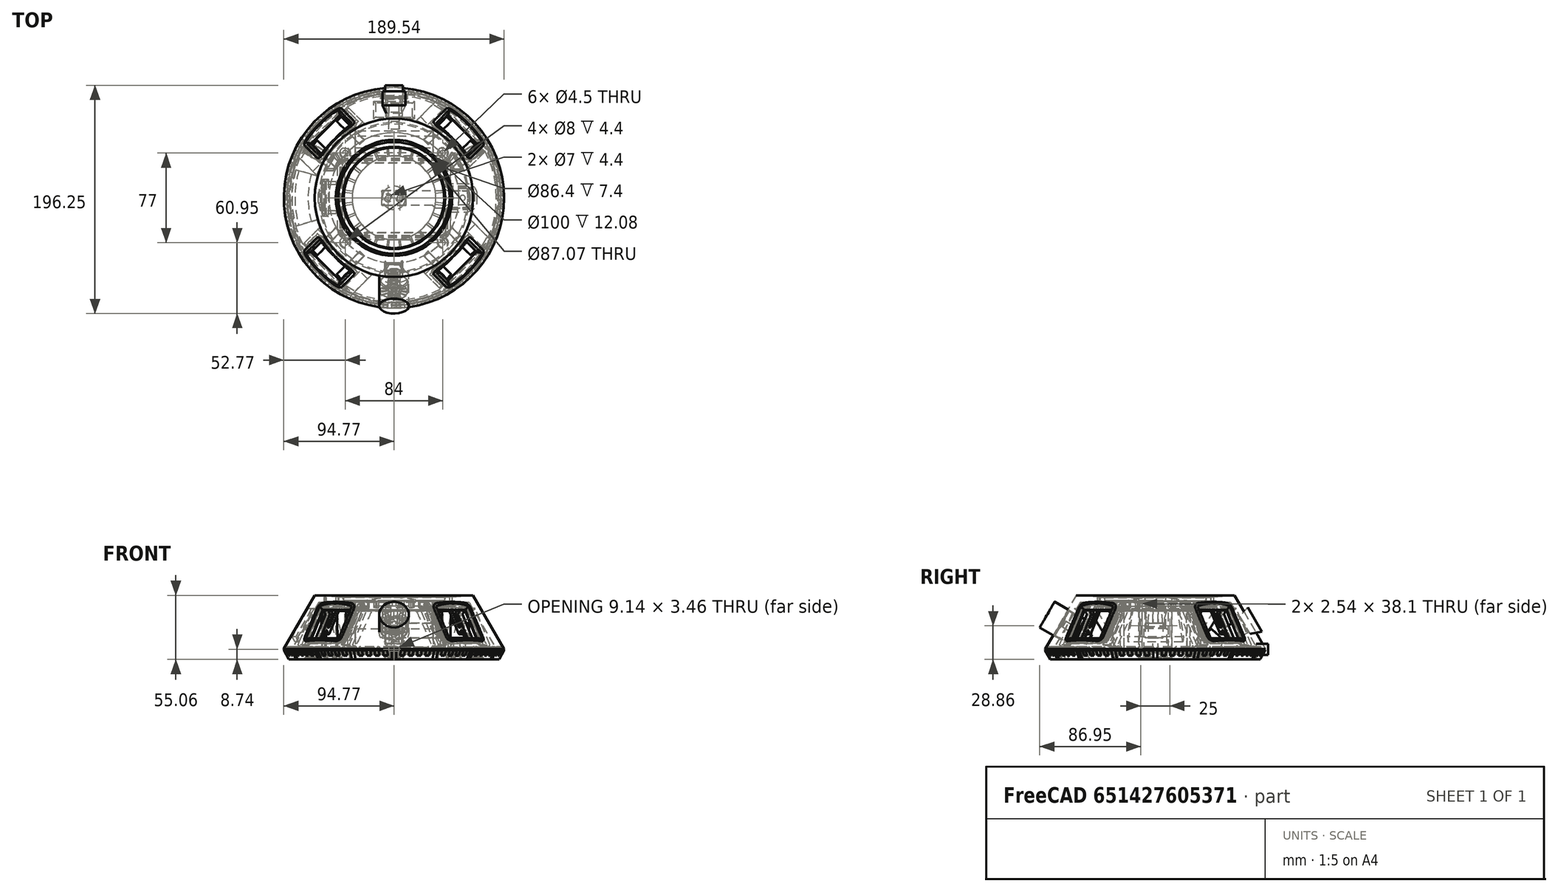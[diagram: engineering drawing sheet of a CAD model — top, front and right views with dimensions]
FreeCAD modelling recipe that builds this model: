
FCSTD DOCUMENT  (FreeCAD 1.0R38641 +1 (Git))
Label: case_v3_r2
License: All rights reserved
LicenseURL: https://en.wikipedia.org/wiki/All_rights_reserved
objects: Sketcher::SketchObject×45, PartDesign::SubShapeBinder×35, PartDesign::Boolean×20, Part::Feature×18, PartDesign::Pocket×14, PartDesign::Pad×14, PartDesign::Body×13, PartDesign::PolarPattern×10, PartDesign::Revolution×9, App::Link×8, Mesh::Feature×8, Part::FeaturePython×7, Part::Compound×5, Part::Cut×4, PartDesign::AdditiveLoft×4, PartDesign::Chamfer×3, PartDesign::MultiTransform×3, PartDesign::Groove×3, Part::Loft×2, Part::Offset2D×2, +6 more types
note: 400 computed .brp shape members not serialized (recipe doc carries the construction recipe); baked Part::Feature solids carry a one-line shape summary decoded from their .brp
EXTERNAL_REF file=parts_v3.FCStd obj=Body006
EXTERNAL_REF file=parts_v3.FCStd obj=Body001
EXTERNAL_REF file=parts_v3.FCStd obj=Body002
EXTERNAL_REF file=parts_v3.FCStd obj=Body005
EXTERNAL_REF file=parts_v3.FCStd obj=Body004
EXTERNAL_REF file=parts_v3.FCStd obj=Body008
EXTERNAL_REF file=parts_v3.FCStd obj=Body007
EXTERNAL_REF file=feet2.FCStd obj=Fusion

FEATURE [App::Link] Link  label="link_loadcell"
  LinkPlacement = pos=(27,-2.86108e-06,22.7) rot=(1,0,0;3.14159rad)
  LinkedObject = -> <external parts_v3.FCStd>#Body006
  Placement = pos=(27,-2.86108e-06,22.7) rot=(1,0,0;3.14159rad)
FEATURE [App::Link] Link001  label="link_display"
  LinkPlacement = pos=(51.5592,51.5591,19.869) rot=(0.48961,0.202803,0.848029;3.8172rad)
  LinkedObject = -> <external parts_v3.FCStd>#Body001
  Placement = pos=(51.5592,51.5591,19.869) rot=(0.48961,0.202803,0.848029;3.8172rad)
FEATURE [Sketcher::SketchObject] Sketch
  ArcFitTolerance = 1e-06
  AttachmentSupport = -> [XZ_Plane]
  FullyConstrained = true
  MakeInternals = false
  MapMode = 5
  Placement = pos=(0,0,0) rot=(1,0,0;1.5708rad)
  sketch-geometry (29):
    g0: LineSegment StartX=94.7691 StartY=0.4 StartZ=0 EndX=68.1243 EndY=46.55 EndZ=0
    g1: LineSegment [constr] StartX=50 StartY=45.0797 StartZ=0 EndX=50 EndY=0 EndZ=0
    g2: LineSegment [constr] StartX=50 StartY=0 StartZ=0 EndX=56 EndY=0 EndZ=0
    g3: LineSegment [constr] StartX=56 StartY=0 StartZ=0 EndX=56 EndY=33 EndZ=0
    g4: LineSegment StartX=63.55 StartY=40.55 StartZ=0 EndX=64.6602 EndY=40.55 EndZ=0
    g5: LineSegment StartX=64.6602 StartY=40.55 StartZ=0 EndX=88.0718 EndY=0 EndZ=0
    g6: LineSegment StartX=88.0718 StartY=0 StartZ=0 EndX=94.7681 EndY=0 EndZ=0
    g7: LineSegment StartX=50 StartY=45.0797 StartZ=0 EndX=68.1243 EndY=46.55 EndZ=0
    g8: LineSegment StartX=47.5346 StartY=44.8797 StartZ=0 EndX=43.5346 EndY=44.5552 EndZ=0
    g9: LineSegment StartX=47.5346 StartY=44.8797 StartZ=0 EndX=47.5346 EndY=37.3797 EndZ=0
    g10: LineSegment StartX=47.5346 StartY=37.3797 StartZ=0 EndX=0 EndY=37.3797 EndZ=0
    g11: LineSegment StartX=0 StartY=37.3797 StartZ=0 EndX=0 EndY=44.8797 EndZ=0
    g12: LineSegment StartX=43.5346 StartY=44.5552 StartZ=0 EndX=43.5346 EndY=41.3797 EndZ=0
    g13-g16: Circle [constr] x4 (B-spline internal-alignment scaffolding for g17; pole/knot coordinates omitted)
    g17: BSplineCurve PolesCount=4 KnotsCount=2 Degree=3 IsPeriodic=0
    g18: GeomPoint [constr] X=0 Y=44.8797 Z=0
    g19: GeomPoint [constr] X=43.5346 Y=41.3797 Z=0
    g20: GeomPoint [constr] X=95 Y=0 Z=0
    g21: ArcOfCircle [constr] CenterX=63.55 CenterY=33 CenterZ=0 NormalX=0 NormalY=0 NormalZ=1 AngleXU=0 Radius=7.55 StartAngle=1.5708 EndAngle=3.14159
    g22: GeomPoint [constr] X=56 Y=40.55 Z=0
    g23: LineSegment StartX=63.55 StartY=40.55 StartZ=0 EndX=56 EndY=33 EndZ=0
    g24: GeomPoint [constr] X=95 Y=0 Z=0
    g25: LineSegment StartX=94.7681 StartY=0 StartZ=0 EndX=94.7681 EndY=0.4 EndZ=0
    g26: LineSegment StartX=94.7691 StartY=0.4 StartZ=0 EndX=94.7681 EndY=0.4 EndZ=0
    g27: LineSegment StartX=56 StartY=33 StartZ=0 EndX=50 EndY=33 EndZ=0
    g28: LineSegment StartX=50 StartY=45.0797 StartZ=0 EndX=50 EndY=33 EndZ=0
  constraints (73):
    c: PointOnObject(g20,g-1)
    c: PointOnObject(g1,g-1)
    c: Coincident(g1,g2)
    c: PointOnObject(g2,g-1)
    c: Coincident(g2,g3)
    c: Horizontal(g4)
    c: Coincident(g4,g5)
    c: PointOnObject(g5,g-1)
    c: Coincident(g5,g6)
    c: DistanceX(g1) = 50
    c: Angle(g4,g5) = 2.0944
    c: Parallel(g5,g0)
    c: Distance(g20,g5) = 6
    c: Parallel(g3,g1)
    c: Distance(g1,g3) = 6
    c: Distance(g0,g4) = 6
    c: Vertical(g1)
    c: DistanceX(g20) = 95
    c: Coincident(g7,g1)
    c: Coincident(g7,g0)
    c: Distance(g22,g7) = 5
    c: Tangent(g8,g7)
    c: Coincident(g8,g9)
    c: Vertical(g9)
    c: Coincident(g9,g10)
    c: Horizontal(g10)
    c: Coincident(g10,g11)
    c: PointOnObject(g11,g-2)
    c: Vertical(g11)
    c: DistanceX(g8,g8) = 4
    c: Coincident(g12,g8)
    c: Vertical(g12)
    c: Weight(g13) = 1
    c: Equal(g13,g14)
    c: Equal(g13,g15)
    c: Equal(g13,g16)
    c: InternalAlignment(g13-g16 -> g17) x4
    c: InternalAlignment(g18,g17)
    c: InternalAlignment(g19,g17)
    c: Coincident(g17,g12)
    c: Coincident(g17,g11)
    c: Horizontal(g14,g11)
    c: Horizontal(g12,g15)
    c: DistanceY(g12,g11) = 3.5
    c: DistanceY(g10,g12) = 4
    c: Horizontal(g11,g8)
    c: Vertical(g15,g14)
    c: PointOnObject(g20,g0)
    c: PointOnObject(g20,g6)
    c: PointOnObject(g22,g3)
    c: PointOnObject(g22,g4)
    c: Tangent(g3,g21) = 1.5708
    c: Tangent(g4,g21) = 1.5708
    c: Coincident(g23,g3)
    c: Coincident(g23,g4)
    c: DistanceY(g0) = 46.55
    c: DistanceY(g8,g1) = 0.2
    c: DistanceY(g3) = 33
    c: PointOnObject(g24,g6)
    c: PointOnObject(g24,g0)
    c: Coincident(g25,g6)
    c: Vertical(g25)
    c: Coincident(g26,g0)
    c: Coincident(g26,g25)
    c: Horizontal(g26)
    c: DistanceY(g25,g25) = 0.4
    c: DistanceX(g26,g26) = 0.001
    c: DistanceX(g14) = 16
    c: Coincident(g27,g3)
    c: PointOnObject(g27,g1)
    c: Horizontal(g27)
    c: Coincident(g28,g1)
    c: Coincident(g28,g27)
FEATURE [PartDesign::Revolution] Revolution
  Angle = 360
  Angle2 = 60
  Axis = (0,2e-16,1)
  Base = (0,0,0)
  Placement = pos=(0,0,0) rot=(1,0,0;1.5708rad)
  Profile = -> Sketch
  ReferenceAxis = -> Sketch [V_Axis]
  Refine = true
  Suppressed = false
  Type = 0
FEATURE [App::Link] Link002  label="link_usb"
  LinkPlacement = pos=(4.80827e-07,85.5,2.99999) rot=(0,-1,0;3.14159rad)
  LinkedObject = -> <external parts_v3.FCStd>#Body002
  Placement = pos=(4.80827e-07,85.5,2.99999) rot=(0,-1,0;3.14159rad)
FEATURE [App::Link] Link003  label="link_switch"
  LinkPlacement = pos=(-3.18281e-07,76.966,20.9382) rot=(0.250563,-0.935113,-0.250563;1.63783rad)
  LinkedObject = -> <external parts_v3.FCStd>#Body005
  Placement = pos=(-3.18281e-07,76.966,20.9382) rot=(0.250563,-0.935113,-0.250563;1.63783rad)
FEATURE [Part::FeaturePython] Array  label="ArrayDisplay"  # Draft array (typed FeaturePython)
  AlwaysSyncPlacement = false
  Angle = 360
  ArrayType = 1
  Axis = (0,0,1)
  Base = -> Link001
  Center = (0,0,1)
  Count = 4
  ExpandArray = false
  Fuse = false
  IntervalAxis = (0,0,0)
  IntervalX = (50,0,0)
  IntervalY = (0,50,0)
  IntervalZ = (0,0,50)
  NumberCircles = 3
  NumberPolar = 4
  NumberX = 2
  NumberY = 2
  NumberZ = 1
  PlacementList = 4 placements: [(51.5592,51.5591,19.869),(-51.5591,51.5592,19.869),(-51.5592,-51.5591,19.869),(51.5591,-51.5592,19.869)]
  RadialDistance = 50
  ScaleList = (4) [(1,1,1),(1,1,1),(1,1,1),(1,1,1)]
  Symmetry = 1
  TangentialDistance = 25
FEATURE [App::Link] Link004  label="link_akku"
  LinkPlacement = pos=(-33.4675,48.0509,5.40002) rot=(0.707107,0,0.707107;3.14159rad)
  LinkedObject = -> <external parts_v3.FCStd>#Body004
  Placement = pos=(-33.4675,48.0509,5.40002) rot=(0.707107,0,0.707107;3.14159rad)
FEATURE [PartDesign::SubShapeBinder] Binder012
  BindCopyOnChange = 0
  BindMode = 0
  ClaimChildren = false
  Context = -> Body [Binder012.]
  Fuse = false
  MakeFace = true
  OffsetFill = false
  OffsetIntersection = false
  OffsetJoinType = 0
  OffsetOpenResult = false
  PartialLoad = false
  Refine = true
  Relative = true
  Support = -> [Link001[Pad028.Face4]]
  _Version = 2
FEATURE [PartDesign::Pocket] Pocket  label="PocketDisplayBack"
  BaseFeature = -> Revolution
  Direction = (0.612372,0.612372,0.5)
  Length = 7
  Length2 = 1
  Placement = pos=(0,0,0) rot=(1,0,0;1.5708rad)
  Profile = -> Binder012
  Refine = true
  Reversed = true
  Suppressed = false
  Type = 4
FEATURE [PartDesign::PolarPattern] PolarPattern
  Angle = 360
  Axis = -> Z_Axis
  BaseFeature = -> Pocket
  Mode = 0
  Occurrences = 4
  Offset = 120
  Originals = -> [Pocket]
  Placement = pos=(0,0,0) rot=(1,0,0;1.5708rad)
  Refine = true
  Suppressed = false
  TransformMode = 0
FEATURE [PartDesign::Body] Body  label="BaseShape"
  AllowCompound = true
  Group = -> [Sketch,Revolution,Binder012,Pocket,PolarPattern]
  Origin = -> Origin
  Tip = -> PolarPattern
FEATURE [Part::Cut] Cut  label="CutDisplay"
  Base = -> Body
  Refine = true
  Tool = -> Array
FEATURE [Sketcher::SketchObject] Sketch015
  ArcFitTolerance = 1e-06
  AttachmentSupport = -> [YZ_Plane010]
  FullyConstrained = true
  MakeInternals = false
  MapMode = 5
  Placement = pos=(0,0,0) rot=(0.57735,-0.57735,-0.57735;2.0944rad)
  sketch-geometry (27):
    g0: LineSegment StartX=94.7691 StartY=-1 StartZ=0 EndX=90.4389 EndY=-8.5 EndZ=0
    g1: LineSegment StartX=90.4389 StartY=-8.5 StartZ=0 EndX=10 EndY=-8.5 EndZ=0
    g2: LineSegment StartX=10 StartY=-8.5 StartZ=0 EndX=10 EndY=-2.5 EndZ=0
    g3: LineSegment StartX=94.1691 StartY=0 StartZ=0 EndX=94.1691 EndY=-0.6 EndZ=0
    g4: LineSegment StartX=94.7691 StartY=-0.6 StartZ=0 EndX=94.1691 EndY=-0.6 EndZ=0
    g5: LineSegment StartX=89.4876 StartY=-2.5 StartZ=0 EndX=10 EndY=-2.5 EndZ=0
    g6: LineSegment [constr] StartX=95 StartY=0 StartZ=0 EndX=89.2265 EndY=10 EndZ=0
    g7: LineSegment [constr] StartX=89 StartY=0 StartZ=0 EndX=83.2265 EndY=10 EndZ=0
    g8: LineSegment StartX=89.9876 StartY=1.1 StartZ=0 EndX=89.3876 EndY=1.7 EndZ=0
    g9: LineSegment StartX=89.3876 StartY=1.7 StartZ=0 EndX=89.9876 EndY=2.41505 EndZ=0
    g10: LineSegment StartX=89.9876 StartY=2.41505 StartZ=0 EndX=91.7876 EndY=2.41505 EndZ=0
    g11: LineSegment StartX=92.6876 StartY=1.7 StartZ=0 EndX=92.2876 EndY=1.7 EndZ=0
    g12: LineSegment [constr] StartX=92.6876 StartY=1.7 StartZ=0 EndX=93.6691 EndY=0 EndZ=0
    g13: LineSegment StartX=94.7691 StartY=-0.6 StartZ=0 EndX=94.7691 EndY=-1 EndZ=0
    g14: LineSegment [constr] StartX=94.7691 StartY=-1 StartZ=0 EndX=95 EndY=-0.6 EndZ=0
    g15: LineSegment [constr] StartX=95 StartY=-0.6 StartZ=0 EndX=94.7691 EndY=-0.6 EndZ=0
    g16: LineSegment StartX=94.1691 StartY=0 StartZ=0 EndX=92.6876 EndY=0 EndZ=0
    g17: LineSegment StartX=89.9876 StartY=1.1 StartZ=0 EndX=89.9876 EndY=0 EndZ=0
    g18: LineSegment StartX=89.9876 StartY=0 StartZ=0 EndX=89.9876 EndY=-3.9 EndZ=0
    g19: LineSegment StartX=91.7876 StartY=-2.9 StartZ=0 EndX=91.7876 EndY=0 EndZ=0
    g20: LineSegment StartX=91.7876 StartY=0 StartZ=0 EndX=91.7876 EndY=2.41505 EndZ=0
    g21: LineSegment StartX=92.2876 StartY=1.7 StartZ=0 EndX=92.2876 EndY=0 EndZ=0
    g22: LineSegment StartX=92.2876 StartY=0 StartZ=0 EndX=92.2876 EndY=-2.9 EndZ=0
    g23: LineSegment StartX=91.7876 StartY=-2.9 StartZ=0 EndX=92.2876 EndY=-2.9 EndZ=0
    g24: LineSegment StartX=89.4876 StartY=-2.5 StartZ=0 EndX=89.4876 EndY=-3.9 EndZ=0
    g25: LineSegment StartX=89.4876 StartY=-3.9 StartZ=0 EndX=89.9876 EndY=-3.9 EndZ=0
    g26: LineSegment StartX=92.6876 StartY=0 StartZ=0 EndX=92.6876 EndY=1.7 EndZ=0
  constraints (81):
    c: Coincident(g0,g1)
    c: Horizontal(g1)
    c: Coincident(g1,g2)
    c: Vertical(g2)
    c: Angle(g0,g1) = 2.0944
    c: DistanceX(g2) = 10
    c: Coincident(g4,g3)
    c: Horizontal(g4)
    c: DistanceX(g4,g4) = 0.6
    c: Horizontal(g5)
    c: Coincident(g2,g5)
    c: Vertical(g3)
    c: PointOnObject(g6,g-1)
    c: Angle(g-1,g6) = 2.0944
    c: PointOnObject(g7,g-1)
    c: DistanceX(g7) = 89
    c: Parallel(g7,g6)
    c: DistanceY(g0) = -8.5
    c: Coincident(g8,g9)
    c: Coincident(g9,g10)
    c: Horizontal(g10)
    c: DistanceX(g8,g8) = 0.6
    c: Angle(g9,g10) = 2.26893
    c: Distance(g12,g3) = 0.5
    c: DistanceX(g10,g10) = 1.8
    c: Angle(g12,g-1) = 1.0472
    c: Coincident(g12,g11)
    c: Horizontal(g6,g7)
    c: DistanceY(g7) = 10
    c: DistanceY(g8) = 1.7
    c: Coincident(g13,g4)
    c: Vertical(g13)
    c: DistanceY(g13,g13) = 0.4
    c: Coincident(g14,g15)
    c: Coincident(g15,g4)
    c: Horizontal(g15)
    c: Tangent(g0,g14) = 1.5708
    c: DistanceX(g14) = 95
    c: Coincident(g0,g13)
    c: Vertical(g6,g14)
    c: DistanceY(g4) = -0.6
    c: Coincident(g16,g3)
    c: Horizontal(g16)
    c: PointOnObject(g12,g16)
    c: DistanceY(g5) = -2.5
    c: Horizontal(g8,g11)
    c: DistanceX(g8,g11) = 3.3
    c: Angle(g8,g-1) = 0.785398
    c: Coincident(g8,g17)
    c: PointOnObject(g17,g-1)
    c: Vertical(g17)
    c: Coincident(g17,g18)
    c: PointOnObject(g19,g-1)
    c: Coincident(g19,g20)
    c: Coincident(g20,g10)
    c: Vertical(g20)
    c: PointOnObject(g21,g-1)
    c: Coincident(g21,g22)
    c: PointOnObject(g16,g-1)
    c: Vertical(g21)
    c: Coincident(g23,g19)
    c: Coincident(g23,g22)
    c: Parallel(g19,g18)
    c: Coincident(g5,g24)
    c: Coincident(g24,g25)
    c: Coincident(g25,g18)
    c: Horizontal(g25)
    c: Horizontal(g23)
    c: Parallel(g19,g22)
    c: Parallel(g24,g18)
    c: Coincident(g26,g11)
    c: Vertical(g26)
    c: DistanceY(g18,g8) = 5
    c: Vertical(g18)
    c: Coincident(g26,g16)
    c: Vertical(g8,g9)
    c: Coincident(g21,g11)
    c: DistanceX(g10,g11) = 0.5
    c: Horizontal(g11)
    c: Equal(g23,g25)
    c: DistanceY(g18,g19) = 1
FEATURE [PartDesign::Revolution] Revolution001
  Angle = 360
  Angle2 = 60
  Axis = (0,0,1)
  Base = (0,0,0)
  Placement = pos=(0,0,0) rot=(1,1,1;2.0944rad)
  Profile = -> Sketch015
  ReferenceAxis = -> Sketch015 [V_Axis]
  Refine = true
  Reversed = true
  Suppressed = false
  Type = 0
FEATURE [PartDesign::SubShapeBinder] Binder014
  BindCopyOnChange = 0
  BindMode = 0
  ClaimChildren = false
  Context = -> Array001 [Binder014.]
  Fuse = false
  MakeFace = true
  Offset = 5
  OffsetFill = false
  OffsetIntersection = false
  OffsetJoinType = 0
  OffsetOpenResult = false
  PartialLoad = false
  Refine = true
  Relative = true
  Support = -> [Cut[Edge167,Edge166,Edge169,Edge168]]
  _Version = 2
FEATURE [PartDesign::Pad] Pad
  Direction = (0.612372,0.612372,0.5)
  Length = 10
  Length2 = 10
  Profile = -> Binder014
  Refine = true
  Suppressed = false
  Type = 0
FEATURE [PartDesign::Body] Body001  label="Dispcut"
  AllowCompound = false
  Group = -> [Binder014,Pad]
  Origin = -> Origin001
  Tip = -> Pad
FEATURE [Part::MultiCommon] Common  label="base_bezel"
  Refine = true
  Shapes = -> [Body001,Cut]
FEATURE [Part::FeaturePython] Array001  label="ArrayDispcut"  # Draft array (typed FeaturePython)
  AlwaysSyncPlacement = false
  Angle = 360
  ArrayType = 1
  Axis = (0,0,1)
  Base = -> Body001
  Center = (0,0,1)
  Count = 4
  ExpandArray = false
  Fuse = false
  IntervalAxis = (0,0,0)
  IntervalX = (50,0,0)
  IntervalY = (0,50,0)
  IntervalZ = (0,0,50)
  NumberCircles = 3
  NumberPolar = 4
  NumberX = 2
  NumberY = 2
  NumberZ = 1
  PlacementList = 4 placements: [(0,0,0),(0,0,0),(0,0,0),(0,0,0)]
  RadialDistance = 50
  ScaleList = (4) [(1,1,1),(1,1,1),(1,1,1),(1,1,1)]
  Symmetry = 1
  TangentialDistance = 25
FEATURE [Part::Cut] Cut001  label="CutBezel"
  Base = -> Cut
  Refine = true
  Tool = -> Array001
FEATURE [Part::FeaturePython] Slice_child6  label="base_top"  # WARN: FeaturePython — macro-defined, semantics opaque (R4)
  Base = -> Cut001
  FilterType = 1
  Invert = false
  OverrideMaxVal = 0
  WindowFrom = 80
  WindowTo = 100
  items = 1
FEATURE [Part::FeaturePython] CompoundFilter  label="base_outer"  # WARN: FeaturePython — macro-defined, semantics opaque (R4)
  Base = -> Cut001
  FilterType = 1
  Invert = false
  OverrideMaxVal = 0
  WindowFrom = 80
  WindowTo = 100
  items = 0
FEATURE [App::Link] Link005  label="link_esp"
  LinkPlacement = pos=(-58.2736,-4.46698e-09,44.8) rot=(-0.707107,0,0.707107;3.14159rad)
  LinkedObject = -> <external parts_v3.FCStd>#Body008
  Placement = pos=(-58.2736,-4.46698e-09,44.8) rot=(-0.707107,0,0.707107;3.14159rad)
FEATURE [App::Link] Link006  label="link_encoder"
  LinkPlacement = pos=(-2.17522e-06,-65.3643,13.9856) rot=(0.447214,0.447214,-0.774597;1.82348rad)
  LinkedObject = -> <external parts_v3.FCStd>#Body007
  Placement = pos=(-2.17522e-06,-65.3643,13.9856) rot=(0.447214,0.447214,-0.774597;1.82348rad)
FEATURE [Sketcher::SketchObject] Sketch017
  ArcFitTolerance = 1e-06
  AttachmentSupport = -> [XY_Plane011]
  FullyConstrained = true
  MakeInternals = false
  MapMode = 5
  sketch-geometry (7):
    g0: LineSegment StartX=0 StartY=3 StartZ=0 EndX=8 EndY=3 EndZ=0
    g1: LineSegment StartX=8 StartY=3 StartZ=0 EndX=8 EndY=0 EndZ=0
    g2: LineSegment StartX=8 StartY=0 StartZ=0 EndX=9 EndY=-1.1e-15 EndZ=0
    g3: ArcOfCircle CenterX=27.5 CenterY=-3.4e-15 CenterZ=0 NormalX=0 NormalY=0 NormalZ=1 AngleXU=0 Radius=18.5 StartAngle=2.8113 EndAngle=3.14159
    g4: ArcOfCircle CenterX=-7.5 CenterY=12 CenterZ=0 NormalX=0 NormalY=0 NormalZ=1 AngleXU=0 Radius=18.5 StartAngle=5.95289 EndAngle=6.28319
    g5: LineSegment StartX=11 StartY=12 StartZ=0 EndX=0 EndY=12 EndZ=0
    g6: LineSegment StartX=0 StartY=12 StartZ=0 EndX=0 EndY=3 EndZ=0
  constraints (22):
    c: PointOnObject(g0,g-2)
    c: Horizontal(g0)
    c: Coincident(g0,g1)
    c: PointOnObject(g1,g-1)
    c: Vertical(g1)
    c: Coincident(g1,g2)
    c: PointOnObject(g2,g-1)
    c: Perpendicular(g2,g3) = 4.71239
    c: Tangent(g3,g4) = 1.5708
    c: Coincident(g4,g5)
    c: PointOnObject(g5,g-2)
    c: Horizontal(g5)
    c: Coincident(g5,g6)
    c: Coincident(g6,g0)
    c: DistanceY(g1,g1) = 3
    c: DistanceX(g2,g2) = 1
    c: DistanceY(g5) = 12
    c: Perpendicular(g4,g5)
    c: DistanceX(g5,g5) = 11
    c: DistanceX(g3,g4) = 1
    c: DistanceX(g2,g3) = 1
    c: DistanceX(g0,g0) = 8
FEATURE [PartDesign::Revolution] Revolution002
  Angle = 30
  Angle2 = 60
  Axis = (1,0,0)
  Base = (0,0,0)
  Profile = -> Sketch017
  ReferenceAxis = -> Sketch017 [H_Axis]
  Refine = true
  Suppressed = false
  Type = 0
FEATURE [Sketcher::SketchObject] Sketch018
  ArcFitTolerance = 1e-06
  AttachmentSupport = -> [XY_Plane011]
  FullyConstrained = true
  MakeInternals = false
  MapMode = 5
  expr: Constraints[10] = Sketch017.Constraints[14]
  expr: Constraints[11] = Sketch017.Constraints[16]
  sketch-geometry (7):
    g0: LineSegment StartX=0 StartY=3 StartZ=0 EndX=8 EndY=3 EndZ=0
    g1: LineSegment StartX=8 StartY=3 StartZ=0 EndX=8 EndY=0 EndZ=0
    g2: LineSegment StartX=8 StartY=0 StartZ=0 EndX=9 EndY=-2.8e-15 EndZ=0
    g3: ArcOfCircle CenterX=27.5 CenterY=-5.1e-15 CenterZ=0 NormalX=0 NormalY=0 NormalZ=1 AngleXU=0 Radius=18.5 StartAngle=2.8113 EndAngle=3.14159
    g4: LineSegment StartX=10 StartY=12 StartZ=0 EndX=0 EndY=12 EndZ=0
    g5: LineSegment StartX=0 StartY=12 StartZ=0 EndX=0 EndY=3 EndZ=0
    g6: LineSegment StartX=10 StartY=6 StartZ=0 EndX=10 EndY=12 EndZ=0
  constraints (21):
    c: Horizontal(g0)
    c: Coincident(g0,g1)
    c: PointOnObject(g1,g-1)
    c: Vertical(g1)
    c: Coincident(g1,g2)
    c: PointOnObject(g2,g-1)
    c: Perpendicular(g2,g3) = 4.71239
    c: Horizontal(g4)
    c: Coincident(g4,g5)
    c: Coincident(g5,g0)
    c: DistanceY(g1,g1) = 3
    c: DistanceY(g4) = 12
    c: DistanceX(g3) = 10
    c: Vertical(g5)
    c: PointOnObject(g0,g-2)
    c: DistanceY(g3) = 6
    c: Coincident(g6,g3)
    c: Coincident(g6,g4)
    c: Vertical(g6)
    c: DistanceX(g2,g3) = 1
    c: DistanceX(g0,g0) = 8
FEATURE [PartDesign::Revolution] Revolution003
  Angle = 30
  Angle2 = 60
  Axis = (1,0,0)
  Base = (0,0,0)
  BaseFeature = -> Revolution002
  Profile = -> Sketch018
  ReferenceAxis = -> Sketch018 [H_Axis]
  Refine = true
  Reversed = true
  Suppressed = false
  Type = 0
FEATURE [PartDesign::PolarPattern] PolarPattern001
  Angle = 360
  Axis = -> X_Axis011
  BaseFeature = -> Revolution003
  Mode = 0
  Occurrences = 6
  Offset = 120
  Refine = true
  Suppressed = false
  TransformMode = 1
FEATURE [Sketcher::SketchObject] Sketch021
  ArcFitTolerance = 1e-06
  AttachmentOffset = pos=(0,0,0) rot=(0,0,1;-1.5708rad)
  AttachmentSupport = -> [XY_Plane010]
  FullyConstrained = true
  MakeInternals = false
  MapMode = 5
  Placement = pos=(0,0,0) rot=(0,0,1;4.71239rad)
  sketch-geometry (4):
    g0: LineSegment StartX=-97.6 StartY=7.575 StartZ=0 EndX=-97.6 EndY=-7.575 EndZ=0
    g1: LineSegment StartX=-97.6 StartY=-7.575 StartZ=0 EndX=-86.8 EndY=-7.575 EndZ=0
    g2: LineSegment StartX=-86.8 StartY=-7.575 StartZ=0 EndX=-86.8 EndY=7.575 EndZ=0
    g3: LineSegment StartX=-86.8 StartY=7.575 StartZ=0 EndX=-97.6 EndY=7.575 EndZ=0
  constraints (11):
    c: Coincident(g0,g1)
    c: Coincident(g1,g2)
    c: Coincident(g2,g3)
    c: Coincident(g3,g0)
    c: Vertical(g0)
    c: Horizontal(g1)
    c: Horizontal(g3)
    c: Symmetric(g2,g1,g-1)
    c: DistanceY(g0,g0) = 15.15
    c: DistanceX(g1,g1) = 10.8
    c: DistanceX(g1) = -86.8
FEATURE [PartDesign::SubShapeBinder] Binder  label="Binder_usb"
  BindCopyOnChange = 0
  BindMode = 0
  ClaimChildren = false
  Context = -> Body010 [Boolean.Binder.]
  Fuse = false
  MakeFace = true
  OffsetFill = false
  OffsetIntersection = false
  OffsetJoinType = 0
  OffsetOpenResult = false
  PartialLoad = false
  Refine = true
  Relative = true
  Support = -> [Link002[Pad022.]]
  _Version = 2
FEATURE [PartDesign::SubShapeBinder] Binder015
  BindCopyOnChange = 0
  BindMode = 0
  ClaimChildren = false
  Context = -> Body010 [Binder015.]
  Fuse = false
  MakeFace = true
  OffsetFill = false
  OffsetIntersection = false
  OffsetJoinType = 0
  OffsetOpenResult = false
  PartialLoad = false
  Refine = true
  Relative = true
  Support = -> [Link004[Pad.]]
  _Version = 2
FEATURE [Sketcher::SketchObject] Sketch024  label="SketchInnerBottom"
  ArcFitTolerance = 1e-06
  AttachmentOffset = pos=(0,0,0) rot=(0,0,1;3.14159rad)
  AttachmentSupport = -> [XY_Plane012]
  FullyConstrained = true
  MakeInternals = false
  MapMode = 5
  Placement = pos=(0,0,0) rot=(0,0,1;3.14159rad)
  sketch-geometry (10):
    g0: LineSegment StartX=-39.5 StartY=-30 StartZ=0 EndX=39.5 EndY=-30 EndZ=0
    g1: LineSegment StartX=42.5 StartY=-27 StartZ=0 EndX=42.5 EndY=27 EndZ=0
    g2: LineSegment StartX=39.5 StartY=30 StartZ=0 EndX=-39.5 EndY=30 EndZ=0
    g3: LineSegment StartX=-42.5 StartY=27 StartZ=0 EndX=-42.5 EndY=-27 EndZ=0
    g4: ArcOfCircle CenterX=-39.5 CenterY=-27 CenterZ=0 NormalX=0 NormalY=0 NormalZ=1 AngleXU=0 Radius=3 StartAngle=3.14159 EndAngle=4.71239
    g5: ArcOfCircle CenterX=39.5 CenterY=-27 CenterZ=0 NormalX=0 NormalY=0 NormalZ=1 AngleXU=0 Radius=3 StartAngle=4.71239 EndAngle=6.28319
    g6: ArcOfCircle CenterX=39.5 CenterY=27 CenterZ=0 NormalX=0 NormalY=0 NormalZ=1 AngleXU=0 Radius=3 StartAngle=2e-16 EndAngle=1.5708
    g7: ArcOfCircle CenterX=-39.5 CenterY=27 CenterZ=0 NormalX=0 NormalY=0 NormalZ=1 AngleXU=0 Radius=3 StartAngle=1.5708 EndAngle=3.14159
    g8: GeomPoint [constr] X=42.5 Y=30 Z=0
    g9: GeomPoint [constr] X=0 Y=0 Z=0
  constraints (22):
    c: Tangent(g0,g4) = -1.5708
    c: Tangent(g0,g5) = -1.5708
    c: Tangent(g1,g5) = -1.5708
    c: Tangent(g1,g6) = -1.5708
    c: Tangent(g2,g6) = -1.5708
    c: Tangent(g2,g7) = -1.5708
    c: Tangent(g3,g7) = -1.5708
    c: Tangent(g3,g4) = -1.5708
    c: Horizontal(g0)
    c: Horizontal(g2)
    c: Vertical(g1)
    c: Vertical(g3)
    c: Equal(g4,g5)
    c: Equal(g5,g6)
    c: Equal(g6,g7)
    c: Symmetric(g2,g0,g9)
    c: PointOnObject(g8,g1)
    c: PointOnObject(g8,g2)
    c: Distance(g1,g3) = 85
    c: Distance(g0,g2) = 60
    c: Radius(g5) = 3
    c: Coincident(g9,g-1)
FEATURE [Sketcher::SketchObject] Sketch025  label="SketchInnerTop"
  ArcFitTolerance = 1e-06
  AttachmentOffset = pos=(0,0,33) rot=(0,0,1;0rad)
  AttachmentSupport = -> [XY_Plane012]
  FullyConstrained = true
  MakeInternals = false
  MapMode = 5
  Placement = pos=(0,0,33) rot=(0,0,1;0rad)
  sketch-geometry (1):
    g0: Circle CenterX=0 CenterY=0 CenterZ=0 NormalX=0 NormalY=0 NormalZ=1 AngleXU=0 Radius=50
  constraints (2):
    c: Diameter(g0) = 100
    c: Coincident(g0,g-1)
FEATURE [Sketcher::SketchObject] Sketch027
  ArcFitTolerance = 1e-06
  AttachmentSupport = -> [XY_Plane012]
  FullyConstrained = true
  MakeInternals = false
  MapMode = 5
  sketch-geometry (8):
    g0: LineSegment StartX=47.5 StartY=12 StartZ=0 EndX=67.5 EndY=12 EndZ=0
    g1: LineSegment StartX=70.5 StartY=9 StartZ=0 EndX=70.5 EndY=-11.8 EndZ=0
    g2: LineSegment StartX=67.5 StartY=-14.8 StartZ=0 EndX=47.5 EndY=-14.8 EndZ=0
    g3: LineSegment StartX=47.5 StartY=-14.8 StartZ=0 EndX=47.5 EndY=12 EndZ=0
    g4: ArcOfCircle CenterX=67.5 CenterY=9 CenterZ=0 NormalX=0 NormalY=0 NormalZ=1 AngleXU=0 Radius=3 StartAngle=0 EndAngle=1.5708
    g5: GeomPoint [constr] X=70.5 Y=12 Z=0
    g6: ArcOfCircle CenterX=67.5 CenterY=-11.8 CenterZ=0 NormalX=0 NormalY=0 NormalZ=1 AngleXU=0 Radius=3 StartAngle=4.71239 EndAngle=6.28319
    g7: GeomPoint [constr] X=70.5 Y=-14.8 Z=0
  constraints (20):
    c: DistanceX(g3) = 47.5
    c: Horizontal(g0)
    c: Vertical(g1)
    c: Horizontal(g2)
    c: Coincident(g2,g3)
    c: Vertical(g3)
    c: PointOnObject(g5,g0)
    c: PointOnObject(g5,g1)
    c: Tangent(g0,g4) = 1.5708
    c: Tangent(g1,g4) = 1.5708
    c: PointOnObject(g7,g1)
    c: PointOnObject(g7,g2)
    c: Tangent(g1,g6) = 1.5708
    c: Tangent(g2,g6) = 1.5708
    c: Equal(g6,g4)
    c: Radius(g4) = 3
    c: Coincident(g3,g0)
    c: DistanceX(g0,g0) = 20
    c: DistanceY(g0) = 12
    c: DistanceY(g2) = -14.8
FEATURE [Part::Loft] Loft
  Closed = false
  MaxDegree = 5
  Ruled = false
  Sections = -> [Sketch024,Sketch025]
  Solid = true
FEATURE [Part::Offset2D] Offset2D
  Fill = false
  Intersection = false
  Join = 0
  Mode = 1
  SelfIntersection = false
  Source = -> Sketch024
  Value = 6
FEATURE [Part::Offset2D] Offset2D001
  Fill = false
  Intersection = false
  Join = 0
  Mode = 1
  SelfIntersection = false
  Source = -> Sketch025
  Value = 6
FEATURE [Part::Loft] Loft001
  Closed = false
  MaxDegree = 5
  Ruled = false
  Sections = -> [Offset2D001,Offset2D]
  Solid = true
FEATURE [Part::Cut] Cut002  label="base_inner"
  Base = -> Loft001
  Refine = true
  Tool = -> Loft
FEATURE [PartDesign::FeatureBase] BaseFeature
  BaseFeature = -> Cut002
  Suppressed = false
FEATURE [Sketcher::SketchObject] Sketch028
  ArcFitTolerance = 1e-06
  AttachmentOffset = pos=(0,0,10) rot=(0,0,1;0rad)
  AttachmentSupport = -> [XY_Plane012]
  FullyConstrained = true
  MakeInternals = false
  MapMode = 5
  Placement = pos=(0,0,10) rot=(0,0,1;0rad)
  sketch-geometry (11):
    g0: LineSegment StartX=40 StartY=6.8 StartZ=0 EndX=40 EndY=-9.1 EndZ=0
    g1: LineSegment StartX=40 StartY=6.8 StartZ=0 EndX=64.5 EndY=6.8 EndZ=0
    g2: LineSegment StartX=40 StartY=-9.1 StartZ=0 EndX=71.5 EndY=-9.1 EndZ=0
    g3: ArcOfCircle CenterX=64.5 CenterY=5.8 CenterZ=0 NormalX=0 NormalY=0 NormalZ=1 AngleXU=0 Radius=1 StartAngle=0 EndAngle=1.5708
    g4: GeomPoint [constr] X=65.5 Y=6.8 Z=0
    g5: GeomPoint [constr] X=65.5 Y=-9.1 Z=0
    g6: LineSegment StartX=65.5 StartY=5.8 StartZ=0 EndX=65.5 EndY=-7.1 EndZ=0
    g7: LineSegment StartX=66.5 StartY=-8.1 StartZ=0 EndX=71.5 EndY=-8.1 EndZ=0
    g8: LineSegment StartX=71.5 StartY=-8.1 StartZ=0 EndX=71.5 EndY=-9.1 EndZ=0
    g9: ArcOfCircle CenterX=66.5 CenterY=-7.1 CenterZ=0 NormalX=0 NormalY=0 NormalZ=1 AngleXU=0 Radius=1 StartAngle=3.14159 EndAngle=4.71239
    g10: GeomPoint [constr] X=65.5 Y=-8.1 Z=0
  constraints (28):
    c: Vertical(g0)
    c: DistanceX(g0) = 40
    c: Horizontal(g1)
    c: Horizontal(g2)
    c: DistanceY(g5,g-1) = 9.1
    c: DistanceY(g4) = 6.8
    c: Coincident(g1,g0)
    c: Coincident(g2,g0)
    c: DistanceX(g1,g4) = 25.5
    c: PointOnObject(g4,g1)
    c: Tangent(g1,g3) = 1.5708
    c: PointOnObject(g5,g2)
    c: Radius(g3) = 1
    c: Vertical(g6)
    c: PointOnObject(g4,g6)
    c: PointOnObject(g5,g6)
    c: Horizontal(g7)
    c: Coincident(g7,g8)
    c: Coincident(g8,g2)
    c: Vertical(g8)
    c: DistanceY(g8,g8) = 1
    c: PointOnObject(g10,g6)
    c: PointOnObject(g10,g7)
    c: Tangent(g6,g9) = -1.5708
    c: Tangent(g7,g9) = -1.5708
    c: Equal(g9,g3)
    c: DistanceX(g7,g7) = 5
    c: Tangent(g6,g3) = 1.5708
FEATURE [Sketcher::SketchObject] Sketch029
  ArcFitTolerance = 1e-06
  AttachmentOffset = pos=(0,0,26) rot=(0,0,1;0rad)
  AttachmentSupport = -> [XY_Plane012]
  FullyConstrained = true
  MakeInternals = false
  MapMode = 5
  Placement = pos=(0,0,26) rot=(0,0,1;0rad)
  sketch-geometry (8):
    g0: LineSegment StartX=49.5 StartY=12.3 StartZ=0 EndX=67.5 EndY=12.3 EndZ=0
    g1: LineSegment StartX=70.5 StartY=9.3 StartZ=0 EndX=70.5 EndY=-11.8 EndZ=0
    g2: LineSegment StartX=67.5 StartY=-14.8 StartZ=0 EndX=49.5 EndY=-14.8 EndZ=0
    g3: LineSegment StartX=49.5 StartY=-14.8 StartZ=0 EndX=49.5 EndY=12.3 EndZ=0
    g4: ArcOfCircle CenterX=67.5 CenterY=9.3 CenterZ=0 NormalX=0 NormalY=0 NormalZ=1 AngleXU=0 Radius=3 StartAngle=2e-16 EndAngle=1.5708
    g5: GeomPoint [constr] X=70.5 Y=12.3 Z=0
    g6: ArcOfCircle CenterX=67.5 CenterY=-11.8 CenterZ=0 NormalX=0 NormalY=0 NormalZ=1 AngleXU=0 Radius=3 StartAngle=4.71239 EndAngle=6.28319
    g7: GeomPoint [constr] X=70.5 Y=-14.8 Z=0
  constraints (20):
    c: DistanceX(g3) = 49.5
    c: Horizontal(g0)
    c: Vertical(g1)
    c: Horizontal(g2)
    c: Coincident(g2,g3)
    c: Vertical(g3)
    c: PointOnObject(g5,g0)
    c: PointOnObject(g5,g1)
    c: Tangent(g0,g4) = 1.5708
    c: Tangent(g1,g4) = 1.5708
    c: PointOnObject(g7,g1)
    c: PointOnObject(g7,g2)
    c: Tangent(g1,g6) = 1.5708
    c: Tangent(g2,g6) = 1.5708
    c: Equal(g6,g4)
    c: Radius(g4) = 3
    c: Coincident(g3,g0)
    c: DistanceY(g0) = 12.3
    c: DistanceY(g2) = -14.8
    c: DistanceX(g0,g0) = 18
FEATURE [PartDesign::AdditiveLoft] AdditiveLoft  label="AdditiveLC"
  BaseFeature = -> BaseFeature
  Closed = false
  Profile = -> Sketch027
  Refine = true
  Ruled = false
  Sections = -> [Sketch029]
  Suppressed = false
FEATURE [PartDesign::Pocket] Pocket003  label="PocketLC"
  BaseFeature = -> AdditiveLoft
  Direction = (0,0,-1)
  Length = 14
  Length2 = 5
  Profile = -> Sketch028
  ReferenceAxis = -> Sketch028 [N_Axis]
  Refine = true
  Reversed = true
  Suppressed = false
  Type = 0
FEATURE [Sketcher::SketchObject] Sketch030
  ArcFitTolerance = 1e-06
  AttachmentOffset = pos=(0,0,0) rot=(0,0,1;-1.5708rad)
  AttachmentSupport = -> [XY_Plane012]
  FullyConstrained = false
  MakeInternals = false
  MapMode = 5
  Placement = pos=(0,0,0) rot=(0,0,1;4.71239rad)
  sketch-geometry (65):
    g0: LineSegment StartX=-35 StartY=6 StartZ=0 EndX=-35 EndY=-6 EndZ=0
    g1: LineSegment StartX=-35 StartY=-6 StartZ=0 EndX=35 EndY=-6 EndZ=0
    g2: LineSegment StartX=35 StartY=-6 StartZ=0 EndX=35 EndY=6 EndZ=0
    g3: LineSegment StartX=35 StartY=6 StartZ=0 EndX=-35 EndY=6 EndZ=0
    g4: Circle CenterX=0 CenterY=0 CenterZ=0 NormalX=0 NormalY=0 NormalZ=1 AngleXU=0 Radius=2.8
    g5: LineSegment StartX=-58 StartY=11 StartZ=0 EndX=-88 EndY=11 EndZ=0
    g6: LineSegment StartX=-88 StartY=11 StartZ=0 EndX=-88 EndY=-11 EndZ=0
    g7: LineSegment StartX=-88 StartY=-11 StartZ=0 EndX=-58 EndY=-11 EndZ=0
    g8: LineSegment StartX=-58 StartY=-11 StartZ=0 EndX=-58 EndY=-9 EndZ=0
    g9: LineSegment StartX=-85.5 StartY=8 StartZ=0 EndX=-85.5 EndY=-8 EndZ=0
    g10: LineSegment StartX=-84.5 StartY=-9 StartZ=0 EndX=-77.5 EndY=-9 EndZ=0
    g11: LineSegment StartX=-58 StartY=9 StartZ=0 EndX=-59.5 EndY=9 EndZ=0
    g12: LineSegment StartX=-58 StartY=11 StartZ=0 EndX=-58 EndY=9 EndZ=0
    g13: LineSegment StartX=-63.5 StartY=-8 StartZ=0 EndX=-63.5 EndY=-3.5 EndZ=0
    g14: LineSegment StartX=-64.5 StartY=-2.5 StartZ=0 EndX=-68.9 EndY=-2.5 EndZ=0
    g15: LineSegment StartX=-69.9 StartY=-1.5 StartZ=0 EndX=-69.9 EndY=1.5 EndZ=0
    g16: LineSegment StartX=-68.9 StartY=2.5 StartZ=0 EndX=-64.5 EndY=2.5 EndZ=0
    g17: LineSegment StartX=-63.5 StartY=3.5 StartZ=0 EndX=-63.5 EndY=8 EndZ=0
    g18: LineSegment StartX=-60.5 StartY=8 StartZ=0 EndX=-60.5 EndY=-8 EndZ=0
    g19: LineSegment StartX=-64.5 StartY=9 StartZ=0 EndX=-71.5 EndY=9 EndZ=0
    g20: LineSegment StartX=-59.5 StartY=-9 StartZ=0 EndX=-58 EndY=-9 EndZ=0
    g21: ArcOfCircle CenterX=-59.5 CenterY=8 CenterZ=0 NormalX=0 NormalY=0 NormalZ=1 AngleXU=0 Radius=1 StartAngle=1.5708 EndAngle=3.14159
    g22: GeomPoint [constr] X=-60.5 Y=9 Z=0
    g23: ArcOfCircle CenterX=-59.5 CenterY=-8 CenterZ=0 NormalX=0 NormalY=0 NormalZ=1 AngleXU=0 Radius=1 StartAngle=3.14159 EndAngle=4.71239
    g24: GeomPoint [constr] X=-60.5 Y=-9 Z=0
    g25: ArcOfCircle CenterX=-64.5 CenterY=-8 CenterZ=0 NormalX=0 NormalY=0 NormalZ=1 AngleXU=0 Radius=1 StartAngle=4.71239 EndAngle=6.28319
    g26: GeomPoint [constr] X=-63.5 Y=-9 Z=0
    g27: ArcOfCircle CenterX=-64.5 CenterY=-3.5 CenterZ=0 NormalX=0 NormalY=0 NormalZ=1 AngleXU=0 Radius=1 StartAngle=0 EndAngle=1.5708
    g28: GeomPoint [constr] X=-63.5 Y=-2.5 Z=0
    g29: ArcOfCircle CenterX=-64.5 CenterY=3.5 CenterZ=0 NormalX=0 NormalY=0 NormalZ=1 AngleXU=0 Radius=1 StartAngle=4.71239 EndAngle=6.28319
    g30: GeomPoint [constr] X=-63.5 Y=2.5 Z=0
    g31: ArcOfCircle CenterX=-84.5 CenterY=8 CenterZ=0 NormalX=0 NormalY=0 NormalZ=1 AngleXU=0 Radius=1 StartAngle=1.5708 EndAngle=3.14159
    g32: GeomPoint [constr] X=-85.5 Y=9 Z=0
    g33: ArcOfCircle CenterX=-84.5 CenterY=-8 CenterZ=0 NormalX=0 NormalY=0 NormalZ=1 AngleXU=0 Radius=1 StartAngle=3.14159 EndAngle=4.71239
    g34: GeomPoint [constr] X=-85.5 Y=-9 Z=0
    g35: LineSegment StartX=-76.5 StartY=8 StartZ=0 EndX=-76.5 EndY=6.6 EndZ=0
    g36: LineSegment StartX=-75.5 StartY=5.6 StartZ=0 EndX=-73.5 EndY=5.6 EndZ=0
    g37: LineSegment StartX=-72.5 StartY=6.6 StartZ=0 EndX=-72.5 EndY=8 EndZ=0
    g38: LineSegment StartX=-76.5 StartY=-8 StartZ=0 EndX=-76.5 EndY=-6.6 EndZ=0
    g39: LineSegment StartX=-75.5 StartY=-5.6 StartZ=0 EndX=-73.5 EndY=-5.6 EndZ=0
    g40: LineSegment StartX=-72.5 StartY=-6.6 StartZ=0 EndX=-72.5 EndY=-8 EndZ=0
    g41: LineSegment StartX=-71.5 StartY=-9 StartZ=0 EndX=-64.5 EndY=-9 EndZ=0
    g42: LineSegment StartX=-77.5 StartY=9 StartZ=0 EndX=-84.5 EndY=9 EndZ=0
    g43: ArcOfCircle CenterX=-71.5 CenterY=8 CenterZ=0 NormalX=0 NormalY=0 NormalZ=1 AngleXU=0 Radius=1 StartAngle=1.5708 EndAngle=3.14159
    g44: GeomPoint [constr] X=-72.5 Y=9 Z=0
    g45: ArcOfCircle CenterX=-73.5 CenterY=6.6 CenterZ=0 NormalX=0 NormalY=0 NormalZ=1 AngleXU=0 Radius=1 StartAngle=4.71239 EndAngle=6.28319
    g46: GeomPoint [constr] X=-72.5 Y=5.6 Z=0
    g47: ArcOfCircle CenterX=-75.5 CenterY=6.6 CenterZ=0 NormalX=0 NormalY=0 NormalZ=1 AngleXU=0 Radius=1 StartAngle=3.14159 EndAngle=4.71239
    g48: GeomPoint [constr] X=-76.5 Y=5.6 Z=0
    g49: ArcOfCircle CenterX=-77.5 CenterY=8 CenterZ=0 NormalX=0 NormalY=0 NormalZ=1 AngleXU=0 Radius=1 StartAngle=0 EndAngle=1.5708
    g50: GeomPoint [constr] X=-76.5 Y=9 Z=0
    g51: ArcOfCircle CenterX=-71.5 CenterY=-8 CenterZ=0 NormalX=0 NormalY=0 NormalZ=1 AngleXU=0 Radius=1 StartAngle=3.14159 EndAngle=4.71239
    g52: GeomPoint [constr] X=-72.5 Y=-9 Z=0
    g53: ArcOfCircle CenterX=-73.5 CenterY=-6.6 CenterZ=0 NormalX=0 NormalY=0 NormalZ=1 AngleXU=0 Radius=1 StartAngle=0 EndAngle=1.5708
    g54: GeomPoint [constr] X=-72.5 Y=-5.6 Z=0
    g55: ArcOfCircle CenterX=-75.5 CenterY=-6.6 CenterZ=0 NormalX=0 NormalY=0 NormalZ=1 AngleXU=0 Radius=1 StartAngle=1.5708 EndAngle=3.14159
    g56: GeomPoint [constr] X=-76.5 Y=-5.6 Z=0
    g57: ArcOfCircle CenterX=-77.5 CenterY=-8 CenterZ=0 NormalX=0 NormalY=0 NormalZ=1 AngleXU=0 Radius=1 StartAngle=4.71239 EndAngle=6.28319
    g58: GeomPoint [constr] X=-76.5 Y=-9 Z=0
    g59: ArcOfCircle CenterX=-64.5 CenterY=8 CenterZ=0 NormalX=0 NormalY=0 NormalZ=1 AngleXU=0 Radius=1 StartAngle=0 EndAngle=1.5708
    g60: GeomPoint [constr] X=-63.5 Y=9 Z=0
    g61: ArcOfCircle CenterX=-68.9 CenterY=1.5 CenterZ=0 NormalX=0 NormalY=0 NormalZ=1 AngleXU=0 Radius=1 StartAngle=1.5708 EndAngle=3.14159
    g62: GeomPoint [constr] X=-69.9 Y=2.5 Z=0
    g63: ArcOfCircle CenterX=-68.9 CenterY=-1.5 CenterZ=0 NormalX=0 NormalY=0 NormalZ=1 AngleXU=0 Radius=1 StartAngle=3.14159 EndAngle=4.71239
    g64: GeomPoint [constr] X=-69.9 Y=-2.5 Z=0
  constraints (154):
    c: Coincident(g0,g1)
    c: Coincident(g1,g2)
    c: Coincident(g2,g3)
    c: Coincident(g3,g0)
    c: Vertical(g0)
    c: Vertical(g2)
    c: Horizontal(g1)
    c: Horizontal(g3)
    c: Distance(g0,g2) = 70
    c: Symmetric(g0,g2,g-1)
    c: DistanceY(g0,g0) = 12
    c: Diameter(g4) = 5.6
    c: Coincident(g4,g-1)
    c: Coincident(g5,g6)
    c: Coincident(g6,g7)
    c: Coincident(g7,g8)
    c: Horizontal(g5)
    c: Horizontal(g7)
    c: Vertical(g8)
    c: Symmetric(g6,g5,g-1)
    c: DistanceX(g5) = -58
    c: DistanceX(g5,g5) = 30
    c: Vertical(g9)
    c: Horizontal(g10)
    c: Horizontal(g11)
    c: Coincident(g8,g20)
    c: Coincident(g12,g5)
    c: Coincident(g12,g11)
    c: Vertical(g12)
    c: DistanceX(g34) = -85.5
    c: Vertical(g13)
    c: Horizontal(g14)
    c: Horizontal(g16)
    c: Vertical(g17)
    c: Vertical(g18)
    c: PointOnObject(g22,g11)
    c: PointOnObject(g22,g18)
    c: Tangent(g11,g21) = -1.5708
    c: Tangent(g18,g21) = -1.5708
    c: Horizontal(g20)
    c: Horizontal(g26,g24)
    c: PointOnObject(g24,g18)
    c: PointOnObject(g24,g20)
    c: Tangent(g18,g23) = -1.5708
    c: Tangent(g20,g23) = -1.5708
    c: PointOnObject(g26,g41)
    c: PointOnObject(g26,g13)
    c: Coincident(g41,g25) = -1.5708
    c: Tangent(g13,g25) = -1.5708
    c: PointOnObject(g28,g13)
    c: PointOnObject(g28,g14)
    c: Tangent(g13,g27) = -1.5708
    c: Tangent(g14,g27) = -1.5708
    c: PointOnObject(g30,g16)
    c: PointOnObject(g30,g17)
    c: Tangent(g16,g29) = -1.5708
    c: Tangent(g17,g29) = -1.5708
    c: PointOnObject(g32,g9)
    c: PointOnObject(g32,g42)
    c: Tangent(g9,g31) = -1.5708
    c: PointOnObject(g34,g9)
    c: PointOnObject(g34,g10)
    c: Tangent(g9,g33) = -1.5708
    c: Tangent(g10,g33) = -1.5708
    c: Vertical(g35)
    c: Horizontal(g36)
    c: Vertical(g37)
    c: Vertical(g38)
    c: Horizontal(g39)
    c: Vertical(g40)
    c: PointOnObject(g44,g19)
    c: PointOnObject(g44,g37)
    c: Tangent(g19,g43) = -1.5708
    c: Tangent(g37,g43) = 1.5708
    c: PointOnObject(g46,g36)
    c: PointOnObject(g46,g37)
    c: Tangent(g36,g45) = -1.5708
    c: Tangent(g37,g45) = -1.5708
    c: PointOnObject(g48,g35)
    c: PointOnObject(g48,g36)
    c: Tangent(g35,g47) = -1.5708
    c: Tangent(g36,g47) = -1.5708
    c: PointOnObject(g50,g35)
    c: PointOnObject(g50,g42)
    c: Tangent(g35,g49) = 1.5708
    c: Tangent(g42,g49) = -1.5708
    c: PointOnObject(g52,g40)
    c: PointOnObject(g52,g41)
    c: Tangent(g40,g51) = -1.5708
    c: Tangent(g41,g51) = -1.5708
    c: PointOnObject(g54,g39)
    c: PointOnObject(g54,g40)
    c: Tangent(g39,g53) = 1.5708
    c: Tangent(g40,g53) = 1.5708
    c: PointOnObject(g56,g38)
    c: PointOnObject(g56,g39)
    c: Tangent(g38,g55) = 1.5708
    c: Tangent(g39,g55) = 1.5708
    c: PointOnObject(g58,g10)
    c: PointOnObject(g58,g38)
    c: Tangent(g10,g57) = -1.5708
    c: Tangent(g38,g57) = -1.5708
    c: Equal(g57,g55)
    c: Equal(g55,g53)
    c: Equal(g53,g51)
    c: Equal(g51,g25)
    c: Equal(g25,g27)
    c: Equal(g27,g29)
    c: Equal(g29,g43)
    c: Equal(g43,g45)
    c: Equal(g45,g47)
    c: Equal(g47,g49)
    c: Equal(g49,g23)
    c: Equal(g23,g21)
    c: Horizontal(g22,g60)
    c: Horizontal(g19)
    c: Horizontal(g42)
    c: Horizontal(g41)
    c: Horizontal(g58,g52)
    c: PointOnObject(g60,g17)
    c: PointOnObject(g60,g19)
    c: Tangent(g17,g59) = -1.5708
    c: Tangent(g19,g59) = -1.5708
    c: Equal(g59,g21)
    c: PointOnObject(g62,g15)
    c: PointOnObject(g62,g16)
    c: Tangent(g15,g61) = 1.5708
    c: Tangent(g16,g61) = 1.5708
    c: PointOnObject(g64,g14)
    c: PointOnObject(g64,g15)
    c: Tangent(g14,g63) = 1.5708
    c: Tangent(g15,g63) = 1.5708
    c: Equal(g63,g61)
    c: Equal(g61,g45)
    c: Horizontal(g44,g50)
    c: Symmetric(g63,g61,g-1)
    c: DistanceX(g17,g18) = 3
    c: DistanceX(g35,g37) = 4
    c: Equal(g42,g19)
    c: Vertical(g55,g47)
    c: Equal(g19,g41)
    c: Equal(g13,g17)
    c: DistanceY(g36) = 5.6
    c: Symmetric(g39,g36,g-1)
    c: DistanceY(g8) = -9
    c: Radius(g31) = 1
    c: Tangent(g42,g31) = -1.5708
    c: Equal(g31,g49)
    c: Equal(g33,g31)
    c: DistanceY(g8,g8) = 2
    c: DistanceX(g9,g17) = 22
    c: Vertical(g8,g11)
    c: DistanceX(g9,g15) = 15.6
    c: DistanceY(g14,g16) = 5
FEATURE [PartDesign::Pad] Pad019  label="PadUSBAkkuSteg"
  BaseFeature = -> Pocket003
  Direction = (0,0,1)
  Length = 8
  Length2 = 10
  Profile = -> Sketch030
  ReferenceAxis = -> Sketch030 [N_Axis]
  Refine = true
  Suppressed = false
  Type = 0
FEATURE [Sketcher::SketchObject] Sketch031
  ArcFitTolerance = 1e-06
  AttachmentSupport = -> [YZ_Plane012]
  FullyConstrained = true
  MakeInternals = false
  MapMode = 5
  Placement = pos=(0,0,0) rot=(0.57735,0.57735,0.57735;2.0944rad)
  sketch-geometry (14):
    g0: LineSegment StartX=57.25 StartY=0 StartZ=0 EndX=57.25 EndY=5.5 EndZ=0
    g1: LineSegment StartX=38.75 StartY=0 StartZ=0 EndX=38.75 EndY=5.5 EndZ=0
    g2: LineSegment StartX=57.25 StartY=0 StartZ=0 EndX=59.25 EndY=0 EndZ=0
    g3: LineSegment StartX=59.25 StartY=0 StartZ=0 EndX=59.25 EndY=5.5 EndZ=0
    g4: LineSegment StartX=36.75 StartY=5.5 StartZ=0 EndX=34.75 EndY=0 EndZ=0
    g5: LineSegment StartX=34.75 StartY=0 StartZ=0 EndX=38.75 EndY=0 EndZ=0
    g6: ArcOfCircle CenterX=48 CenterY=5.5 CenterZ=0 NormalX=0 NormalY=0 NormalZ=1 AngleXU=0 Radius=9.25 StartAngle=2.35619 EndAngle=3.14159
    g7: ArcOfCircle CenterX=48 CenterY=5.5 CenterZ=0 NormalX=0 NormalY=0 NormalZ=1 AngleXU=0 Radius=9.25 StartAngle=0 EndAngle=0.785398
    g8: ArcOfCircle CenterX=48 CenterY=5.5 CenterZ=0 NormalX=0 NormalY=0 NormalZ=1 AngleXU=0 Radius=11.25 StartAngle=0 EndAngle=0.785398
    g9: ArcOfCircle CenterX=48 CenterY=5.5 CenterZ=0 NormalX=0 NormalY=0 NormalZ=1 AngleXU=0 Radius=11.25 StartAngle=2.35619 EndAngle=3.14159
    g10: LineSegment StartX=40.045 StartY=13.455 StartZ=0 EndX=41.4593 EndY=12.0407 EndZ=0
    g11: LineSegment StartX=54.5407 StartY=12.0407 StartZ=0 EndX=45.3483 EndY=21.2331 EndZ=0
    g12: LineSegment StartX=45.3483 StartY=21.2331 StartZ=0 EndX=46.7626 EndY=22.6473 EndZ=0
    g13: LineSegment StartX=46.7626 StartY=22.6473 StartZ=0 EndX=55.955 EndY=13.455 EndZ=0
  constraints (39):
    c: PointOnObject(g0,g-1)
    c: Tangent(g0,g7) = -1.5708
    c: Horizontal(g1,g0)
    c: Vertical(g0)
    c: DistanceX(g1,g0) = 18.5
    c: Coincident(g1,g6)
    c: Vertical(g1)
    c: DistanceY(g7) = 5.5
    c: DistanceX(g7) = 48
    c: Coincident(g0,g2)
    c: PointOnObject(g2,g-1)
    c: Coincident(g2,g3)
    c: Vertical(g3)
    c: Tangent(g3,g8) = -1.5708
    c: Coincident(g9,g4)
    c: PointOnObject(g4,g-1)
    c: Coincident(g4,g5)
    c: Coincident(g5,g1)
    c: DistanceX(g2,g2) = 2
    c: Coincident(g8,g7)
    c: Horizontal(g6,g3)
    c: DistanceX(g9,g6) = 2
    c: Coincident(g7,g6)
    c: Equal(g8,g9)
    c: Equal(g6,g7)
    c: Coincident(g6,g9)
    c: Coincident(g10,g9)
    c: Coincident(g10,g6)
    c: Perpendicular(g6,g10)
    c: Horizontal(g6,g7)
    c: Tangent(g7,g11) = -1.5708
    c: Coincident(g11,g12)
    c: Coincident(g12,g13)
    c: Angle(g11,g-1) = 0.785398
    c: Parallel(g13,g11)
    c: Tangent(g13,g8) = 1.5708
    c: DistanceX(g5,g5) = 4
    c: Distance(g11,g11) = 13
    c: Perpendicular(g13,g12)
FEATURE [PartDesign::Pad] Pad020  label="PadYZAkku"
  BaseFeature = -> Pad019
  Direction = (1,0,0)
  Length = 33
  Length2 = 10
  Midplane = true
  Profile = -> Sketch031
  ReferenceAxis = -> Sketch031 [N_Axis]
  Refine = true
  Suppressed = false
  Type = 0
FEATURE [Sketcher::SketchObject] Sketch032
  ArcFitTolerance = 1e-06
  AttachmentSupport = -> [XZ_Plane012]
  FullyConstrained = false
  MakeInternals = false
  MapMode = 5
  Placement = pos=(0,0,0) rot=(1,0,0;1.5708rad)
  sketch-geometry (16):
    g0: LineSegment StartX=-79.4871 StartY=15.1925 StartZ=0 EndX=-62.5 EndY=25 EndZ=0
    g1: LineSegment StartX=-79.4871 StartY=15.1925 StartZ=0 EndX=-77.7551 EndY=18.1925 EndZ=0
    g2: LineSegment StartX=-77.7551 StartY=18.1925 StartZ=0 EndX=-62.5 EndY=27 EndZ=0
    g3: LineSegment StartX=-62.5 StartY=27 StartZ=0 EndX=-62.5 EndY=25 EndZ=0
    g4: LineSegment StartX=-58.3 StartY=42.4629 StartZ=0 EndX=-55.5831 EndY=42.4629 EndZ=0
    g5: LineSegment StartX=-55.5831 StartY=42.4629 StartZ=0 EndX=-50.933 EndY=24.6909 EndZ=0
    g6: LineSegment StartX=-50.933 StartY=24.6909 StartZ=0 EndX=-58.3 EndY=24.6909 EndZ=0
    g7: LineSegment StartX=-58.3 StartY=24.6909 StartZ=0 EndX=-58.3 EndY=42.4629 EndZ=0
    g8: LineSegment StartX=-76.023 StartY=21.1925 StartZ=0 EndX=-74.291 EndY=24.1925 EndZ=0
    g9: LineSegment StartX=-74.291 StartY=24.1925 StartZ=0 EndX=-62.5 EndY=31 EndZ=0
    g10: LineSegment StartX=-62.5 StartY=31 StartZ=0 EndX=-62.5 EndY=29 EndZ=0
    g11: LineSegment StartX=-62.5 StartY=29 StartZ=0 EndX=-76.023 EndY=21.1925 EndZ=0
    g12: LineSegment StartX=-72.5589 StartY=27.1925 StartZ=0 EndX=-70.8269 EndY=30.1925 EndZ=0
    g13: LineSegment StartX=-70.8269 StartY=30.1925 StartZ=0 EndX=-62.5 EndY=35 EndZ=0
    g14: LineSegment StartX=-62.5 StartY=35 StartZ=0 EndX=-62.5 EndY=33 EndZ=0
    g15: LineSegment StartX=-62.5 StartY=33 StartZ=0 EndX=-72.5589 EndY=27.1925 EndZ=0
  constraints (41):
    c: DistanceY(g0) = 25
    c: Angle(g-1,g0) = 0.523599
    c: Coincident(g1,g0)
    c: Coincident(g1,g2)
    c: Parallel(g2,g0)
    c: Coincident(g3,g2)
    c: Coincident(g3,g0)
    c: Vertical(g3)
    c: DistanceY(g3,g3) = 2
    c: DistanceX(g2) = -62.5
    c: Coincident(g4,g5)
    c: Coincident(g5,g6)
    c: Coincident(g6,g7)
    c: Coincident(g7,g4)
    c: Vertical(g7)
    c: Horizontal(g6)
    c: Horizontal(g4)
    c: DistanceX(g4) = -58.3
    c: Coincident(g8,g9)
    c: Coincident(g9,g10)
    c: Vertical(g10)
    c: Coincident(g10,g11)
    c: Coincident(g11,g8)
    c: Parallel(g11,g9)
    c: Parallel(g11,g2)
    c: DistanceY(g10,g10) = 2
    c: Coincident(g12,g13)
    c: Coincident(g13,g14)
    c: Vertical(g14)
    c: Coincident(g14,g15)
    c: Coincident(g15,g12)
    c: Parallel(g13,g15)
    c: Parallel(g15,g9)
    c: DistanceY(g14,g14) = 2
    c: DistanceY(g9,g14) = 2
    c: DistanceY(g2,g10) = 2
    c: Tangent(g1,g8)
    c: Tangent(g12,g8)
    c: Angle(g0,g1) = 0.523599
    c: Vertical(g14,g9)
    c: Vertical(g10,g2)
FEATURE [PartDesign::Pad] Pad021  label="PadESPMount"
  BaseFeature = -> Pad020
  Direction = (0,-1,2e-16)
  Length = 9
  Length2 = 10
  Midplane = true
  Profile = -> Sketch032
  ReferenceAxis = -> Sketch032 [N_Axis]
  Refine = true
  Suppressed = false
  Type = 0
FEATURE [PartDesign::SubShapeBinder] Binder016  label="BinderEncoder"
  BindCopyOnChange = 0
  BindMode = 0
  ClaimChildren = false
  Context = -> Body012 [Binder016.]
  Fuse = false
  MakeFace = true
  OffsetFill = false
  OffsetIntersection = false
  OffsetJoinType = 0
  OffsetOpenResult = false
  PartialLoad = false
  Refine = true
  Relative = true
  Support = -> [Link006[Pad012.Face18]]
  _Version = 2
FEATURE [Sketcher::SketchObject] Sketch033
  ArcFitTolerance = 1e-06
  AttachmentSupport = -> [YZ_Plane012]
  FullyConstrained = true
  MakeInternals = false
  MapMode = 5
  Placement = pos=(0,0,0) rot=(0.57735,0.57735,0.57735;2.0944rad)
  sketch-geometry (4):
    g0: LineSegment StartX=-73.5 StartY=0 StartZ=0 EndX=-52.2 EndY=36.8927 EndZ=0
    g1: LineSegment StartX=-88.3 StartY=0 StartZ=0 EndX=-73.5 EndY=0 EndZ=0
    g2: LineSegment StartX=-88.3 StartY=0 StartZ=0 EndX=-63.3 EndY=43.3013 EndZ=0
    g3: LineSegment StartX=-63.3 StartY=43.3013 StartZ=0 EndX=-52.2 EndY=36.8927 EndZ=0
  constraints (12):
    c: PointOnObject(g1,g-1)
    c: Coincident(g1,g0)
    c: Horizontal(g1)
    c: Coincident(g2,g1)
    c: Angle(g1,g2) = 1.0472
    c: Coincident(g3,g0)
    c: Perpendicular(g0,g3)
    c: DistanceX(g0) = -73.5
    c: DistanceX(g1,g1) = 14.8
    c: Coincident(g2,g3)
    c: Distance(g2,g2) = 50
    c: Parallel(g0,g2)
FEATURE [PartDesign::Pad] Pad022  label="PadEncoderBlock"
  BaseFeature = -> Pad021
  Direction = (1,0,0)
  Length = 28
  Length2 = 10
  Midplane = true
  Profile = -> Sketch033
  ReferenceAxis = -> Sketch033 [N_Axis]
  Refine = true
  Suppressed = false
  Type = 0
FEATURE [PartDesign::SubShapeBinder] Binder017  label="BinderDisplay"
  BindCopyOnChange = 0
  BindMode = 0
  ClaimChildren = false
  Context = -> Body012 [Binder017.]
  Fuse = false
  MakeFace = true
  OffsetFill = false
  OffsetIntersection = false
  OffsetJoinType = 0
  OffsetOpenResult = false
  PartialLoad = false
  Refine = true
  Relative = true
  _Version = 2
FEATURE [PartDesign::SubShapeBinder] Binder018
  BindCopyOnChange = 0
  BindMode = 0
  ClaimChildren = false
  Context = -> Body012 [Binder018.]
  Fuse = false
  MakeFace = true
  OffsetFill = false
  OffsetIntersection = false
  OffsetJoinType = 0
  OffsetOpenResult = false
  PartialLoad = false
  Refine = true
  Relative = true
  Support = -> [CompoundFilter[Face16]]
  _Version = 2
FEATURE [PartDesign::SubShapeBinder] Binder019
  BindCopyOnChange = 0
  BindMode = 0
  ClaimChildren = false
  Context = -> Body012 [Binder019.]
  Fuse = false
  MakeFace = true
  OffsetFill = false
  OffsetIntersection = false
  OffsetJoinType = 0
  OffsetOpenResult = false
  PartialLoad = false
  Refine = true
  Relative = true
  Support = -> [Link002[Pad022.]]
  _Version = 2
FEATURE [PartDesign::SubShapeBinder] Binder021  label="BinderAkku"
  BindCopyOnChange = 0
  BindMode = 0
  ClaimChildren = false
  Context = -> Body012 [Binder021.]
  Fuse = false
  MakeFace = true
  OffsetFill = false
  OffsetIntersection = false
  OffsetJoinType = 0
  OffsetOpenResult = false
  PartialLoad = false
  Refine = true
  Relative = true
  Support = -> [Link004[Pad.]]
  _Version = 2
FEATURE [PartDesign::SubShapeBinder] Binder022  label="BinderESP"
  BindCopyOnChange = 0
  BindMode = 0
  ClaimChildren = false
  Context = -> Body012 [Binder022.]
  Fuse = false
  MakeFace = true
  OffsetFill = false
  OffsetIntersection = false
  OffsetJoinType = 0
  OffsetOpenResult = false
  PartialLoad = false
  Refine = true
  Relative = true
  Support = -> [Link005[Pad032.]]
  _Version = 2
FEATURE [PartDesign::SubShapeBinder] Binder023  label="BinderLC"
  BindCopyOnChange = 0
  BindMode = 0
  ClaimChildren = false
  Context = -> Body012 [Boolean005.Binder023.]
  Fuse = false
  MakeFace = true
  OffsetFill = false
  OffsetIntersection = false
  OffsetJoinType = 0
  OffsetOpenResult = false
  PartialLoad = false
  Refine = true
  Relative = true
  Support = -> [Link]
  _Version = 2
FEATURE [PartDesign::SubShapeBinder] Binder024  label="BinderEnc"
  BindCopyOnChange = 0
  BindMode = 0
  ClaimChildren = false
  Context = -> Body012 [Binder024.]
  Fuse = false
  MakeFace = true
  OffsetFill = false
  OffsetIntersection = false
  OffsetJoinType = 0
  OffsetOpenResult = false
  PartialLoad = false
  Refine = true
  Relative = true
  Support = -> [Link006[Pad012.]]
  _Version = 2
FEATURE [PartDesign::SubShapeBinder] Binder025
  BindCopyOnChange = 0
  BindMode = 0
  ClaimChildren = false
  Context = -> Body013 [Binder025.]
  Fuse = false
  MakeFace = true
  OffsetFill = false
  OffsetIntersection = false
  OffsetJoinType = 0
  OffsetOpenResult = false
  PartialLoad = false
  Refine = true
  Relative = true
  Support = -> [Link006[Pad012.Edge49]]
  _Version = 2
FEATURE [Sketcher::SketchObject] Sketch036
  ArcFitTolerance = 1e-06
  AttachmentOffset = pos=(0,0,-2) rot=(0,0,1;0rad)
  AttachmentSupport = -> [Binder025]
  ExternalGeometry = -> [Binder025]
  FullyConstrained = true
  MakeInternals = false
  MapMode = 5
  Placement = pos=(2.76483e-06,-56.8113,32.8) rot=(0,0.866025,0.5;3.14159rad)
  sketch-geometry (1):
    g0: Circle CenterX=4.85576e-06 CenterY=-20.5703 CenterZ=0 NormalX=0 NormalY=0 NormalZ=1 AngleXU=0 Radius=12.75
  constraints (2):
    c: Diameter(g0) = 25.5
    c: Coincident(g0,g-3)
FEATURE [PartDesign::Pad] Pad025
  Direction = (-4.21469e-08,0.866026,-0.5)
  Length = 30
  Length2 = 10
  Profile = -> Sketch036
  ReferenceAxis = -> Sketch036 [N_Axis]
  Refine = true
  Reversed = true
  Suppressed = false
  Type = 0
FEATURE [PartDesign::Body] Body013  label="base_button_cut"
  AllowCompound = false
  Group = -> [Binder025,Sketch036,Pad025]
  Origin = -> Origin013
  Tip = -> Pad025
FEATURE [PartDesign::SubShapeBinder] Binder026  label="BinderEnc2"
  BindCopyOnChange = 0
  BindMode = 0
  ClaimChildren = false
  Context = -> Body012 [Binder026.]
  Fuse = false
  MakeFace = true
  OffsetFill = false
  OffsetIntersection = false
  OffsetJoinType = 0
  OffsetOpenResult = false
  PartialLoad = false
  Refine = true
  Relative = true
  Support = -> [Body013[Pad025.]]
  _Version = 2
FEATURE [Sketcher::SketchObject] Sketch037
  ArcFitTolerance = 1e-06
  AttachmentOffset = pos=(0,0,0) rot=(0,0,1;-1.5708rad)
  AttachmentSupport = -> [XY_Plane010]
  FullyConstrained = true
  MakeInternals = false
  MapMode = 5
  Placement = pos=(0,0,0) rot=(0,0,1;4.71239rad)
  sketch-geometry (18):
    g0: LineSegment StartX=-30 StartY=39.5 StartZ=0 EndX=-30 EndY=-39.5 EndZ=0
    g1: LineSegment StartX=-27 StartY=-42.5 StartZ=0 EndX=27 EndY=-42.5 EndZ=0
    g2: LineSegment StartX=30 StartY=-39.5 StartZ=0 EndX=30 EndY=39.5 EndZ=0
    g3: LineSegment StartX=27 StartY=42.5 StartZ=0 EndX=11 EndY=42.5 EndZ=0
    g4: ArcOfCircle CenterX=-27 CenterY=39.5 CenterZ=0 NormalX=0 NormalY=0 NormalZ=1 AngleXU=0 Radius=3 StartAngle=1.5708 EndAngle=3.14159
    g5: ArcOfCircle CenterX=-27 CenterY=-39.5 CenterZ=0 NormalX=0 NormalY=0 NormalZ=1 AngleXU=0 Radius=3 StartAngle=3.14159 EndAngle=4.71239
    g6: ArcOfCircle CenterX=27 CenterY=-39.5 CenterZ=0 NormalX=0 NormalY=0 NormalZ=1 AngleXU=0 Radius=3 StartAngle=4.71239 EndAngle=6.28319
    g7: ArcOfCircle CenterX=27 CenterY=39.5 CenterZ=0 NormalX=0 NormalY=0 NormalZ=1 AngleXU=0 Radius=3 StartAngle=-9e-16 EndAngle=1.5708
    g8: GeomPoint [constr] X=30 Y=-42.5 Z=0
    g9: GeomPoint [constr] X=0 Y=0 Z=0
    g10: LineSegment StartX=-6 StartY=47.5 StartZ=0 EndX=-6 EndY=62.5 EndZ=0
    g11: ArcOfCircle CenterX=-3 CenterY=62.5 CenterZ=0 NormalX=0 NormalY=0 NormalZ=1 AngleXU=0 Radius=3 StartAngle=1.5708 EndAngle=3.14159
    g12: LineSegment StartX=-3 StartY=65.5 StartZ=0 EndX=3 EndY=65.5 EndZ=0
    g13: ArcOfCircle CenterX=3 CenterY=62.5 CenterZ=0 NormalX=0 NormalY=0 NormalZ=1 AngleXU=0 Radius=3 StartAngle=1.1e-15 EndAngle=1.5708
    g14: LineSegment StartX=6 StartY=62.5 StartZ=0 EndX=6 EndY=47.5 EndZ=0
    g15: ArcOfCircle CenterX=11 CenterY=47.5 CenterZ=0 NormalX=0 NormalY=0 NormalZ=1 AngleXU=0 Radius=5 StartAngle=3.14159 EndAngle=4.71239
    g16: LineSegment StartX=-11 StartY=42.5 StartZ=0 EndX=-27 EndY=42.5 EndZ=0
    g17: ArcOfCircle CenterX=-11 CenterY=47.5 CenterZ=0 NormalX=0 NormalY=0 NormalZ=1 AngleXU=0 Radius=5 StartAngle=4.71239 EndAngle=6.28319
  constraints (42):
    c: Tangent(g0,g4) = -1.5708
    c: Tangent(g0,g5) = -1.5708
    c: Tangent(g1,g5) = -1.5708
    c: Tangent(g1,g6) = -1.5708
    c: Tangent(g2,g6) = -1.5708
    c: Tangent(g2,g7) = -1.5708
    c: Tangent(g3,g7) = -1.5708
    c: Vertical(g0)
    c: Vertical(g2)
    c: Horizontal(g1)
    c: Horizontal(g3)
    c: Equal(g4,g5)
    c: Equal(g5,g6)
    c: Equal(g6,g7)
    c: Symmetric(g2,g0,g9)
    c: PointOnObject(g8,g1)
    c: PointOnObject(g8,g2)
    c: Coincident(g9,g-1)
    c: Radius(g6) = 3
    c: DistanceY(g1,g16) = 85
    c: DistanceX(g0,g2) = 60
    c: Vertical(g10)
    c: Tangent(g10,g11) = 1.5708
    c: Tangent(g11,g12) = 1.5708
    c: Tangent(g12,g13) = 1.5708
    c: Tangent(g13,g14) = 1.5708
    c: Tangent(g14,g15) = -1.5708
    c: Tangent(g10,g17) = -1.5708
    c: Vertical(g14)
    c: Horizontal(g12)
    c: Equal(g11,g13)
    c: Tangent(g3,g15) = 1.5708
    c: Horizontal(g3,g16)
    c: Horizontal(g16)
    c: DistanceX(g10,g13) = 12
    c: Equal(g16,g3)
    c: DistanceY(g14,g14) = 15
    c: Tangent(g17,g16) = 1.5708
    c: Tangent(g16,g4) = -1.5708
    c: Equal(g15,g17)
    c: Radius(g17) = 5
    c: Equal(g13,g7)
FEATURE [PartDesign::FeatureBase] BaseFeature001
  BaseFeature = -> CompoundFilter
  Suppressed = false
FEATURE [PartDesign::SubShapeBinder] Binder027
  BindCopyOnChange = 0
  BindMode = 0
  ClaimChildren = false
  Context = -> Body014 [Binder027.]
  Fuse = false
  MakeFace = true
  OffsetFill = false
  OffsetIntersection = false
  OffsetJoinType = 0
  OffsetOpenResult = false
  PartialLoad = false
  Refine = true
  Relative = true
  Support = -> [Link002[Pad022.]]
  _Version = 2
FEATURE [PartDesign::SubShapeBinder] Binder028
  BindCopyOnChange = 0
  BindMode = 0
  ClaimChildren = false
  Context = -> Body014 [Binder028.]
  Fuse = false
  MakeFace = true
  OffsetFill = false
  OffsetIntersection = false
  OffsetJoinType = 0
  OffsetOpenResult = false
  PartialLoad = false
  Refine = true
  Relative = true
  Support = -> [Body013]
  _Version = 2
FEATURE [PartDesign::Boolean] Boolean009  label="BooleanEncoder"
  BaseFeature = -> BaseFeature001
  Group = -> [Binder028]
  Refine = true
  Suppressed = false
  Type = 1
  UsePlacement = true
FEATURE [PartDesign::SubShapeBinder] Binder029
  BindCopyOnChange = 0
  BindMode = 0
  ClaimChildren = false
  Context = -> Body010 [Binder029.]
  Fuse = false
  MakeFace = true
  OffsetFill = false
  OffsetIntersection = false
  OffsetJoinType = 0
  OffsetOpenResult = false
  PartialLoad = false
  Refine = true
  Relative = true
  Support = -> [Link005[Pad032.]]
  _Version = 2
FEATURE [Sketcher::SketchObject] Sketch038
  ArcFitTolerance = 1e-06
  AttachmentSupport = -> [XY_Plane010]
  FullyConstrained = true
  MakeInternals = false
  MapMode = 5
  sketch-geometry (5):
    g0: LineSegment StartX=-20 StartY=85.5 StartZ=0 EndX=-20 EndY=65.5 EndZ=0
    g1: LineSegment StartX=-20 StartY=65.5 StartZ=0 EndX=20 EndY=65.5 EndZ=0
    g2: LineSegment StartX=20 StartY=65.5 StartZ=0 EndX=20 EndY=85.5 EndZ=0
    g3: LineSegment StartX=20 StartY=85.5 StartZ=0 EndX=-20 EndY=85.5 EndZ=0
    g4: GeomPoint [constr] X=0 Y=75.5 Z=0
  constraints (13):
    c: Coincident(g0,g1)
    c: Coincident(g1,g2)
    c: Coincident(g2,g3)
    c: Coincident(g3,g0)
    c: Vertical(g0)
    c: Vertical(g2)
    c: Horizontal(g1)
    c: Horizontal(g3)
    c: Symmetric(g2,g0,g4)
    c: PointOnObject(g4,g-2)
    c: DistanceY(g2) = 85.5
    c: DistanceY(g2,g2) = 20
    c: DistanceX(g1,g1) = 40
FEATURE [Sketcher::SketchObject] Sketch040
  ArcFitTolerance = 1e-06
  AttachmentSupport = -> [YZ_Plane010]
  FullyConstrained = true
  MakeInternals = false
  MapMode = 5
  Placement = pos=(0,0,0) rot=(0.57735,0.57735,0.57735;2.0944rad)
  sketch-geometry (4):
    g0: LineSegment StartX=-32 StartY=-0.1 StartZ=0 EndX=-32.5 EndY=0.766025 EndZ=0
    g1: LineSegment StartX=-32.5 StartY=0.766025 StartZ=0 EndX=-33.5 EndY=0.766025 EndZ=0
    g2: LineSegment StartX=-33.5 StartY=0.766025 StartZ=0 EndX=-34 EndY=-0.1 EndZ=0
    g3: LineSegment StartX=-34 StartY=-0.1 StartZ=0 EndX=-32 EndY=-0.1 EndZ=0
  constraints (12):
    c: Coincident(g0,g1)
    c: Horizontal(g1)
    c: Coincident(g1,g2)
    c: Coincident(g2,g3)
    c: Coincident(g3,g0)
    c: Horizontal(g3)
    c: Angle(g2,g1) = 2.0944
    c: Angle(g1,g0) = 2.0944
    c: DistanceX(g3,g3) = 2
    c: DistanceX(g1,g1) = 1
    c: DistanceX(g0) = -32
    c: DistanceY(g2) = -0.1
FEATURE [Sketcher::SketchObject] Sketch042
  ArcFitTolerance = 1e-06
  AttachmentSupport = -> [YZ_Plane012]
  FullyConstrained = true
  MakeInternals = false
  MapMode = 5
  Placement = pos=(0,0,0) rot=(0.57735,0.57735,0.57735;2.0944rad)
  sketch-geometry (4):
    g0: LineSegment StartX=-34.05 StartY=-0.05 StartZ=0 EndX=-33.5 EndY=0.902628 EndZ=0
    g1: LineSegment StartX=-33.5 StartY=0.902628 StartZ=0 EndX=-32.5 EndY=0.902628 EndZ=0
    g2: LineSegment StartX=-32.5 StartY=0.902628 StartZ=0 EndX=-31.95 EndY=-0.05 EndZ=0
    g3: LineSegment StartX=-31.95 StartY=-0.05 StartZ=0 EndX=-34.05 EndY=-0.05 EndZ=0
  constraints (12):
    c: Coincident(g0,g1)
    c: Horizontal(g1)
    c: Coincident(g1,g2)
    c: Coincident(g2,g3)
    c: Coincident(g3,g0)
    c: Horizontal(g3)
    c: Angle(g3,g0) = 1.0472
    c: Equal(g0,g2)
    c: DistanceX(g3,g3) = 2.1
    c: DistanceX(g1,g1) = 1
    c: DistanceX(g2) = -31.95
    c: DistanceY(g2) = -0.05
FEATURE [PartDesign::SubShapeBinder] Binder030  label="BinderUSB"
  BindCopyOnChange = 0
  BindMode = 0
  ClaimChildren = false
  Context = -> Body012 [Binder030.]
  Fuse = false
  MakeFace = true
  OffsetFill = false
  OffsetIntersection = false
  OffsetJoinType = 0
  OffsetOpenResult = false
  PartialLoad = false
  Refine = true
  Relative = true
  Support = -> [Link002[Pad022.]]
  _Version = 2
FEATURE [Sketcher::SketchObject] Sketch045
  ArcFitTolerance = 1e-06
  AttachmentOffset = pos=(0,0,22.7) rot=(0,0,1;0rad)
  AttachmentSupport = -> [XY_Plane015]
  FullyConstrained = true
  MakeInternals = false
  MapMode = 5
  Placement = pos=(0,0,22.7) rot=(0,0,1;0rad)
  sketch-geometry (4):
    g0: LineSegment StartX=-10.5 StartY=6.4 StartZ=0 EndX=-10.5 EndY=-6.4 EndZ=0
    g1: LineSegment StartX=-10.5 StartY=-6.4 StartZ=0 EndX=10.5 EndY=-6.4 EndZ=0
    g2: LineSegment StartX=10.5 StartY=-6.4 StartZ=0 EndX=10.5 EndY=6.4 EndZ=0
    g3: LineSegment StartX=10.5 StartY=6.4 StartZ=0 EndX=-10.5 EndY=6.4 EndZ=0
  constraints (11):
    c: Coincident(g0,g1)
    c: Coincident(g1,g2)
    c: Coincident(g2,g3)
    c: Coincident(g3,g0)
    c: Vertical(g0)
    c: Vertical(g2)
    c: Horizontal(g1)
    c: Horizontal(g3)
    c: Symmetric(g0,g2,g-1)
    c: DistanceX(g1,g1) = 21
    c: DistanceY(g2,g2) = 12.8
FEATURE [Sketcher::SketchObject] Sketch046
  ArcFitTolerance = 1e-06
  AttachmentOffset = pos=(0,0,34) rot=(0,0,1;0rad)
  AttachmentSupport = -> [XY_Plane015]
  FullyConstrained = true
  MakeInternals = false
  MapMode = 5
  Placement = pos=(0,0,34) rot=(0,0,1;0rad)
  sketch-geometry (1):
    g0: Circle CenterX=0 CenterY=0 CenterZ=0 NormalX=0 NormalY=0 NormalZ=1 AngleXU=0 Radius=10
  constraints (2):
    c: Diameter(g0) = 20
    c: Coincident(g0,g-1)
FEATURE [PartDesign::AdditiveLoft] AdditiveLoft001
  Closed = false
  Profile = -> Sketch045
  Refine = true
  Ruled = false
  Sections = -> [Sketch046]
  Suppressed = false
FEATURE [Sketcher::SketchObject] Sketch047
  ArcFitTolerance = 1e-06
  AttachmentSupport = -> [XY_Plane015]
  FullyConstrained = true
  MakeInternals = false
  MapMode = 5
  sketch-geometry (2):
    g0: Circle CenterX=-5 CenterY=0 CenterZ=0 NormalX=0 NormalY=0 NormalZ=1 AngleXU=0 Radius=2.25
    g1: Circle CenterX=5 CenterY=0 CenterZ=0 NormalX=0 NormalY=0 NormalZ=1 AngleXU=0 Radius=2.25
  constraints (6):
    c: Diameter(g0) = 4.5
    c: PointOnObject(g0,g-1)
    c: PointOnObject(g1,g-1)
    c: Equal(g1,g0)
    c: DistanceX(g1) = 5
    c: DistanceX(g0) = -5
FEATURE [PartDesign::Pocket] Pocket007
  BaseFeature = -> AdditiveLoft001
  Direction = (0,0,-1)
  Length = 5
  Length2 = 5
  Midplane = true
  Profile = -> Sketch047
  ReferenceAxis = -> Sketch047 [N_Axis]
  Refine = true
  Suppressed = false
  Type = 1
FEATURE [PartDesign::Body] Body015  label="Distance"
  AllowCompound = false
  Group = -> [Sketch045,Sketch046,AdditiveLoft001,Sketch047,Pocket007]
  Origin = -> Origin015
  Tip = -> Pocket007
FEATURE [Sketcher::SketchObject] Sketch051
  ArcFitTolerance = 1e-06
  AttachmentSupport = -> [XY_Plane012]
  FullyConstrained = true
  MakeInternals = false
  MapMode = 5
  sketch-geometry (12):
    g0: LineSegment StartX=-36.5 StartY=45 StartZ=0 EndX=-42.5 EndY=45 EndZ=0
    g1: LineSegment StartX=-48.5 StartY=39 StartZ=0 EndX=-48.5 EndY=28 EndZ=0
    g2: LineSegment StartX=-48.5 StartY=28 StartZ=0 EndX=-42.5 EndY=28 EndZ=0
    g3: LineSegment StartX=-33.5 StartY=39 StartZ=0 EndX=-33.5 EndY=42 EndZ=0
    g4: ArcOfCircle CenterX=-42.5 CenterY=39 CenterZ=0 NormalX=0 NormalY=0 NormalZ=1 AngleXU=0 Radius=6 StartAngle=1.5708 EndAngle=3.14159
    g5: GeomPoint [constr] X=-48.5 Y=45 Z=0
    g6: LineSegment StartX=-30.5 StartY=33 StartZ=0 EndX=-42.5 EndY=33 EndZ=0
    g7: LineSegment StartX=-42.5 StartY=33 StartZ=0 EndX=-42.5 EndY=28 EndZ=0
    g8: ArcOfCircle CenterX=-30.5 CenterY=39 CenterZ=0 NormalX=0 NormalY=0 NormalZ=1 AngleXU=0 Radius=3 StartAngle=3.14159 EndAngle=4.71239
    g9: LineSegment StartX=-30.5 StartY=36 StartZ=0 EndX=-30.5 EndY=33 EndZ=0
    g10: ArcOfCircle CenterX=-36.5 CenterY=42 CenterZ=0 NormalX=0 NormalY=0 NormalZ=1 AngleXU=0 Radius=3 StartAngle=-9e-16 EndAngle=1.5708
    g11: GeomPoint [constr] X=-33.5 Y=45 Z=0
  constraints (32):
    c: Coincident(g1,g2)
    c: Horizontal(g0)
    c: Horizontal(g2)
    c: Vertical(g1)
    c: Vertical(g3)
    c: PointOnObject(g5,g0)
    c: PointOnObject(g5,g1)
    c: Tangent(g0,g4) = -1.5708
    c: Tangent(g1,g4) = -1.5708
    c: Horizontal(g6)
    c: Coincident(g6,g7)
    c: Vertical(g7)
    c: Coincident(g2,g7)
    c: DistanceX(g2,g2) = 6
    c: DistanceY(g6,g11) = 12
    c: Radius(g4) = 6
    c: Coincident(g9,g8)
    c: Radius(g8) = 3
    c: Perpendicular(g8,g9)
    c: Vertical(g9)
    c: Coincident(g6,g9)
    c: Tangent(g3,g8) = 1.5708
    c: DistanceY(g9,g9) = 3
    c: DistanceX(g6) = -30.5
    c: DistanceY(g6) = 33
    c: DistanceX(g6,g6) = 12
    c: DistanceY(g7,g7) = 5
    c: PointOnObject(g11,g0)
    c: PointOnObject(g11,g3)
    c: Tangent(g0,g10) = -1.5708
    c: Tangent(g3,g10) = -1.5708
    c: Radius(g10) = 3
FEATURE [Sketcher::SketchObject] Sketch052
  ArcFitTolerance = 1e-06
  AttachmentSupport = -> [XY_Plane012]
  FullyConstrained = true
  MakeInternals = false
  MapMode = 5
  sketch-geometry (1):
    g0: Circle CenterX=-42 CenterY=38.5 CenterZ=0 NormalX=0 NormalY=0 NormalZ=1 AngleXU=0 Radius=2.8
  constraints (3):
    c: Diameter(g0) = 5.6
    c: DistanceY(g0) = 38.5
    c: DistanceX(g0) = -42
FEATURE [PartDesign::Mirrored] Mirrored
  MirrorPlane = -> Sketch051 [V_Axis]
  Refine = true
  Suppressed = false
  TransformMode = 0
FEATURE [PartDesign::Mirrored] Mirrored001
  MirrorPlane = -> XZ_Plane012
  Refine = true
  Suppressed = false
  TransformMode = 0
FEATURE [Sketcher::SketchObject] Sketch054
  ArcFitTolerance = 1e-06
  AttachmentOffset = pos=(0,0,8.5) rot=(0,0,1;0rad)
  AttachmentSupport = -> [XY_Plane010]
  FullyConstrained = true
  MakeInternals = false
  MapMode = 5
  Placement = pos=(0,0,-8.5) rot=(0,1,0;3.14159rad)
  sketch-geometry (4):
    g0: Circle CenterX=-42 CenterY=38.5 CenterZ=0 NormalX=0 NormalY=0 NormalZ=1 AngleXU=0 Radius=4.75
    g1: Circle CenterX=42 CenterY=38.5 CenterZ=0 NormalX=0 NormalY=0 NormalZ=1 AngleXU=0 Radius=4.75
    g2: Circle CenterX=42 CenterY=-38.5 CenterZ=0 NormalX=0 NormalY=0 NormalZ=1 AngleXU=0 Radius=4.75
    g3: Circle CenterX=-42 CenterY=-38.5 CenterZ=0 NormalX=0 NormalY=0 NormalZ=1 AngleXU=0 Radius=4.75
  constraints (11):
    c: Horizontal(g3,g2)
    c: Horizontal(g1,g0)
    c: Vertical(g0,g3)
    c: Vertical(g1,g2)
    c: Symmetric(g0,g2,g-1)
    c: DistanceX(g3,g2) = 84
    c: DistanceY(g2,g1) = 77
    c: Equal(g0,g1)
    c: Equal(g1,g2)
    c: Equal(g2,g3)
    c: Diameter(g3) = 9.5
FEATURE [PartDesign::SubShapeBinder] Binder032
  BindCopyOnChange = 0
  BindMode = 0
  ClaimChildren = false
  Context = -> Body014 [Binder032.]
  Fuse = false
  MakeFace = true
  OffsetFill = false
  OffsetIntersection = false
  OffsetJoinType = 0
  OffsetOpenResult = false
  PartialLoad = false
  Refine = true
  Relative = true
  Support = -> [Link003[Pocket.]]
  _Version = 2
FEATURE [PartDesign::Boolean] Boolean012  label="BooleanSwitch"
  BaseFeature = -> Boolean009
  Group = -> [Binder032]
  Refine = true
  Suppressed = false
  Type = 1
  UsePlacement = true
FEATURE [PartDesign::Chamfer] Chamfer002
  Angle = 45
  Base = -> PolarPattern001 [Face40]
  BaseFeature = -> PolarPattern001
  ChamferType = 0
  FlipDirection = false
  Refine = true
  Size = 1
  Size2 = 1
  SupportTransform = false
  Suppressed = false
  UseAllEdges = false
FEATURE [PartDesign::Body] Body011  label="Button"
  AllowCompound = false
  Group = -> [Sketch017,Revolution002,Sketch018,Revolution003,PolarPattern001,Chamfer002]
  Origin = -> Origin011
  Placement = pos=(-3.25e-14,-71.5646,17.6465) rot=(-0.250563,-0.250563,-0.935113;1.63783rad)
  Tip = -> Chamfer002
FEATURE [PartDesign::SubShapeBinder] Binder033  label="BinderBottom"
  BindCopyOnChange = 0
  BindMode = 0
  ClaimChildren = false
  Context = -> Body012 [Binder033.]
  Fuse = false
  MakeFace = true
  OffsetFill = false
  OffsetIntersection = false
  OffsetJoinType = 0
  OffsetOpenResult = false
  PartialLoad = false
  Refine = true
  Relative = true
  Support = -> [Body010]
  _Version = 2
FEATURE [Part::FeaturePython] Array002  label="base_bezels"  # Draft array (typed FeaturePython)
  Angle = 360
  ArrayType = 1
  Axis = (0,0,1)
  Base = -> Common
  Center = (0,0,0)
  Count = 4
  Fuse = true
  IntervalAxis = (0,0,0)
  IntervalX = (50,0,0)
  IntervalY = (0,50,0)
  IntervalZ = (0,0,50)
  NumberCircles = 3
  NumberPolar = 4
  NumberX = 2
  NumberY = 2
  NumberZ = 1
  RadialDistance = 50
  Symmetry = 1
  TangentialDistance = 25
FEATURE [Sketcher::SketchObject] Sketch056
  ArcFitTolerance = 1e-06
  AttachmentOffset = pos=(0,0,0) rot=(0,1,0;0.785398rad)
  AttachmentSupport = -> [XZ_Plane018]
  FullyConstrained = true
  MakeInternals = false
  MapMode = 5
  Placement = pos=(0,0,0) rot=(0.862856,0.357407,0.357407;1.71777rad)
  sketch-geometry (22):
    g0: LineSegment StartX=66.9852 StartY=13.8423 StartZ=0 EndX=53.4852 EndY=37.225 EndZ=0
    g1: ArcOfCircle CenterX=65.75 CenterY=32.1817 CenterZ=0 NormalX=0 NormalY=0 NormalZ=1 AngleXU=0 Radius=1.35 StartAngle=5.23599 EndAngle=8.37758
    g2: ArcOfCircle CenterX=66.875 CenterY=30.2332 CenterZ=0 NormalX=0 NormalY=0 NormalZ=1 AngleXU=0 Radius=0.9 StartAngle=2.0944 EndAngle=3.66519
    g3: LineSegment StartX=66.0956 StartY=29.7832 StartZ=0 EndX=78.0956 EndY=8.99856 EndZ=0
    g4: ArcOfCircle CenterX=78.875 CenterY=9.44856 CenterZ=0 NormalX=0 NormalY=0 NormalZ=1 AngleXU=0 Radius=0.9 StartAngle=3.66519 EndAngle=5.23599
    g5: ArcOfCircle CenterX=80 CenterY=7.5 CenterZ=0 NormalX=0 NormalY=0 NormalZ=1 AngleXU=0 Radius=1.35 StartAngle=5.23599 EndAngle=8.37758
    g6: ArcOfCircle CenterX=78.875 CenterY=9.44856 CenterZ=0 NormalX=0 NormalY=0 NormalZ=1 AngleXU=0 Radius=3.6 StartAngle=3.66519 EndAngle=5.23599
    g7: LineSegment StartX=75.7573 StartY=7.64856 StartZ=0 EndX=70.8823 EndY=16.0923 EndZ=0
    g8: ArcOfCircle CenterX=70.1029 CenterY=15.6423 CenterZ=0 NormalX=0 NormalY=0 NormalZ=1 AngleXU=0 Radius=0.9 StartAngle=0.523599 EndAngle=3.66519
    g9: LineSegment [constr] StartX=79.325 StartY=8.66913 StartZ=0 EndX=80.675 EndY=6.33087 EndZ=0
    g10: LineSegment [constr] StartX=75.7573 StartY=7.64856 StartZ=0 EndX=78.0956 EndY=8.99856 EndZ=0
    g11: ArcOfCircle CenterX=67.8529 CenterY=19.5394 CenterZ=0 NormalX=0 NormalY=0 NormalZ=1 AngleXU=0 Radius=0.9 StartAngle=3.66519 EndAngle=6.80678
    g12: LineSegment StartX=68.6323 StartY=19.9894 StartZ=0 EndX=63.7573 EndY=28.4332 EndZ=0
    g13: ArcOfCircle CenterX=66.875 CenterY=30.2332 CenterZ=0 NormalX=0 NormalY=0 NormalZ=1 AngleXU=0 Radius=3.6 StartAngle=2.0944 EndAngle=3.66519
    g14: LineSegment [constr] StartX=65.075 StartY=33.3509 StartZ=0 EndX=66.425 EndY=31.0126 EndZ=0
    g15: ArcOfCircle CenterX=68.1543 CenterY=14.5173 CenterZ=0 NormalX=0 NormalY=0 NormalZ=1 AngleXU=0 Radius=1.35 StartAngle=3.66519 EndAngle=6.80678
    g16: ArcOfCircle CenterX=54.6543 CenterY=37.9 CenterZ=0 NormalX=0 NormalY=0 NormalZ=1 AngleXU=0 Radius=1.35 StartAngle=0.523599 EndAngle=3.66519
    g17: LineSegment StartX=55.8235 StartY=38.575 StartZ=0 EndX=67.0735 EndY=19.0894 EndZ=0
    g18: LineSegment [constr] StartX=70.8823 StartY=16.0923 StartZ=0 EndX=69.3235 EndY=15.1923 EndZ=0
    g19: LineSegment [constr] StartX=68.6323 StartY=19.9894 StartZ=0 EndX=67.0735 EndY=19.0894 EndZ=0
    g20: LineSegment [constr] StartX=69.3235 StartY=15.1923 StartZ=0 EndX=66.9852 EndY=13.8423 EndZ=0
    g21: LineSegment [constr] StartX=53.4852 StartY=37.225 StartZ=0 EndX=55.8235 EndY=38.575 EndZ=0
  constraints (54):
    c: Tangent(g1,g2) = 1.5708
    c: Tangent(g2,g3) = -1.5708
    c: Tangent(g3,g4) = -1.5708
    c: Tangent(g4,g5) = 1.5708
    c: Tangent(g5,g6) = -1.5708
    c: Tangent(g7,g8) = -1.5708
    c: Equal(g5,g1)
    c: Equal(g4,g2)
    c: Tangent(g6,g7) = 1.5708
    c: Coincident(g9,g4)
    c: Coincident(g9,g5)
    c: Coincident(g4,g6)
    c: Radius(g8) = 0.9
    c: Angle(g0,g-1) = 1.0472
    c: Parallel(g3,g7)
    c: Equal(g2,g8)
    c: Coincident(g10,g6)
    c: Coincident(g10,g3)
    c: Perpendicular(g10,g9)
    c: Tangent(g11,g12) = -1.5708
    c: Tangent(g12,g13) = 1.5708
    c: Tangent(g13,g1) = -1.5708
    c: Coincident(g14,g1)
    c: Coincident(g14,g1)
    c: PointOnObject(g1,g14)
    c: Tangent(g7,g12)
    c: Equal(g8,g11)
    c: Equal(g7,g12)
    c: Parallel(g14,g3)
    c: Distance(g12,g2) = 2.7
    c: DistanceY(g5) = 7.5
    c: DistanceX(g5) = 80
    c: Distance(g3,g3) = 24
    c: Distance(g0,g0) = 27
    c: Tangent(g0,g15) = 1.5708
    c: Tangent(g8,g15) = 1.5708
    c: Tangent(g0,g16) = 1.5708
    c: Tangent(g16,g17) = 1.5708
    c: Coincident(g17,g11)
    c: Parallel(g0,g17)
    c: Radius(g15) = 1.35
    c: Coincident(g18,g7)
    c: Coincident(g18,g8)
    c: Coincident(g19,g11)
    c: Coincident(g19,g11)
    c: PointOnObject(g8,g18)
    c: PointOnObject(g11,g19)
    c: Distance(g11,g8) = 4.5
    c: Coincident(g20,g8)
    c: Coincident(g20,g0)
    c: Coincident(g21,g0)
    c: Coincident(g21,g16)
    c: Parallel(g17,g12)
    c: Equal(g15,g1)
FEATURE [PartDesign::Pad] Pad028
  Direction = (0.707107,-0.707107,1e-16)
  Length = 34
  Length2 = 10
  Midplane = true
  Placement = pos=(0,0,0) rot=(1,0,0;1.5708rad)
  Profile = -> Sketch056
  ReferenceAxis = -> Sketch056 [N_Axis]
  Refine = true
  Suppressed = false
  Type = 0
FEATURE [PartDesign::Pocket] Pocket010
  BaseFeature = -> Pad028
  Direction = (-0.707107,0.707107,-1e-16)
  Length = 24
  Length2 = 5
  Midplane = true
  Placement = pos=(0,0,0) rot=(1,0,0;1.5708rad)
  Profile = -> Sketch056
  ReferenceAxis = -> Sketch056 [N_Axis]
  Refine = true
  Suppressed = false
  Type = 0
FEATURE [PartDesign::PolarPattern] PolarPattern005
  Angle = 360
  Axis = -> Z_Axis018
  Mode = 0
  Occurrences = 4
  Offset = 120
  Placement = pos=(0,0,0) rot=(1,0,0;1.5708rad)
  Refine = true
  Suppressed = false
  TransformMode = 0
FEATURE [PartDesign::MultiTransform] MultiTransform002
  BaseFeature = -> Pocket010
  Originals = -> [Pad028,Pocket010]
  Placement = pos=(0,0,0) rot=(1,0,0;1.5708rad)
  Refine = true
  Suppressed = false
  TransformMode = 0
  Transformations = -> [PolarPattern005]
FEATURE [PartDesign::Body] Body018  label="Displaybrackets"
  AllowCompound = true
  Group = -> [Sketch056,Pad028,Pocket010,MultiTransform002,PolarPattern005]
  Origin = -> Origin018
  Tip = -> MultiTransform002
FEATURE [PartDesign::SubShapeBinder] Binder035
  BindCopyOnChange = 0
  BindMode = 0
  ClaimChildren = false
  Context = -> Body019 [Binder035.]
  Fuse = false
  MakeFace = true
  Offset = 0.1
  OffsetFill = false
  OffsetIntersection = false
  OffsetJoinType = 0
  OffsetOpenResult = false
  PartialLoad = false
  Refine = true
  Relative = true
  Support = -> [Body018[Sketch056.]]
  _Version = 2
FEATURE [PartDesign::Pad] Pad029
  Direction = (-0.707107,0.707107,0)
  Length = 34.6
  Length2 = 10
  Midplane = true
  Profile = -> Binder035
  Refine = true
  Suppressed = false
  Type = 0
FEATURE [PartDesign::Pocket] Pocket011
  BaseFeature = -> Pad029
  Direction = (0.707107,-0.707107,0)
  Length = 23.4
  Length2 = 5
  Midplane = true
  Profile = -> Binder035
  Refine = true
  Suppressed = false
  Type = 0
FEATURE [PartDesign::PolarPattern] PolarPattern006
  Angle = 360
  Axis = -> Z_Axis019
  Mode = 0
  Occurrences = 4
  Offset = 120
  Refine = true
  Suppressed = false
  TransformMode = 0
FEATURE [PartDesign::MultiTransform] MultiTransform003
  BaseFeature = -> Pocket011
  Refine = true
  Suppressed = false
  TransformMode = 1
  Transformations = -> [PolarPattern006]
FEATURE [PartDesign::Body] Body019  label="Displaybrackets_cut"
  AllowCompound = true
  Group = -> [Binder035,Pad029,Pocket011,MultiTransform003,PolarPattern006]
  Origin = -> Origin019
  Tip = -> MultiTransform003
FEATURE [PartDesign::SubShapeBinder] Binder037  label="BinderDispBrackets"
  BindCopyOnChange = 0
  BindMode = 0
  ClaimChildren = false
  Context = -> Body012 [Binder037.]
  Fuse = false
  MakeFace = true
  OffsetFill = false
  OffsetIntersection = false
  OffsetJoinType = 0
  OffsetOpenResult = false
  PartialLoad = false
  Refine = true
  Relative = true
  Support = -> [Body019]
  _Version = 2
FEATURE [PartDesign::SubShapeBinder] Binder038
  BindCopyOnChange = 0
  BindMode = 0
  ClaimChildren = false
  Context = -> Body014 [Boolean017.Binder038.]
  Fuse = false
  MakeFace = true
  OffsetFill = false
  OffsetIntersection = false
  OffsetJoinType = 0
  OffsetOpenResult = false
  PartialLoad = false
  Refine = true
  Relative = true
  Support = -> [Body019]
  _Version = 2
FEATURE [PartDesign::SubShapeBinder] Binder040  label="BinderDisplay2"
  BindCopyOnChange = 0
  BindMode = 0
  ClaimChildren = false
  Context = -> Body012 [Binder040.]
  Fuse = false
  MakeFace = true
  OffsetFill = false
  OffsetIntersection = false
  OffsetJoinType = 0
  OffsetOpenResult = false
  PartialLoad = false
  Refine = true
  Relative = true
  Support = -> [CompoundFilter[Face31]]
  _Version = 2
FEATURE [Sketcher::SketchObject] Sketch059
  ArcFitTolerance = 1e-06
  AttachmentSupport = -> [Binder017]
  ExternalGeometry = -> [Binder017]
  FullyConstrained = false
  MakeInternals = false
  MapMode = 5
  Placement = pos=(0.769267,0.769267,-1.88431) rot=(0.98311,-0.035247,0.17959;3.5228rad)
  sketch-geometry (12):
    g0: LineSegment StartX=67.277 StartY=-36.2124 StartZ=0 EndX=69.152 EndY=-38.3775 EndZ=0
    g1: LineSegment StartX=69.152 StartY=-38.3775 StartZ=0 EndX=63.7093 EndY=-43.091 EndZ=0
    g2: LineSegment StartX=63.7093 StartY=-43.091 StartZ=0 EndX=65.3132 EndY=-44.9431 EndZ=0
    g3: LineSegment StartX=65.3132 StartY=-44.9431 StartZ=0 EndX=32.1658 EndY=-73.6496 EndZ=0
    g4: LineSegment StartX=32.1658 StartY=-73.6496 StartZ=0 EndX=30.5619 EndY=-71.7976 EndZ=0
    g5: LineSegment StartX=30.5619 StartY=-71.7976 StartZ=0 EndX=23.4939 EndY=-77.9186 EndZ=0
    g6: LineSegment StartX=23.4939 StartY=-77.9186 StartZ=0 EndX=19.9771 EndY=-73.8577 EndZ=0
    g7: LineSegment StartX=19.9771 StartY=-73.8577 StartZ=0 EndX=11.7092 EndY=-52.1987 EndZ=0
    g8: LineSegment StartX=11.7092 StartY=-52.1987 StartZ=0 EndX=37.32 EndY=-49.0841 EndZ=0
    g9: LineSegment StartX=37.32 StartY=-49.0841 StartZ=0 EndX=47.3638 EndY=-40.9242 EndZ=0
    g10: LineSegment StartX=47.3638 StartY=-40.9242 StartZ=0 EndX=53.5497 EndY=-28.5667 EndZ=0
    g11: LineSegment StartX=53.5497 StartY=-28.5667 StartZ=0 EndX=67.277 EndY=-36.2124 EndZ=0
  constraints (22):
    c: Coincident(g0,g-4)
    c: Coincident(g0,g-5)
    c: Coincident(g0,g1)
    c: Coincident(g1,g-6)
    c: Coincident(g1,g2)
    c: Coincident(g2,g-7)
    c: Coincident(g2,g3)
    c: Coincident(g3,g-8)
    c: Coincident(g3,g4)
    c: Coincident(g4,g-9)
    c: Coincident(g4,g5)
    c: Coincident(g5,g-10)
    c: Coincident(g5,g6)
    c: Coincident(g6,g-3)
    c: Coincident(g6,g7)
    c: Coincident(g7,g8)
    c: Coincident(g8,g9)
    c: Coincident(g9,g10)
    c: Coincident(g10,g11)
    c: Coincident(g11,g0)
    c: Angle(g11,g0) = 2.7927
    c: Angle(g6,g7) = 2.79253
FEATURE [Sketcher::SketchObject] Sketch060
  ArcFitTolerance = 1e-06
  AttachmentOffset = pos=(0,0,-10) rot=(0,0,1;0rad)
  AttachmentSupport = -> [Binder017]
  ExternalGeometry = -> [Binder017]
  FullyConstrained = false
  MakeInternals = false
  MapMode = 5
  Placement = pos=(-2.76627,-2.76627,6.77594) rot=(0.98311,-0.035247,0.17959;3.5228rad)
  sketch-geometry (13):
    g0: LineSegment StartX=67.277 StartY=-36.2124 StartZ=0 EndX=69.152 EndY=-38.3775 EndZ=0
    g1: LineSegment StartX=69.152 StartY=-38.3775 StartZ=0 EndX=63.7093 EndY=-43.091 EndZ=0
    g2: LineSegment StartX=63.7093 StartY=-43.091 StartZ=0 EndX=65.3132 EndY=-44.9431 EndZ=0
    g3: LineSegment StartX=65.3132 StartY=-44.9431 StartZ=0 EndX=32.1658 EndY=-73.6496 EndZ=0
    g4: LineSegment StartX=32.1658 StartY=-73.6496 StartZ=0 EndX=30.5619 EndY=-71.7976 EndZ=0
    g5: LineSegment StartX=30.5619 StartY=-71.7976 StartZ=0 EndX=23.4939 EndY=-77.9186 EndZ=0
    g6: LineSegment StartX=23.4939 StartY=-77.9186 StartZ=0 EndX=22.6035 EndY=-76.8904 EndZ=0
    g7: LineSegment StartX=22.6035 StartY=-76.8904 StartZ=0 EndX=18.3381 EndY=-65.7167 EndZ=0
    g8: LineSegment StartX=18.3381 StartY=-65.7167 StartZ=0 EndX=34.7325 EndY=-54.7567 EndZ=0
    g9: LineSegment StartX=34.7325 StartY=-54.7567 StartZ=0 EndX=48.8345 EndY=-42.5448 EndZ=0
    g10: LineSegment StartX=48.8345 StartY=-42.5448 StartZ=0 EndX=58.5174 EndY=-31.3336 EndZ=0
    g11: LineSegment StartX=58.5174 StartY=-31.3336 StartZ=0 EndX=67.277 EndY=-36.2124 EndZ=0
    g12: LineSegment [constr] StartX=19.9771 StartY=-73.8577 StartZ=0 EndX=22.6035 EndY=-76.8904 EndZ=0
  constraints (23):
    c: Coincident(g0,g-4)
    c: Coincident(g0,g-5)
    c: Coincident(g0,g1)
    c: Coincident(g1,g-6)
    c: Coincident(g1,g2)
    c: Coincident(g2,g-7)
    c: Coincident(g2,g3)
    c: Coincident(g3,g-8)
    c: Coincident(g3,g4)
    c: Coincident(g4,g-9)
    c: Coincident(g4,g5)
    c: Coincident(g5,g-10)
    c: Coincident(g5,g6)
    c: Coincident(g7,g8)
    c: Coincident(g8,g9)
    c: Coincident(g9,g10)
    c: Coincident(g10,g11)
    c: Coincident(g11,g0)
    c: Angle(g11,g0) = 2.7927
    c: Angle(g6,g7) = 2.79253
    c: Coincident(g7,g6)
    c: Coincident(g12,g-3)
    c: Tangent(g12,g6) = 1.5708
FEATURE [PartDesign::AdditiveLoft] AdditiveLoft002
  BaseFeature = -> Pad022
  Closed = false
  Profile = -> Sketch059
  Refine = true
  Ruled = false
  Sections = -> [Sketch060]
  Suppressed = false
FEATURE [Sketcher::SketchObject] Sketch061
  ArcFitTolerance = 1e-06
  AttachmentSupport = -> [Binder040]
  ExternalGeometry = -> [Binder040]
  FullyConstrained = false
  MakeInternals = false
  MapMode = 5
  Placement = pos=(0.769267,-0.769267,-1.88431) rot=(0.98311,0.035247,0.179591;2.76038rad)
  sketch-geometry (13):
    g0: LineSegment StartX=26.23 StartY=71.7602 StartZ=0 EndX=28.105 EndY=73.9253 EndZ=0
    g1: LineSegment StartX=28.105 StartY=73.9253 StartZ=0 EndX=33.5477 EndY=69.2118 EndZ=0
    g2: LineSegment StartX=33.5477 StartY=69.2118 StartZ=0 EndX=35.1516 EndY=71.0638 EndZ=0
    g3: LineSegment StartX=35.1516 StartY=71.0638 StartZ=0 EndX=68.2991 EndY=42.3572 EndZ=0
    g4: LineSegment StartX=68.2991 StartY=42.3572 StartZ=0 EndX=66.6952 EndY=40.5052 EndZ=0
    g5: LineSegment StartX=66.6952 StartY=40.5052 StartZ=0 EndX=73.7631 EndY=34.3842 EndZ=0
    g6: LineSegment StartX=73.7631 StartY=34.3842 StartZ=0 EndX=70.2463 EndY=30.3233 EndZ=0
    g7: LineSegment StartX=70.2463 StartY=30.3233 StartZ=0 EndX=53.4637 EndY=20.9797 EndZ=0
    g8: LineSegment StartX=53.4637 StartY=20.9797 StartZ=0 EndX=50.5782 EndY=35.2097 EndZ=0
    g9: LineSegment StartX=50.5782 StartY=35.2097 StartZ=0 EndX=42.4985 EndY=45.139 EndZ=0
    g10: LineSegment StartX=42.4985 StartY=45.139 StartZ=0 EndX=29.0647 EndY=52.6347 EndZ=0
    g11: LineSegment StartX=29.0647 StartY=52.6347 StartZ=0 EndX=19.2336 EndY=53.4321 EndZ=0
    g12: LineSegment StartX=19.2336 StartY=53.4321 StartZ=0 EndX=26.23 EndY=71.7602 EndZ=0
  constraints (23):
    c: Coincident(g0,g-3)
    c: Coincident(g0,g-4)
    c: Coincident(g0,g1)
    c: Coincident(g1,g-5)
    c: Coincident(g1,g2)
    c: Coincident(g2,g-6)
    c: Coincident(g2,g3)
    c: Coincident(g3,g-7)
    c: Coincident(g3,g4)
    c: Coincident(g4,g-8)
    c: Coincident(g4,g5)
    c: Coincident(g5,g-9)
    c: Coincident(g5,g6)
    c: Coincident(g6,g-10)
    c: Coincident(g6,g7)
    c: Coincident(g7,g8)
    c: Coincident(g8,g9)
    c: Coincident(g9,g10)
    c: Coincident(g10,g11)
    c: Coincident(g11,g12)
    c: Coincident(g12,g0)
    c: Angle(g6,g7) = 2.79253
    c: Angle(g12,g0) = 2.79253
FEATURE [Sketcher::SketchObject] Sketch062
  ArcFitTolerance = 1e-06
  AttachmentOffset = pos=(0,0,-10) rot=(0,0,1;0rad)
  AttachmentSupport = -> [Binder040]
  ExternalGeometry = -> [Binder040]
  FullyConstrained = false
  MakeInternals = false
  MapMode = 5
  Placement = pos=(-2.76627,2.76627,6.77594) rot=(0.98311,0.035247,0.179591;2.76038rad)
  sketch-geometry (13):
    g0: LineSegment StartX=26.23 StartY=71.7602 StartZ=0 EndX=28.105 EndY=73.9253 EndZ=0
    g1: LineSegment StartX=28.105 StartY=73.9253 StartZ=0 EndX=33.5477 EndY=69.2118 EndZ=0
    g2: LineSegment StartX=33.5477 StartY=69.2118 StartZ=0 EndX=35.1516 EndY=71.0638 EndZ=0
    g3: LineSegment StartX=35.1516 StartY=71.0638 StartZ=0 EndX=68.2991 EndY=42.3572 EndZ=0
    g4: LineSegment StartX=68.2991 StartY=42.3572 StartZ=0 EndX=66.6952 EndY=40.5052 EndZ=0
    g5: LineSegment StartX=66.6952 StartY=40.5052 StartZ=0 EndX=73.7631 EndY=34.3842 EndZ=0
    g6: LineSegment StartX=73.7631 StartY=34.3842 StartZ=0 EndX=70.2463 EndY=30.3233 EndZ=0
    g7: LineSegment StartX=70.2463 StartY=30.3233 StartZ=0 EndX=58.016 EndY=23.5141 EndZ=0
    g8: LineSegment StartX=58.016 StartY=23.5141 StartZ=0 EndX=53.2451 EndY=38.3156 EndZ=0
    g9: LineSegment StartX=53.2451 StartY=38.3156 StartZ=0 EndX=44.7307 EndY=48.1473 EndZ=0
    g10: LineSegment StartX=44.7307 StartY=48.1473 StartZ=0 EndX=31.3681 EndY=55.9125 EndZ=0
    g11: LineSegment StartX=31.3681 StartY=55.9125 StartZ=0 EndX=21.7527 EndY=60.0312 EndZ=0
    g12: LineSegment StartX=21.7527 StartY=60.0312 StartZ=0 EndX=26.23 EndY=71.7602 EndZ=0
  constraints (23):
    c: Coincident(g0,g-3)
    c: Coincident(g0,g-4)
    c: Coincident(g0,g1)
    c: Coincident(g1,g-5)
    c: Coincident(g1,g2)
    c: Coincident(g2,g-6)
    c: Coincident(g2,g3)
    c: Coincident(g3,g-7)
    c: Coincident(g3,g4)
    c: Coincident(g4,g-8)
    c: Coincident(g4,g5)
    c: Coincident(g5,g-9)
    c: Coincident(g5,g6)
    c: Coincident(g6,g-10)
    c: Coincident(g6,g7)
    c: Coincident(g7,g8)
    c: Coincident(g8,g9)
    c: Coincident(g9,g10)
    c: Coincident(g10,g11)
    c: Coincident(g11,g12)
    c: Coincident(g12,g0)
    c: Angle(g12,g0) = 2.79253
    c: Angle(g6,g7) = 2.79253
FEATURE [PartDesign::AdditiveLoft] AdditiveLoft003
  BaseFeature = -> AdditiveLoft002
  Closed = false
  Profile = -> Sketch061
  Refine = true
  Ruled = false
  Sections = -> [Sketch062]
  Suppressed = false
FEATURE [PartDesign::PolarPattern] PolarPattern009
  Angle = 360
  Axis = -> Z_Axis012
  BaseFeature = -> AdditiveLoft003
  Mode = 0
  Occurrences = 2
  Offset = 120
  Originals = -> [AdditiveLoft002,AdditiveLoft003]
  Refine = true
  Suppressed = false
  TransformMode = 0
FEATURE [PartDesign::Boolean] Boolean002  label="BooleanUSB"
  BaseFeature = -> PolarPattern009
  Group = -> [Binder030]
  Refine = true
  Suppressed = false
  Type = 1
  UsePlacement = true
FEATURE [PartDesign::Boolean] Boolean003  label="BooleanAkku"
  BaseFeature = -> Boolean002
  Group = -> [Binder021]
  Refine = true
  Suppressed = false
  Type = 1
  UsePlacement = true
FEATURE [PartDesign::Boolean] Boolean004  label="BooleanESP"
  BaseFeature = -> Boolean003
  Group = -> [Binder022]
  Refine = true
  Suppressed = false
  Type = 1
  UsePlacement = true
FEATURE [PartDesign::Boolean] Boolean005  label="BooleanLC"
  BaseFeature = -> Boolean004
  Group = -> [Binder023]
  Refine = true
  Suppressed = false
  Type = 1
  UsePlacement = true
FEATURE [PartDesign::Boolean] Boolean006  label="BooleanEnc"
  BaseFeature = -> Boolean005
  Group = -> [Binder024]
  Refine = true
  Suppressed = false
  Type = 1
  UsePlacement = true
FEATURE [PartDesign::Boolean] Boolean007  label="BooleanEnc2"
  BaseFeature = -> Boolean006
  Group = -> [Binder026]
  Refine = true
  Suppressed = false
  Type = 1
  UsePlacement = true
FEATURE [PartDesign::Pad] Pad027  label="PadScrewPad"
  BaseFeature = -> Boolean007
  Direction = (0,0,1)
  Length = 10
  Length2 = 10
  Profile = -> Sketch051
  ReferenceAxis = -> Sketch051 [N_Axis]
  Refine = true
  Suppressed = false
  Type = 0
FEATURE [PartDesign::Pocket] Pocket009  label="PocketScrew"
  BaseFeature = -> Pad027
  Direction = (0,0,-1)
  Length = 9
  Length2 = 5
  Profile = -> Sketch052
  ReferenceAxis = -> Sketch052 [N_Axis]
  Refine = true
  Reversed = true
  Suppressed = false
  Type = 0
FEATURE [PartDesign::MultiTransform] MultiTransform001  label="MultiTransformScrews"
  BaseFeature = -> Pocket009
  Originals = -> [Pad027,Pocket009]
  Refine = true
  Suppressed = false
  TransformMode = 0
  Transformations = -> [Mirrored,Mirrored001]
FEATURE [PartDesign::Boolean] Boolean013  label="BooleanBottom"
  BaseFeature = -> MultiTransform001
  Group = -> [Binder033]
  Refine = true
  Suppressed = false
  Type = 1
  UsePlacement = true
FEATURE [PartDesign::Boolean] Boolean016  label="BooleanDispBrackets"
  BaseFeature = -> Boolean013
  Group = -> [Binder037]
  Refine = true
  Suppressed = false
  Type = 1
  UsePlacement = true
FEATURE [PartDesign::Body] Body012  label="Inner"
  AllowCompound = true
  BaseFeature = -> Cut002
  Group = -> [BaseFeature,Sketch024,Sketch025,AdditiveLoft,Sketch027,Sketch028,Pocket003,Sketch029,Sketch030,Pad019,Sketch031,Pad020,Sketch032,Pad021,Binder016,Sketch033,Pad022,Binder017,Sketch061,Sketch062,AdditiveLoft002,AdditiveLoft003,Binder018,Sketch060,PolarPattern009,Boolean002,Boolean003,Boolean004,Boolean005,Boolean006,Boolean007,Sketch042,Sketch051,Pad027,Sketch052,Pocket009,MultiTransform001,+6 more]
  Origin = -> Origin012
  Tip = -> Boolean016
FEATURE [Sketcher::SketchObject] Sketch070  label="SketchPatternXZ004"
  ArcFitTolerance = 1e-06
  AttachmentSupport = -> [XZ_Plane023]
  FullyConstrained = true
  MakeInternals = false
  MapMode = 5
  Placement = pos=(0,0,0) rot=(1,0,0;1.5708rad)
  sketch-geometry (11):
    g0: LineSegment StartX=95.8447 StartY=-2 StartZ=0 EndX=84.2977 EndY=18 EndZ=0
    g1: LineSegment [constr] StartX=84.2977 StartY=18 StartZ=0 EndX=85.6077 EndY=18 EndZ=0
    g2: LineSegment StartX=85.6077 StartY=18 StartZ=0 EndX=97.1547 EndY=-2 EndZ=0
    g3: LineSegment StartX=84.2977 StartY=18 StartZ=0 EndX=85.6077 EndY=18.7563 EndZ=0
    g4: LineSegment StartX=85.6077 StartY=18.7563 StartZ=0 EndX=85.6077 EndY=18 EndZ=0
    g5: LineSegment StartX=66.6654 StartY=48.54 StartZ=0 EndX=78.2124 EndY=28.54 EndZ=0
    g6: LineSegment StartX=78.2124 StartY=28.54 StartZ=0 EndX=79.5224 EndY=28.54 EndZ=0
    g7: LineSegment StartX=79.5224 StartY=28.54 StartZ=0 EndX=67.9754 EndY=48.54 EndZ=0
    g8: LineSegment StartX=95.8447 StartY=-2 StartZ=0 EndX=97.1547 EndY=-2 EndZ=0
    g9: LineSegment [constr] StartX=0 StartY=0 StartZ=0 EndX=96 EndY=0 EndZ=0
    g10: LineSegment StartX=66.6654 StartY=48.54 StartZ=0 EndX=67.9754 EndY=48.54 EndZ=0
  constraints (31):
    c: Coincident(g0,g1)
    c: Coincident(g1,g2)
    c: Parallel(g0,g2)
    c: Angle(g0,g-1) = 1.0472
    c: Horizontal(g1)
    c: DistanceY(g0) = 18
    c: Coincident(g4,g3)
    c: Coincident(g4,g1)
    c: Vertical(g4)
    c: Coincident(g6,g5)
    c: Coincident(g7,g6)
    c: Horizontal(g6)
    c: Tangent(g7,g2)
    c: Equal(g1,g6)
    c: Equal(g0,g5)
    c: Parallel(g5,g7)
    c: Coincident(g8,g0)
    c: Coincident(g2,g8)
    c: Horizontal(g8)
    c: DistanceX(g8,g8) = 1.31
    c: Coincident(g9,g-1)
    c: PointOnObject(g9,g-1)
    c: DistanceX(g9,g9) = 96
    c: DistanceY(g0,g9) = 2
    c: Coincident(g10,g5)
    c: Coincident(g10,g7)
    c: Horizontal(g10)
    c: DistanceY(g5) = 48.54
    c: PointOnObject(g9,g2)
    c: Coincident(g3,g0)
    c: Perpendicular(g0,g3)
FEATURE [PartDesign::SubShapeBinder] Binder042  label="BinderESP001"
  BindCopyOnChange = 0
  BindMode = 0
  ClaimChildren = false
  Context = -> Body014 [Binder042.]
  Fuse = false
  MakeFace = true
  OffsetFill = false
  OffsetIntersection = false
  OffsetJoinType = 0
  OffsetOpenResult = false
  PartialLoad = false
  Refine = true
  Relative = true
  Support = -> [Link005[Pad032.]]
  _Version = 2
FEATURE [Sketcher::SketchObject] Sketch073
  ArcFitTolerance = 1e-06
  AttachmentSupport = -> [XY_Plane010]
  FullyConstrained = true
  MakeInternals = false
  MapMode = 5
  sketch-geometry (5):
    g0: LineSegment StartX=-11.5 StartY=93.25 StartZ=0 EndX=-11.5 EndY=85.75 EndZ=0
    g1: LineSegment StartX=-11.5 StartY=85.75 StartZ=0 EndX=11.5 EndY=85.75 EndZ=0
    g2: LineSegment StartX=11.5 StartY=85.75 StartZ=0 EndX=11.5 EndY=93.25 EndZ=0
    g3: LineSegment StartX=11.5 StartY=93.25 StartZ=0 EndX=-11.5 EndY=93.25 EndZ=0
    g4: GeomPoint [constr] X=0 Y=89.5 Z=0
  constraints (13):
    c: Coincident(g0,g1)
    c: Coincident(g1,g2)
    c: Coincident(g2,g3)
    c: Coincident(g3,g0)
    c: Vertical(g0)
    c: Vertical(g2)
    c: Horizontal(g1)
    c: Horizontal(g3)
    c: Symmetric(g2,g0,g4)
    c: PointOnObject(g4,g-2)
    c: DistanceX(g3,g3) = 23
    c: DistanceY(g2,g2) = 7.5
    c: DistanceY(g4) = 89.5
FEATURE [Sketcher::SketchObject] Sketch074
  ArcFitTolerance = 1e-06
  AttachmentSupport = -> [XY_Plane010]
  FullyConstrained = true
  MakeInternals = false
  MapMode = 5
  sketch-geometry (5):
    g0: LineSegment StartX=-12.5 StartY=87.5 StartZ=0 EndX=12.5 EndY=87.5 EndZ=0
    g1: LineSegment StartX=12.5 StartY=87.5 StartZ=0 EndX=12.5 EndY=92.5 EndZ=0
    g2: LineSegment StartX=12.5 StartY=92.5 StartZ=0 EndX=-12.5 EndY=92.5 EndZ=0
    g3: LineSegment StartX=-12.5 StartY=92.5 StartZ=0 EndX=-12.5 EndY=87.5 EndZ=0
    g4: GeomPoint [constr] X=0 Y=90 Z=0
  constraints (13):
    c: Coincident(g0,g1)
    c: Coincident(g1,g2)
    c: Coincident(g2,g3)
    c: Coincident(g3,g0)
    c: Horizontal(g0)
    c: Horizontal(g2)
    c: Vertical(g1)
    c: Vertical(g3)
    c: Symmetric(g2,g0,g4)
    c: Distance(g1,g3) = 25
    c: Distance(g0,g2) = 5
    c: PointOnObject(g4,g-2)
    c: DistanceY(g4) = 90
FEATURE [PartDesign::SubShapeBinder] Binder045
  BindCopyOnChange = 0
  BindMode = 0
  ClaimChildren = false
  Context = -> Body010 [Binder045.]
  Fuse = false
  MakeFace = true
  Offset = 6
  OffsetFill = true
  OffsetIntersection = false
  OffsetJoinType = 1
  OffsetOpenResult = false
  PartialLoad = false
  Placement = pos=(0,0,-0.1) rot=(0,0,1;0rad)
  Refine = true
  Relative = true
  Support = -> [Sketch037]
  _Version = 2
FEATURE [PartDesign::SubShapeBinder] Binder046
  BindCopyOnChange = 0
  BindMode = 0
  ClaimChildren = false
  Context = -> Body010 [Binder046.]
  Fuse = false
  MakeFace = true
  OffsetFill = false
  OffsetIntersection = false
  OffsetJoinType = 0
  OffsetOpenResult = false
  PartialLoad = false
  Refine = true
  Relative = true
  Support = -> [Sketch054]
  _Version = 2
FEATURE [PartDesign::SubShapeBinder] Binder047  label="BinderUsb"
  BindCopyOnChange = 0
  BindMode = 0
  ClaimChildren = false
  Context = -> Body010 [Binder047.]
  Fuse = false
  MakeFace = true
  Offset = 0.15
  OffsetFill = false
  OffsetIntersection = false
  OffsetJoinType = 1
  OffsetOpenResult = false
  PartialLoad = false
  Placement = pos=(0,0,0.6) rot=(0,0,1;0rad)
  Refine = true
  Relative = true
  Support = -> [Boolean010[Face308]]
  _Version = 2
FEATURE [PartDesign::SubShapeBinder] Binder049
  BindCopyOnChange = 0
  BindMode = 0
  ClaimChildren = false
  Context = -> Body010 [Binder049.]
  Fuse = false
  MakeFace = true
  Offset = 0.1
  OffsetFill = false
  OffsetIntersection = false
  OffsetJoinType = 0
  OffsetOpenResult = false
  PartialLoad = false
  Refine = true
  Relative = true
  Support = -> [Pocket015[Face324]]
  _Version = 2
FEATURE [Sketcher::SketchObject] Sketch079
  ArcFitTolerance = 1e-06
  AttachmentSupport = -> [YZ_Plane014]
  FullyConstrained = true
  MakeInternals = false
  MapMode = 5
  Placement = pos=(0,0,0) rot=(0.57735,-0.57735,-0.57735;2.0944rad)
  sketch-geometry (8):
    g0: LineSegment StartX=92.9 StartY=0 StartZ=0 EndX=92.9 EndY=1.95 EndZ=0
    g1: LineSegment StartX=92.9 StartY=1.95 StartZ=0 EndX=92.0609 EndY=2.95 EndZ=0
    g2: LineSegment StartX=90.1891 StartY=2.95 StartZ=0 EndX=89.35 EndY=1.95 EndZ=0
    g3: LineSegment StartX=89.35 StartY=1.95 StartZ=0 EndX=89.35 EndY=1.75 EndZ=0
    g4: LineSegment StartX=89.35 StartY=1.75 StartZ=0 EndX=89.85 EndY=1.25 EndZ=0
    g5: LineSegment StartX=89.85 StartY=1.25 StartZ=0 EndX=89.85 EndY=0 EndZ=0
    g6: LineSegment StartX=89.85 StartY=0 StartZ=0 EndX=92.9 EndY=0 EndZ=0
    g7: LineSegment StartX=90.1891 StartY=2.95 StartZ=0 EndX=92.0609 EndY=2.95 EndZ=0
  constraints (24):
    c: Vertical(g0)
    c: Coincident(g0,g1)
    c: Coincident(g2,g3)
    c: Coincident(g3,g4)
    c: Coincident(g4,g5)
    c: PointOnObject(g5,g-1)
    c: Vertical(g5)
    c: Coincident(g5,g6)
    c: Coincident(g6,g0)
    c: Horizontal(g6)
    c: DistanceX(g5) = 89.85
    c: DistanceX(g4,g4) = 0.5
    c: Vertical(g3)
    c: Angle(g3,g2) = 2.44346
    c: Angle(g1,g0) = 2.44346
    c: DistanceX(g6,g6) = 3.05
    c: Coincident(g7,g2)
    c: Coincident(g7,g1)
    c: Horizontal(g7)
    c: DistanceY(g2,g2) = 1
    c: Horizontal(g0,g2)
    c: DistanceY(g3) = 1.75
    c: Angle(g4,g3) = 2.35619
    c: DistanceY(g3,g3) = 0.2
FEATURE [PartDesign::Groove] Groove
  Angle = 348
  Angle2 = 60
  Axis = (0,0,1)
  Base = (0,0,0)
  BaseFeature = -> Boolean012
  Midplane = true
  Profile = -> Sketch079
  ReferenceAxis = -> Sketch079 [V_Axis]
  Refine = true
  Suppressed = false
  Type = 0
FEATURE [PartDesign::Boolean] Boolean017  label="BooleanBrackets"
  BaseFeature = -> Groove
  Group = -> [Binder038]
  Refine = true
  Suppressed = false
  Type = 1
  UsePlacement = true
FEATURE [PartDesign::Boolean] Boolean018  label="BooleanESP001"
  BaseFeature = -> Boolean017
  Group = -> [Binder042]
  Refine = true
  Suppressed = false
  Type = 1
  UsePlacement = true
FEATURE [PartDesign::SubShapeBinder] Binder051  label="BinderSkin"
  BindCopyOnChange = 0
  BindMode = 0
  ClaimChildren = false
  Context = -> Body014 [Binder051.]
  Fuse = false
  MakeFace = true
  OffsetFill = false
  OffsetIntersection = false
  OffsetJoinType = 0
  OffsetOpenResult = false
  PartialLoad = false
  Refine = true
  Relative = true
  Support = -> [Body023]
  _Version = 2
FEATURE [Sketcher::SketchObject] Sketch081
  ArcFitTolerance = 1e-06
  AttachmentOffset = pos=(0,0,-8.5) rot=(0,0,1;0rad)
  AttachmentSupport = -> [XY_Plane010]
  FullyConstrained = true
  MakeInternals = false
  MapMode = 5
  Placement = pos=(0,0,-8.5) rot=(0,0,1;0rad)
  sketch-geometry (13):
    g0: Circle CenterX=-40.5 CenterY=-70.1481 CenterZ=0 NormalX=0 NormalY=0 NormalZ=1 AngleXU=0 Radius=4
    g1: LineSegment [constr] StartX=40.5 StartY=-70.1481 StartZ=0 EndX=81 EndY=-1.42e-14 EndZ=0
    g2: LineSegment [constr] StartX=81 StartY=-1.42e-14 StartZ=0 EndX=40.5 EndY=70.1481 EndZ=0
    g3: LineSegment [constr] StartX=40.5 StartY=70.1481 StartZ=0 EndX=-40.5 EndY=70.1481 EndZ=0
    g4: LineSegment [constr] StartX=-40.5 StartY=70.1481 StartZ=0 EndX=-81 EndY=4.26e-14 EndZ=0
    g5: LineSegment [constr] StartX=-81 StartY=4.26e-14 StartZ=0 EndX=-40.5 EndY=-70.1481 EndZ=0
    g6: LineSegment [constr] StartX=-40.5 StartY=-70.1481 StartZ=0 EndX=40.5 EndY=-70.1481 EndZ=0
    g7: Circle [constr] CenterX=0 CenterY=0 CenterZ=0 NormalX=0 NormalY=0 NormalZ=1 AngleXU=0 Radius=81
    g8: Circle CenterX=40.5 CenterY=-70.1481 CenterZ=0 NormalX=0 NormalY=0 NormalZ=1 AngleXU=0 Radius=4
    g9: Circle CenterX=81 CenterY=-1.42e-14 CenterZ=0 NormalX=0 NormalY=0 NormalZ=1 AngleXU=0 Radius=4
    g10: Circle CenterX=-81 CenterY=4.26e-14 CenterZ=0 NormalX=0 NormalY=0 NormalZ=1 AngleXU=0 Radius=4
    g11: Circle CenterX=-40.5 CenterY=70.1481 CenterZ=0 NormalX=0 NormalY=0 NormalZ=1 AngleXU=0 Radius=4
    g12: Circle CenterX=40.5 CenterY=70.1481 CenterZ=0 NormalX=0 NormalY=0 NormalZ=1 AngleXU=0 Radius=4
  constraints (28):
    c: Diameter(g0) = 8
    c: Coincident(g1,g2)
    c: Coincident(g2,g3)
    c: Coincident(g3,g4)
    c: Coincident(g4,g5)
    c: Coincident(g5,g6)
    c: Coincident(g6,g1)
    c: Equal(g1, g2-g6) x5
    c: PointOnObject(g1,g7)
    c: PointOnObject(g2,g7)
    c: PointOnObject(g3,g7)
    c: PointOnObject(g4,g7)
    c: PointOnObject(g5,g7)
    c: PointOnObject(g6,g7)
    c: Coincident(g7,g-1)
    c: Horizontal(g6)
    c: Coincident(g0,g5)
    c: Coincident(g8,g1)
    c: Coincident(g9,g1)
    c: Coincident(g10,g4)
    c: Coincident(g11,g3)
    c: Coincident(g12,g2)
    c: Equal(g12,g11)
    c: Equal(g11,g10)
    c: Equal(g10,g9)
    c: Equal(g9,g8)
    c: Equal(g8,g0)
    c: Diameter(g7) = 162
FEATURE [Sketcher::SketchObject] Sketch082
  ArcFitTolerance = 1e-06
  AttachmentSupport = -> [XZ_Plane023]
  FullyConstrained = false
  MakeInternals = false
  MapMode = 5
  Placement = pos=(0,0,0) rot=(1,0,0;1.5708rad)
  sketch-geometry (8):
    g0: LineSegment StartX=71.1806 StartY=47.5387 StartZ=0 EndX=55.3726 EndY=47.5387 EndZ=0
    g1: LineSegment StartX=55.3726 StartY=47.5387 StartZ=0 EndX=55.3726 EndY=52.9897 EndZ=0
    g2: LineSegment StartX=55.3726 StartY=52.9897 StartZ=0 EndX=78.8121 EndY=52.9897 EndZ=0
    g3: LineSegment StartX=78.8121 StartY=52.9897 StartZ=0 EndX=111.518 EndY=0 EndZ=0
    g4: LineSegment StartX=111.518 StartY=0 StartZ=0 EndX=92.576 EndY=-7.517 EndZ=0
    g5: LineSegment StartX=92.576 StartY=-7.517 StartZ=0 EndX=92.1961 EndY=-0.945236 EndZ=0
    g6: LineSegment StartX=92.1961 StartY=-0.945236 StartZ=0 EndX=98.3119 EndY=-0.945236 EndZ=0
    g7: LineSegment StartX=98.3119 StartY=-0.945236 StartZ=0 EndX=71.1806 EndY=47.5387 EndZ=0
  constraints (12):
    c: Horizontal(g0)
    c: Coincident(g0,g1)
    c: Vertical(g1)
    c: Coincident(g1,g2)
    c: Horizontal(g2)
    c: Coincident(g2,g3)
    c: Coincident(g3,g4)
    c: Coincident(g4,g5)
    c: Coincident(g5,g6)
    c: Horizontal(g6)
    c: Coincident(g6,g7)
    c: Coincident(g7,g0)
FEATURE [PartDesign::Revolution] Revolution010
  Angle = 360
  Angle2 = 60
  Axis = (0,2e-16,1)
  Base = (0,0,0)
  Placement = pos=(0,0,0) rot=(1,0,0;1.5708rad)
  Profile = -> Sketch082
  ReferenceAxis = -> Sketch082 [V_Axis]
  Refine = true
  Reversed = true
  Suppressed = false
  Type = 0
FEATURE [PartDesign::Revolution] Revolution007
  Angle = 2.25
  Angle2 = 60
  Axis = (0,2e-16,1)
  Base = (0,0,0)
  BaseFeature = -> Revolution010
  Midplane = true
  Placement = pos=(0,0,0) rot=(1,0,0;1.5708rad)
  Profile = -> Sketch070
  ReferenceAxis = -> Sketch070 [V_Axis]
  Refine = true
  Reversed = true
  Suppressed = false
  Type = 0
FEATURE [PartDesign::PolarPattern] PolarPattern013
  Angle = 360
  Axis = -> Z_Axis023
  BaseFeature = -> Revolution007
  Mode = 0
  Occurrences = 8
  Offset = 120
  Originals = -> [Revolution007]
  Placement = pos=(0,0,0) rot=(1,0,0;1.5708rad)
  Refine = true
  Suppressed = false
  TransformMode = 0
FEATURE [Part::Feature] path1651
  shape: bbox 1.28 x 3.582 x 2e-07 mm, 1 faces, 0 solids (baked)
FEATURE [Part::Feature] path1652
  shape: bbox 1.234 x 2.86 x 2e-07 mm, 1 faces, 0 solids (baked)
FEATURE [Part::Feature] path1653
  shape: bbox 1.062 x 1.166 x 2e-07 mm, 1 faces, 0 solids (baked)
FEATURE [Part::Feature] path1654
  shape: bbox 0.6914 x 0.3982 x 2e-07 mm, 1 faces, 0 solids (baked)
FEATURE [Part::Feature] path1655
  shape: bbox 2.653 x 1.574 x 2e-07 mm, 1 faces, 0 solids (baked)
FEATURE [Part::Feature] path1656
  shape: bbox 0.288 x 0.1623 x 2e-07 mm, 1 faces, 0 solids (baked)
FEATURE [Part::Feature] path1657
  shape: bbox 1.537 x 5.354 x 2e-07 mm, 1 faces, 0 solids (baked)
FEATURE [Part::Feature] path1658
  shape: bbox 0.4343 x 0.1546 x 2e-07 mm, 1 faces, 0 solids (baked)
FEATURE [Part::Feature] path1659
  shape: bbox 1.449 x 4.864 x 2e-07 mm, 2 faces, 0 solids (baked)
FEATURE [Part::Feature] path1660
  shape: bbox 0.7826 x 2.673 x 2e-07 mm, 1 faces, 0 solids (baked)
FEATURE [Part::Feature] path1661
  shape: bbox 3.902 x 2.313 x 2e-07 mm, 1 faces, 0 solids (baked)
FEATURE [Part::Feature] path1662
  shape: bbox 0.4693 x 0.6049 x 2e-07 mm, 1 faces, 0 solids (baked)
FEATURE [Part::Feature] path1663
  shape: bbox 0.8046 x 0.9991 x 2e-07 mm, 1 faces, 0 solids (baked)
FEATURE [Part::Feature] path1664
  shape: bbox 0.3112 x 0.1613 x 2e-07 mm, 1 faces, 0 solids (baked)
FEATURE [Part::Feature] path1665
  shape: bbox 1.268 x 3.39 x 2e-07 mm, 1 faces, 0 solids (baked)
FEATURE [Part::Feature] path1938
  shape: bbox 4.882 x 3.498 x 2e-07 mm, 1 faces, 0 solids (baked)
FEATURE [Part::Feature] path1942
  shape: bbox 4.828 x 3.501 x 2e-07 mm, 1 faces, 0 solids (baked)
FEATURE [Part::Feature] path1944
  shape: bbox 3.961 x 3.506 x 2e-07 mm, 1 faces, 0 solids (baked)
FEATURE [Sketcher::SketchObject] Sketch083
  ArcFitTolerance = 1e-06
  AttachmentSupport = -> [CompoundFilter]
  FullyConstrained = false
  MakeInternals = false
  Placement = pos=(7.11e-14,1.22277e-06,21.6123) rot=(0,0,1;2.35619rad)
  sketch-geometry (197):
    g0: BSplineCurve PolesCount=2 KnotsCount=2 Degree=1 IsPeriodic=0
    g1: BSplineCurve PolesCount=2 KnotsCount=2 Degree=1 IsPeriodic=0
    g2: BSplineCurve PolesCount=2 KnotsCount=2 Degree=1 IsPeriodic=0
    g3: BSplineCurve PolesCount=2 KnotsCount=2 Degree=1 IsPeriodic=0
    g4: BSplineCurve PolesCount=4 KnotsCount=2 Degree=3 IsPeriodic=0
    g5: BSplineCurve PolesCount=2 KnotsCount=2 Degree=1 IsPeriodic=0
    g6: BSplineCurve PolesCount=2 KnotsCount=2 Degree=1 IsPeriodic=0
    g7: BSplineCurve PolesCount=2 KnotsCount=2 Degree=1 IsPeriodic=0
    g8: BSplineCurve PolesCount=4 KnotsCount=2 Degree=3 IsPeriodic=0
    g9: BSplineCurve PolesCount=4 KnotsCount=2 Degree=3 IsPeriodic=0
    g10: BSplineCurve PolesCount=4 KnotsCount=2 Degree=3 IsPeriodic=0
    g11: BSplineCurve PolesCount=4 KnotsCount=2 Degree=3 IsPeriodic=0
    g12: BSplineCurve PolesCount=4 KnotsCount=2 Degree=3 IsPeriodic=0
    g13: BSplineCurve PolesCount=4 KnotsCount=2 Degree=3 IsPeriodic=0
    g14: BSplineCurve PolesCount=4 KnotsCount=2 Degree=3 IsPeriodic=0
    g15: BSplineCurve PolesCount=4 KnotsCount=2 Degree=3 IsPeriodic=0
    g16: BSplineCurve PolesCount=4 KnotsCount=2 Degree=3 IsPeriodic=0
    g17: BSplineCurve PolesCount=4 KnotsCount=2 Degree=3 IsPeriodic=0
    g18: BSplineCurve PolesCount=4 KnotsCount=2 Degree=3 IsPeriodic=0
    g19: BSplineCurve PolesCount=4 KnotsCount=2 Degree=3 IsPeriodic=0
    g20: BSplineCurve PolesCount=4 KnotsCount=2 Degree=3 IsPeriodic=0
    g21: BSplineCurve PolesCount=4 KnotsCount=2 Degree=3 IsPeriodic=0
    g22: BSplineCurve PolesCount=4 KnotsCount=2 Degree=3 IsPeriodic=0
    g23: BSplineCurve PolesCount=4 KnotsCount=2 Degree=3 IsPeriodic=0
    g24: BSplineCurve PolesCount=4 KnotsCount=2 Degree=3 IsPeriodic=0
    g25: BSplineCurve PolesCount=4 KnotsCount=2 Degree=3 IsPeriodic=0
    g26: BSplineCurve PolesCount=4 KnotsCount=2 Degree=3 IsPeriodic=0
    g27: BSplineCurve PolesCount=4 KnotsCount=2 Degree=3 IsPeriodic=0
    g28: BSplineCurve PolesCount=4 KnotsCount=2 Degree=3 IsPeriodic=0
    g29: BSplineCurve PolesCount=4 KnotsCount=2 Degree=3 IsPeriodic=0
    g30: BSplineCurve PolesCount=4 KnotsCount=2 Degree=3 IsPeriodic=0
    g31: BSplineCurve PolesCount=4 KnotsCount=2 Degree=3 IsPeriodic=0
    g32: BSplineCurve PolesCount=4 KnotsCount=2 Degree=3 IsPeriodic=0
    g33: BSplineCurve PolesCount=4 KnotsCount=2 Degree=3 IsPeriodic=0
    g34: BSplineCurve PolesCount=4 KnotsCount=2 Degree=3 IsPeriodic=0
    g35: BSplineCurve PolesCount=4 KnotsCount=2 Degree=3 IsPeriodic=0
    g36: BSplineCurve PolesCount=4 KnotsCount=2 Degree=3 IsPeriodic=0
    g37: BSplineCurve PolesCount=4 KnotsCount=2 Degree=3 IsPeriodic=0
    g38: BSplineCurve PolesCount=4 KnotsCount=2 Degree=3 IsPeriodic=0
    g39: BSplineCurve PolesCount=4 KnotsCount=2 Degree=3 IsPeriodic=0
    g40: BSplineCurve PolesCount=4 KnotsCount=2 Degree=3 IsPeriodic=0
    g41: BSplineCurve PolesCount=4 KnotsCount=2 Degree=3 IsPeriodic=0
    g42: BSplineCurve PolesCount=4 KnotsCount=2 Degree=3 IsPeriodic=0
    g43: BSplineCurve PolesCount=4 KnotsCount=2 Degree=3 IsPeriodic=0
    g44: BSplineCurve PolesCount=4 KnotsCount=2 Degree=3 IsPeriodic=0
    g45: BSplineCurve PolesCount=4 KnotsCount=2 Degree=3 IsPeriodic=0
    g46: BSplineCurve PolesCount=4 KnotsCount=2 Degree=3 IsPeriodic=0
    g47: BSplineCurve PolesCount=4 KnotsCount=2 Degree=3 IsPeriodic=0
    g48: BSplineCurve PolesCount=4 KnotsCount=2 Degree=3 IsPeriodic=0
    g49: BSplineCurve PolesCount=4 KnotsCount=2 Degree=3 IsPeriodic=0
    g50: BSplineCurve PolesCount=4 KnotsCount=2 Degree=3 IsPeriodic=0
    g51: BSplineCurve PolesCount=4 KnotsCount=2 Degree=3 IsPeriodic=0
    g52: BSplineCurve PolesCount=4 KnotsCount=2 Degree=3 IsPeriodic=0
    g53: BSplineCurve PolesCount=4 KnotsCount=2 Degree=3 IsPeriodic=0
    g54: BSplineCurve PolesCount=4 KnotsCount=2 Degree=3 IsPeriodic=0
    g55: BSplineCurve PolesCount=4 KnotsCount=2 Degree=3 IsPeriodic=0
    g56: BSplineCurve PolesCount=4 KnotsCount=2 Degree=3 IsPeriodic=0
    g57: BSplineCurve PolesCount=4 KnotsCount=2 Degree=3 IsPeriodic=0
    g58: BSplineCurve PolesCount=4 KnotsCount=2 Degree=3 IsPeriodic=0
    g59: BSplineCurve PolesCount=4 KnotsCount=2 Degree=3 IsPeriodic=0
    g60: BSplineCurve PolesCount=4 KnotsCount=2 Degree=3 IsPeriodic=0
    g61: BSplineCurve PolesCount=4 KnotsCount=2 Degree=3 IsPeriodic=0
    g62: BSplineCurve PolesCount=4 KnotsCount=2 Degree=3 IsPeriodic=0
    g63: BSplineCurve PolesCount=4 KnotsCount=2 Degree=3 IsPeriodic=0
    g64: BSplineCurve PolesCount=4 KnotsCount=2 Degree=3 IsPeriodic=0
    g65: BSplineCurve PolesCount=4 KnotsCount=2 Degree=3 IsPeriodic=0
    g66: BSplineCurve PolesCount=4 KnotsCount=2 Degree=3 IsPeriodic=0
    g67: BSplineCurve PolesCount=4 KnotsCount=2 Degree=3 IsPeriodic=0
    g68: BSplineCurve PolesCount=4 KnotsCount=2 Degree=3 IsPeriodic=0
    g69: BSplineCurve PolesCount=4 KnotsCount=2 Degree=3 IsPeriodic=0
    g70: BSplineCurve PolesCount=4 KnotsCount=2 Degree=3 IsPeriodic=0
    g71: BSplineCurve PolesCount=4 KnotsCount=2 Degree=3 IsPeriodic=0
    g72: BSplineCurve PolesCount=4 KnotsCount=2 Degree=3 IsPeriodic=0
    g73: BSplineCurve PolesCount=4 KnotsCount=2 Degree=3 IsPeriodic=0
    g74: BSplineCurve PolesCount=4 KnotsCount=2 Degree=3 IsPeriodic=0
    g75: BSplineCurve PolesCount=4 KnotsCount=2 Degree=3 IsPeriodic=0
    g76: BSplineCurve PolesCount=4 KnotsCount=2 Degree=3 IsPeriodic=0
    g77: BSplineCurve PolesCount=4 KnotsCount=2 Degree=3 IsPeriodic=0
    g78: BSplineCurve PolesCount=4 KnotsCount=2 Degree=3 IsPeriodic=0
    g79: BSplineCurve PolesCount=4 KnotsCount=2 Degree=3 IsPeriodic=0
    g80: BSplineCurve PolesCount=4 KnotsCount=2 Degree=3 IsPeriodic=0
    g81: BSplineCurve PolesCount=4 KnotsCount=2 Degree=3 IsPeriodic=0
    g82: BSplineCurve PolesCount=4 KnotsCount=2 Degree=3 IsPeriodic=0
    g83: BSplineCurve PolesCount=4 KnotsCount=2 Degree=3 IsPeriodic=0
    g84: BSplineCurve PolesCount=4 KnotsCount=2 Degree=3 IsPeriodic=0
    g85: BSplineCurve PolesCount=4 KnotsCount=2 Degree=3 IsPeriodic=0
    g86: BSplineCurve PolesCount=4 KnotsCount=2 Degree=3 IsPeriodic=0
    g87: BSplineCurve PolesCount=4 KnotsCount=2 Degree=3 IsPeriodic=0
    g88: BSplineCurve PolesCount=4 KnotsCount=2 Degree=3 IsPeriodic=0
    g89: BSplineCurve PolesCount=4 KnotsCount=2 Degree=3 IsPeriodic=0
    g90: BSplineCurve PolesCount=4 KnotsCount=2 Degree=3 IsPeriodic=0
    g91: BSplineCurve PolesCount=4 KnotsCount=2 Degree=3 IsPeriodic=0
    g92: BSplineCurve PolesCount=4 KnotsCount=2 Degree=3 IsPeriodic=0
    g93: BSplineCurve PolesCount=4 KnotsCount=2 Degree=3 IsPeriodic=0
    g94: BSplineCurve PolesCount=4 KnotsCount=2 Degree=3 IsPeriodic=0
    g95: BSplineCurve PolesCount=4 KnotsCount=2 Degree=3 IsPeriodic=0
    g96: BSplineCurve PolesCount=4 KnotsCount=2 Degree=3 IsPeriodic=0
    g97: BSplineCurve PolesCount=4 KnotsCount=2 Degree=3 IsPeriodic=0
    g98: BSplineCurve PolesCount=4 KnotsCount=2 Degree=3 IsPeriodic=0
    g99: BSplineCurve PolesCount=4 KnotsCount=2 Degree=3 IsPeriodic=0
    g100: BSplineCurve PolesCount=4 KnotsCount=2 Degree=3 IsPeriodic=0
    g101: BSplineCurve PolesCount=4 KnotsCount=2 Degree=3 IsPeriodic=0
    g102: BSplineCurve PolesCount=4 KnotsCount=2 Degree=3 IsPeriodic=0
    g103: BSplineCurve PolesCount=4 KnotsCount=2 Degree=3 IsPeriodic=0
    g104: BSplineCurve PolesCount=4 KnotsCount=2 Degree=3 IsPeriodic=0
    g105: BSplineCurve PolesCount=4 KnotsCount=2 Degree=3 IsPeriodic=0
    g106: BSplineCurve PolesCount=4 KnotsCount=2 Degree=3 IsPeriodic=0
    g107: BSplineCurve PolesCount=4 KnotsCount=2 Degree=3 IsPeriodic=0
    g108: BSplineCurve PolesCount=4 KnotsCount=2 Degree=3 IsPeriodic=0
    g109: BSplineCurve PolesCount=4 KnotsCount=2 Degree=3 IsPeriodic=0
    g110: BSplineCurve PolesCount=4 KnotsCount=2 Degree=3 IsPeriodic=0
    g111: BSplineCurve PolesCount=4 KnotsCount=2 Degree=3 IsPeriodic=0
    g112: BSplineCurve PolesCount=4 KnotsCount=2 Degree=3 IsPeriodic=0
    g113: BSplineCurve PolesCount=4 KnotsCount=2 Degree=3 IsPeriodic=0
    g114: BSplineCurve PolesCount=4 KnotsCount=2 Degree=3 IsPeriodic=0
    g115: BSplineCurve PolesCount=4 KnotsCount=2 Degree=3 IsPeriodic=0
    g116: BSplineCurve PolesCount=4 KnotsCount=2 Degree=3 IsPeriodic=0
    g117: BSplineCurve PolesCount=4 KnotsCount=2 Degree=3 IsPeriodic=0
    g118: BSplineCurve PolesCount=4 KnotsCount=2 Degree=3 IsPeriodic=0
    g119: BSplineCurve PolesCount=4 KnotsCount=2 Degree=3 IsPeriodic=0
    g120: BSplineCurve PolesCount=4 KnotsCount=2 Degree=3 IsPeriodic=0
    g121: BSplineCurve PolesCount=4 KnotsCount=2 Degree=3 IsPeriodic=0
    g122: BSplineCurve PolesCount=4 KnotsCount=2 Degree=3 IsPeriodic=0
    g123: BSplineCurve PolesCount=4 KnotsCount=2 Degree=3 IsPeriodic=0
    g124: BSplineCurve PolesCount=4 KnotsCount=2 Degree=3 IsPeriodic=0
    g125: BSplineCurve PolesCount=4 KnotsCount=2 Degree=3 IsPeriodic=0
    g126: BSplineCurve PolesCount=4 KnotsCount=2 Degree=3 IsPeriodic=0
    g127: BSplineCurve PolesCount=4 KnotsCount=2 Degree=3 IsPeriodic=0
    g128: BSplineCurve PolesCount=4 KnotsCount=2 Degree=3 IsPeriodic=0
    g129: BSplineCurve PolesCount=4 KnotsCount=2 Degree=3 IsPeriodic=0
    g130: BSplineCurve PolesCount=4 KnotsCount=2 Degree=3 IsPeriodic=0
    g131: BSplineCurve PolesCount=4 KnotsCount=2 Degree=3 IsPeriodic=0
    g132: BSplineCurve PolesCount=4 KnotsCount=2 Degree=3 IsPeriodic=0
    g133: BSplineCurve PolesCount=4 KnotsCount=2 Degree=3 IsPeriodic=0
    g134: BSplineCurve PolesCount=4 KnotsCount=2 Degree=3 IsPeriodic=0
    g135: BSplineCurve PolesCount=4 KnotsCount=2 Degree=3 IsPeriodic=0
    g136: BSplineCurve PolesCount=4 KnotsCount=2 Degree=3 IsPeriodic=0
    g137: BSplineCurve PolesCount=4 KnotsCount=2 Degree=3 IsPeriodic=0
    g138: BSplineCurve PolesCount=4 KnotsCount=2 Degree=3 IsPeriodic=0
    g139: BSplineCurve PolesCount=4 KnotsCount=2 Degree=3 IsPeriodic=0
    g140: BSplineCurve PolesCount=4 KnotsCount=2 Degree=3 IsPeriodic=0
    g141: BSplineCurve PolesCount=4 KnotsCount=2 Degree=3 IsPeriodic=0
    g142: BSplineCurve PolesCount=4 KnotsCount=2 Degree=3 IsPeriodic=0
    g143: BSplineCurve PolesCount=4 KnotsCount=2 Degree=3 IsPeriodic=0
    g144: BSplineCurve PolesCount=4 KnotsCount=2 Degree=3 IsPeriodic=0
    g145: BSplineCurve PolesCount=4 KnotsCount=2 Degree=3 IsPeriodic=0
    g146: BSplineCurve PolesCount=4 KnotsCount=2 Degree=3 IsPeriodic=0
    g147: BSplineCurve PolesCount=4 KnotsCount=2 Degree=3 IsPeriodic=0
    g148: BSplineCurve PolesCount=4 KnotsCount=2 Degree=3 IsPeriodic=0
    g149: BSplineCurve PolesCount=4 KnotsCount=2 Degree=3 IsPeriodic=0
    g150: BSplineCurve PolesCount=4 KnotsCount=2 Degree=3 IsPeriodic=0
    g151: BSplineCurve PolesCount=4 KnotsCount=2 Degree=3 IsPeriodic=0
    g152: BSplineCurve PolesCount=4 KnotsCount=2 Degree=3 IsPeriodic=0
    g153: BSplineCurve PolesCount=4 KnotsCount=2 Degree=3 IsPeriodic=0
    g154: BSplineCurve PolesCount=4 KnotsCount=2 Degree=3 IsPeriodic=0
    g155: BSplineCurve PolesCount=4 KnotsCount=2 Degree=3 IsPeriodic=0
    g156: BSplineCurve PolesCount=4 KnotsCount=2 Degree=3 IsPeriodic=0
    g157: BSplineCurve PolesCount=4 KnotsCount=2 Degree=3 IsPeriodic=0
    g158: BSplineCurve PolesCount=4 KnotsCount=2 Degree=3 IsPeriodic=0
    g159: BSplineCurve PolesCount=4 KnotsCount=2 Degree=3 IsPeriodic=0
    g160: BSplineCurve PolesCount=4 KnotsCount=2 Degree=3 IsPeriodic=0
    g161: BSplineCurve PolesCount=4 KnotsCount=2 Degree=3 IsPeriodic=0
    g162: BSplineCurve PolesCount=4 KnotsCount=2 Degree=3 IsPeriodic=0
    g163: BSplineCurve PolesCount=4 KnotsCount=2 Degree=3 IsPeriodic=0
    g164: BSplineCurve PolesCount=4 KnotsCount=2 Degree=3 IsPeriodic=0
    g165: BSplineCurve PolesCount=2 KnotsCount=2 Degree=1 IsPeriodic=0
    g166: BSplineCurve PolesCount=4 KnotsCount=2 Degree=3 IsPeriodic=0
    g167: BSplineCurve PolesCount=2 KnotsCount=2 Degree=1 IsPeriodic=0
    g168: BSplineCurve PolesCount=2 KnotsCount=2 Degree=1 IsPeriodic=0
    g169: BSplineCurve PolesCount=2 KnotsCount=2 Degree=1 IsPeriodic=0
    g170: BSplineCurve PolesCount=4 KnotsCount=2 Degree=3 IsPeriodic=0
    g171: BSplineCurve PolesCount=2 KnotsCount=2 Degree=1 IsPeriodic=0
    g172: BSplineCurve PolesCount=2 KnotsCount=2 Degree=1 IsPeriodic=0
    g173: BSplineCurve PolesCount=2 KnotsCount=2 Degree=1 IsPeriodic=0
    g174: BSplineCurve PolesCount=2 KnotsCount=2 Degree=1 IsPeriodic=0
    g175: BSplineCurve PolesCount=2 KnotsCount=2 Degree=1 IsPeriodic=0
    g176: BSplineCurve PolesCount=2 KnotsCount=2 Degree=1 IsPeriodic=0
    g177: BSplineCurve PolesCount=2 KnotsCount=2 Degree=1 IsPeriodic=0
    g178: BSplineCurve PolesCount=2 KnotsCount=2 Degree=1 IsPeriodic=0
    g179: BSplineCurve PolesCount=4 KnotsCount=2 Degree=3 IsPeriodic=0
    g180: BSplineCurve PolesCount=2 KnotsCount=2 Degree=1 IsPeriodic=0
    g181: BSplineCurve PolesCount=2 KnotsCount=2 Degree=1 IsPeriodic=0
    g182: BSplineCurve PolesCount=2 KnotsCount=2 Degree=1 IsPeriodic=0
    g183: BSplineCurve PolesCount=2 KnotsCount=2 Degree=1 IsPeriodic=0
    g184: BSplineCurve PolesCount=2 KnotsCount=2 Degree=1 IsPeriodic=0
    g185: BSplineCurve PolesCount=4 KnotsCount=2 Degree=3 IsPeriodic=0
    g186: BSplineCurve PolesCount=2 KnotsCount=2 Degree=1 IsPeriodic=0
    g187: BSplineCurve PolesCount=2 KnotsCount=2 Degree=1 IsPeriodic=0
    g188: BSplineCurve PolesCount=2 KnotsCount=2 Degree=1 IsPeriodic=0
    g189: BSplineCurve PolesCount=4 KnotsCount=2 Degree=3 IsPeriodic=0
    g190: BSplineCurve PolesCount=2 KnotsCount=2 Degree=1 IsPeriodic=0
    g191: BSplineCurve PolesCount=4 KnotsCount=2 Degree=3 IsPeriodic=0
    g192: BSplineCurve PolesCount=2 KnotsCount=2 Degree=1 IsPeriodic=0
    g193: LineSegment [constr] StartX=-100 StartY=5.5 StartZ=0 EndX=-100 EndY=-16.5 EndZ=0
    g194: LineSegment [constr] StartX=-100 StartY=-16.5 StartZ=0 EndX=117 EndY=-16.5 EndZ=0
    g195: LineSegment [constr] StartX=117 StartY=-16.5 StartZ=0 EndX=117 EndY=5.5 EndZ=0
    g196: LineSegment [constr] StartX=117 StartY=5.5 StartZ=0 EndX=-100 EndY=5.5 EndZ=0
  constraints (205):
    c: Coincident(g0,g1)
    c: Coincident(g1,g2)
    c: Coincident(g2,g3)
    c: Coincident(g3,g4)
    c: Coincident(g4,g5)
    c: Coincident(g5,g6)
    c: Coincident(g6,g7)
    c: Coincident(g7,g0)
    c: Coincident(g8,g9)
    c: Coincident(g9,g10)
    c: Coincident(g10,g11)
    c: Coincident(g11,g12)
    c: Coincident(g12,g13)
    c: Coincident(g13,g14)
    c: Coincident(g14,g15)
    c: Coincident(g15,g16)
    c: Coincident(g16,g17)
    c: Coincident(g17,g18)
    c: Coincident(g18,g19)
    c: Coincident(g19,g20)
    c: Coincident(g20,g21)
    c: Coincident(g21,g22)
    c: Coincident(g23,g24)
    c: Coincident(g24,g25)
    c: Coincident(g25,g26)
    c: Coincident(g26,g27)
    c: Coincident(g27,g28)
    c: Coincident(g28,g29)
    c: Coincident(g29,g30)
    c: Coincident(g30,g31)
    c: Coincident(g31,g32)
    c: Coincident(g32,g33)
    c: Coincident(g33,g34)
    c: Coincident(g35,g36)
    c: Coincident(g36,g37)
    c: Coincident(g37,g38)
    c: Coincident(g38,g39)
    c: Coincident(g39,g40)
    c: Coincident(g40,g41)
    c: Coincident(g41,g42)
    c: Coincident(g42,g43)
    c: Coincident(g43,g44)
    c: Coincident(g45,g46)
    c: Coincident(g46,g47)
    c: Coincident(g47,g48)
    c: Coincident(g49,g50)
    c: Coincident(g50,g51)
    c: Coincident(g51,g52)
    c: Coincident(g52,g53)
    c: Coincident(g53,g54)
    c: Coincident(g54,g55)
    c: Coincident(g55,g56)
    c: Coincident(g56,g57)
    c: Coincident(g57,g58)
    c: Coincident(g58,g59)
    c: Coincident(g59,g60)
    c: Coincident(g60,g61)
    c: Coincident(g61,g62)
    c: Coincident(g62,g63)
    c: Coincident(g63,g64)
    c: Coincident(g64,g49)
    c: Coincident(g65,g66)
    c: Coincident(g66,g67)
    c: Coincident(g67,g65)
    c: Coincident(g68,g69)
    c: Coincident(g69,g70)
    c: Coincident(g70,g71)
    c: Coincident(g71,g72)
    c: Coincident(g72,g73)
    c: Coincident(g73,g74)
    c: Coincident(g74,g75)
    c: Coincident(g75,g76)
    c: Coincident(g76,g77)
    c: Coincident(g77,g78)
    c: Coincident(g78,g79)
    c: Coincident(g79,g80)
    c: Coincident(g80,g81)
    c: Coincident(g81,g82)
    c: Coincident(g82,g83)
    c: Coincident(g83,g84)
    c: Coincident(g84,g85)
    c: Coincident(g85,g68)
    c: Coincident(g86,g87)
    c: Coincident(g87,g88)
    c: Coincident(g88,g89)
    c: Coincident(g89,g86)
    c: Coincident(g90,g91)
    c: Coincident(g91,g92)
    c: Coincident(g92,g93)
    c: Coincident(g93,g94)
    c: Coincident(g94,g95)
    c: Coincident(g95,g96)
    c: Coincident(g96,g97)
    c: Coincident(g97,g98)
    c: Coincident(g98,g99)
    c: Coincident(g99,g100)
    c: Coincident(g100,g101)
    c: Coincident(g101,g102)
    c: Coincident(g102,g103)
    c: Coincident(g103,g104)
    c: Coincident(g104,g105)
    c: Coincident(g106,g107)
    c: Coincident(g107,g108)
    c: Coincident(g108,g109)
    c: Coincident(g109,g110)
    c: Coincident(g110,g106)
    c: Coincident(g111,g112)
    c: Coincident(g112,g113)
    c: Coincident(g113,g114)
    c: Coincident(g114,g115)
    c: Coincident(g115,g116)
    c: Coincident(g116,g117)
    c: Coincident(g117,g118)
    c: Coincident(g118,g119)
    c: Coincident(g119,g120)
    c: Coincident(g120,g121)
    c: Coincident(g121,g122)
    c: Coincident(g122,g123)
    c: Coincident(g123,g124)
    c: Coincident(g124,g125)
    c: Coincident(g125,g126)
    c: Coincident(g126,g127)
    c: Coincident(g127,g128)
    c: Coincident(g128,g129)
    c: Coincident(g129,g130)
    c: Coincident(g130,g131)
    c: Coincident(g131,g132)
    c: Coincident(g132,g133)
    c: Coincident(g133,g134)
    c: Coincident(g135,g136)
    c: Coincident(g136,g137)
    c: Coincident(g137,g138)
    c: Coincident(g138,g139)
    c: Coincident(g139,g135)
    c: Coincident(g140,g141)
    c: Coincident(g141,g142)
    c: Coincident(g142,g143)
    c: Coincident(g143,g144)
    c: Coincident(g144,g145)
    c: Coincident(g145,g146)
    c: Coincident(g146,g147)
    c: Coincident(g147,g140)
    c: Coincident(g148,g149)
    c: Coincident(g149,g150)
    c: Coincident(g150,g151)
    c: Coincident(g151,g148)
    c: Coincident(g152,g153)
    c: Coincident(g153,g154)
    c: Coincident(g154,g155)
    c: Coincident(g155,g156)
    c: Coincident(g156,g157)
    c: Coincident(g157,g158)
    c: Coincident(g158,g159)
    c: Coincident(g159,g160)
    c: Coincident(g160,g161)
    c: Coincident(g161,g162)
    c: Coincident(g162,g163)
    c: Coincident(g163,g164)
    c: Coincident(g165,g166)
    c: Coincident(g166,g167)
    c: Coincident(g167,g168)
    c: Coincident(g168,g169)
    c: Coincident(g169,g170)
    c: Coincident(g170,g171)
    c: Coincident(g171,g172)
    c: Coincident(g172,g173)
    c: Coincident(g173,g174)
    c: Coincident(g174,g175)
    c: Coincident(g175,g176)
    c: Coincident(g176,g165)
    c: Coincident(g177,g178)
    c: Coincident(g178,g179)
    c: Coincident(g179,g180)
    c: Coincident(g180,g181)
    c: Coincident(g181,g182)
    c: Coincident(g182,g183)
    c: Coincident(g183,g184)
    c: Coincident(g184,g185)
    c: Coincident(g185,g186)
    c: Coincident(g186,g187)
    c: Coincident(g187,g188)
    c: Coincident(g188,g189)
    c: Coincident(g189,g190)
    c: Coincident(g190,g191)
    c: Coincident(g191,g192)
    c: Coincident(g192,g177)
    c: Coincident(g193,g194)
    c: Coincident(g194,g195)
    c: Coincident(g195,g196)
    c: Coincident(g196,g193)
    c: Vertical(g193)
    c: Vertical(g195)
    c: Horizontal(g194)
    c: Horizontal(g196)
    c: DistanceY(g193,g193) = 22
    c: DistanceY(g193) = 5.5
    c: DistanceX(g196,g196) = 217
    c: DistanceX(g193) = -100
    c: Coincident(g44,g35)
    c: Coincident(g22,g8)
    c: Coincident(g164,g152)
    c: Coincident(g34,g23)
    c: Coincident(g48,g45)
    c: Coincident(g134,g111)
    c: Coincident(g90,g105)
FEATURE [Part::FeaturePython] Sketch_On_Surface  label="Sketch_On_Surface_FET"  # WARN: FeaturePython — macro-defined, semantics opaque (R4)
  ConstructionBounds = true
  FillExtrusion = true
  FillFaces = true
  Offset = -0.4
  ReverseU = false
  ReverseV = false
  Sketch = -> Sketch083
  SwapUV = false
  Thickness = 2
FEATURE [Part::Compound] Compound001  label="CompoundFET"
  Links = -> [path1944,path1651,path1652,path1653,path1654,path1655,path1656,path1657,path1658,path1659,path1660,path1661,path1662,path1663,path1664,path1665,path1938,path1942]
FEATURE [PartDesign::SubShapeBinder] Binder052
  BindCopyOnChange = 0
  BindMode = 0
  ClaimChildren = false
  Context = -> Body014 [Binder052.]
  Fuse = false
  MakeFace = true
  OffsetFill = false
  OffsetIntersection = false
  OffsetJoinType = 0
  OffsetOpenResult = false
  PartialLoad = false
  Relative = true
  Support = -> [Sketch_On_Surface]
  _Version = 2
FEATURE [Sketcher::SketchObject] Sketch084  label="SketchPatternXZ005"
  ArcFitTolerance = 1e-06
  AttachmentSupport = -> [XZ_Plane023]
  FullyConstrained = true
  MakeInternals = false
  MapMode = 5
  Placement = pos=(0,0,0) rot=(1,0,0;1.5708rad)
  sketch-geometry (10):
    g0: LineSegment StartX=95.8497 StartY=-2 StartZ=0 EndX=88.3441 EndY=11 EndZ=0
    g1: LineSegment StartX=89.6491 StartY=11 StartZ=0 EndX=97.1547 EndY=-2 EndZ=0
    g2: LineSegment StartX=66.6704 StartY=48.54 StartZ=0 EndX=74.176 EndY=35.54 EndZ=0
    g3: LineSegment StartX=74.176 StartY=35.54 StartZ=0 EndX=75.481 EndY=35.54 EndZ=0
    g4: LineSegment StartX=75.481 StartY=35.54 StartZ=0 EndX=67.9754 EndY=48.54 EndZ=0
    g5: LineSegment StartX=95.8497 StartY=-2 StartZ=0 EndX=97.1547 EndY=-2 EndZ=0
    g6: LineSegment [constr] StartX=0 StartY=0 StartZ=0 EndX=96 EndY=0 EndZ=0
    g7: LineSegment StartX=66.6704 StartY=48.54 StartZ=0 EndX=67.9754 EndY=48.54 EndZ=0
    g8: LineSegment StartX=88.3441 StartY=11 StartZ=0 EndX=89.6491 EndY=11.7534 EndZ=0
    g9: LineSegment StartX=89.6491 StartY=11.7534 StartZ=0 EndX=89.6491 EndY=11 EndZ=0
  constraints (29):
    c: Parallel(g0,g1)
    c: Angle(g0,g-1) = 1.0472
    c: DistanceY(g0) = 11
    c: Coincident(g3,g2)
    c: Coincident(g4,g3)
    c: Horizontal(g3)
    c: Tangent(g4,g1)
    c: Equal(g0,g2)
    c: Parallel(g2,g4)
    c: Coincident(g5,g0)
    c: Coincident(g1,g5)
    c: Horizontal(g5)
    c: DistanceX(g5,g5) = 1.305
    c: Coincident(g6,g-1)
    c: PointOnObject(g6,g-1)
    c: DistanceX(g6,g6) = 96
    c: DistanceY(g0,g6) = 2
    c: Coincident(g7,g2)
    c: Coincident(g7,g4)
    c: Horizontal(g7)
    c: DistanceY(g2) = 48.54
    c: PointOnObject(g6,g1)
    c: Coincident(g0,g8)
    c: Coincident(g8,g9)
    c: Coincident(g9,g1)
    c: Vertical(g9)
    c: Perpendicular(g0,g8)
    c: Horizontal(g1,g0)
    c: Equal(g3,g5)
FEATURE [PartDesign::Revolution] Revolution008
  Angle = 2.25
  Angle2 = 60
  Axis = (0,2e-16,1)
  Base = (0,0,0)
  BaseFeature = -> PolarPattern013
  Midplane = true
  Placement = pos=(0,0,0) rot=(1,0,0;1.5708rad)
  Profile = -> Sketch084
  ReferenceAxis = -> Sketch084 [V_Axis]
  Refine = true
  Reversed = true
  Suppressed = false
  Type = 0
FEATURE [PartDesign::PolarPattern] PolarPattern014
  Angle = 360
  Axis = -> Z_Axis023
  BaseFeature = -> Revolution008
  Mode = 0
  Occurrences = 16
  Offset = 60
  Originals = -> [Revolution008]
  Placement = pos=(0,0,0) rot=(1,0,0;1.5708rad)
  Refine = true
  Suppressed = false
  TransformMode = 0
FEATURE [Sketcher::SketchObject] Sketch085  label="SketchPatternXZ006"
  ArcFitTolerance = 1e-06
  AttachmentSupport = -> [XZ_Plane023]
  FullyConstrained = true
  MakeInternals = false
  MapMode = 5
  Placement = pos=(0,0,0) rot=(1,0,0;1.5708rad)
  sketch-geometry (11):
    g0: LineSegment StartX=95.8547 StartY=-2 StartZ=0 EndX=92.1019 EndY=4.5 EndZ=0
    g1: LineSegment [constr] StartX=92.1019 StartY=4.5 StartZ=0 EndX=93.4019 EndY=4.5 EndZ=0
    g2: LineSegment StartX=93.4019 StartY=4.5 StartZ=0 EndX=97.1547 EndY=-2 EndZ=0
    g3: LineSegment StartX=92.1019 StartY=4.5 StartZ=0 EndX=93.4019 EndY=5.25056 EndZ=0
    g4: LineSegment StartX=93.4019 StartY=5.25056 StartZ=0 EndX=93.4019 EndY=4.5 EndZ=0
    g5: LineSegment StartX=66.6754 StartY=48.54 StartZ=0 EndX=70.4282 EndY=42.04 EndZ=0
    g6: LineSegment StartX=70.4282 StartY=42.04 StartZ=0 EndX=71.7282 EndY=42.04 EndZ=0
    g7: LineSegment StartX=71.7282 StartY=42.04 StartZ=0 EndX=67.9754 EndY=48.54 EndZ=0
    g8: LineSegment StartX=95.8547 StartY=-2 StartZ=0 EndX=97.1547 EndY=-2 EndZ=0
    g9: LineSegment [constr] StartX=0 StartY=0 StartZ=0 EndX=96 EndY=0 EndZ=0
    g10: LineSegment StartX=66.6754 StartY=48.54 StartZ=0 EndX=67.9754 EndY=48.54 EndZ=0
  constraints (31):
    c: Coincident(g0,g1)
    c: Coincident(g1,g2)
    c: Parallel(g0,g2)
    c: Angle(g0,g-1) = 1.0472
    c: Horizontal(g1)
    c: DistanceY(g0) = 4.5
    c: Coincident(g4,g3)
    c: Coincident(g4,g1)
    c: Vertical(g4)
    c: Coincident(g6,g5)
    c: Coincident(g7,g6)
    c: Horizontal(g6)
    c: Tangent(g7,g2)
    c: Equal(g1,g6)
    c: Equal(g0,g5)
    c: Parallel(g5,g7)
    c: Coincident(g8,g0)
    c: Coincident(g2,g8)
    c: Horizontal(g8)
    c: DistanceX(g8,g8) = 1.3
    c: Coincident(g9,g-1)
    c: PointOnObject(g9,g-1)
    c: DistanceX(g9,g9) = 96
    c: DistanceY(g0,g9) = 2
    c: Coincident(g10,g5)
    c: Coincident(g10,g7)
    c: Horizontal(g10)
    c: DistanceY(g5) = 48.54
    c: PointOnObject(g9,g2)
    c: Coincident(g3,g0)
    c: Perpendicular(g0,g3)
FEATURE [PartDesign::Revolution] Revolution009
  Angle = 2.25
  Angle2 = 60
  Axis = (0,2e-16,1)
  Base = (0,0,0)
  BaseFeature = -> PolarPattern014
  Midplane = true
  Placement = pos=(0,0,0) rot=(1,0,0;1.5708rad)
  Profile = -> Sketch085
  ReferenceAxis = -> Sketch085 [V_Axis]
  Refine = true
  Reversed = true
  Suppressed = false
  Type = 0
FEATURE [PartDesign::PolarPattern] PolarPattern015
  Angle = 360
  Axis = -> Z_Axis023
  BaseFeature = -> Revolution009
  Mode = 0
  Occurrences = 80
  Offset = 6
  Originals = -> [Revolution009]
  Placement = pos=(0,0,0) rot=(1,0,0;1.5708rad)
  Refine = true
  Suppressed = false
  TransformMode = 0
FEATURE [PartDesign::Body] Body023  label="Pattern_cut_small"
  AllowCompound = false
  Group = -> [Revolution010,Sketch070,Revolution007,PolarPattern013,Revolution008,PolarPattern014,Revolution009,PolarPattern015,Sketch082,Sketch084,Sketch085]
  Origin = -> Origin023
  Placement = pos=(0,0,0) rot=(0,0,1;1.96349rad)
  Tip = -> PolarPattern015
FEATURE [Part::Cut] Cut004  label="Bezels"
  Base = -> Array002
  Refine = true
  Tool = -> Body023
FEATURE [PartDesign::SubShapeBinder] Binder053  label="BinderESPBottom"
  BindCopyOnChange = 0
  BindMode = 0
  ClaimChildren = false
  Context = -> Body014 [Binder053.]
  Fuse = false
  MakeFace = true
  OffsetFill = false
  OffsetIntersection = false
  OffsetJoinType = 0
  OffsetOpenResult = false
  PartialLoad = false
  Refine = true
  Relative = true
  Support = -> [Link005[Pad032.Face3]]
  _Version = 2
FEATURE [PartDesign::Pocket] Pocket012  label="PocketEspExtra"
  BaseFeature = -> Boolean018
  Direction = (-0.3,0,-1)
  Length = 10
  Length2 = 5
  Profile = -> Binder053
  Refine = true
  Suppressed = false
  TaperAngle = 14
  Type = 0
  UseCustomVector = true
FEATURE [PartDesign::Boolean] Boolean019  label="BooleanSkin"
  BaseFeature = -> Pocket012
  Group = -> [Binder051]
  Refine = true
  Suppressed = false
  Type = 1
  UsePlacement = true
FEATURE [Sketcher::SketchObject] Sketch086
  ArcFitTolerance = 1e-06
  AttachmentSupport = -> [XZ_Plane014]
  FullyConstrained = false
  MakeInternals = false
  MapMode = 5
  Placement = pos=(0,0,0) rot=(1,0,0;1.5708rad)
  sketch-geometry (5):
    g0: LineSegment StartX=-68.7883 StartY=35 StartZ=0 EndX=-73.869 EndY=35 EndZ=0
    g1: LineSegment StartX=-73.869 StartY=35 StartZ=0 EndX=-87.7254 EndY=11 EndZ=0
    g2: LineSegment StartX=-87.7254 StartY=11 StartZ=0 EndX=-85.185 EndY=6.6 EndZ=0
    g3: LineSegment StartX=-85.185 StartY=6.6 StartZ=0 EndX=-68.7883 EndY=35 EndZ=0
    g4: LineSegment [constr] StartX=-95 StartY=0 StartZ=0 EndX=-74.3753 EndY=35.7229 EndZ=0
  constraints (15):
    c: Coincident(g0,g1)
    c: Coincident(g1,g2)
    c: Coincident(g2,g3)
    c: Coincident(g3,g0)
    c: Angle(g-1,g3) = 1.0472
    c: Parallel(g1,g3)
    c: Angle(g1,g0) = 2.0944
    c: Angle(g2,g1) = 2.0944
    c: DistanceY(g1) = 11
    c: DistanceY(g0) = 35
    c: PointOnObject(g4,g-1)
    c: DistanceX(g4) = -95
    c: Angle(g4,g-1) = 2.0944
    c: Distance(g1,g4) = 0.8
    c: Distance(g3,g4) = 5.2
FEATURE [PartDesign::Groove] Groove001
  Angle = 32
  Angle2 = 60
  Axis = (0,2e-16,1)
  Base = (0,0,0)
  BaseFeature = -> Boolean019
  Midplane = true
  Profile = -> Sketch086
  ReferenceAxis = -> Sketch086 [V_Axis]
  Refine = true
  Reversed = true
  Suppressed = false
  Type = 0
FEATURE [PartDesign::Boolean] Boolean008  label="BooleanUSB001"
  BaseFeature = -> Groove001
  Group = -> [Binder027]
  Refine = true
  Suppressed = false
  Type = 1
  UsePlacement = true
FEATURE [App::Link] Link007
  LinkPlacement = pos=(-6.32584e-06,-82,-6.01) rot=(0,0,-1;1.5708rad)
  LinkedObject = -> <external feet2.FCStd>#Fusion
  Placement = pos=(-6.32584e-06,-82,-6.01) rot=(0,0,-1;1.5708rad)
FEATURE [Part::FeaturePython] Array003  label="base_feet"  # Draft array (typed FeaturePython)
  Angle = 360
  ArrayType = 1
  Axis = (0,0,1)
  Base = -> Link007
  Center = (0,0,0)
  Count = 3
  Fuse = true
  IntervalAxis = (0,0,0)
  IntervalX = (50,0,0)
  IntervalY = (0,50,0)
  IntervalZ = (0,0,50)
  NumberCircles = 3
  NumberPolar = 3
  NumberX = 2
  NumberY = 2
  NumberZ = 1
  RadialDistance = 50
  Symmetry = 1
  TangentialDistance = 25
FEATURE [PartDesign::SubShapeBinder] Binder054
  BindCopyOnChange = 0
  BindMode = 0
  ClaimChildren = false
  Context = -> Body010 [Binder054.]
  Fuse = false
  MakeFace = true
  OffsetFill = false
  OffsetIntersection = false
  OffsetJoinType = 0
  OffsetOpenResult = false
  PartialLoad = false
  Refine = true
  Relative = true
  Support = -> [Array003]
  _Version = 2
FEATURE [PartDesign::Chamfer] Chamfer  label="ChamferDisplays"
  Angle = 45
  Base = -> Boolean008 [Edge590,Edge564,Edge536,Edge502]
  BaseFeature = -> Boolean008
  ChamferType = 0
  FlipDirection = false
  Refine = true
  Size = 1.5
  Size2 = 1
  SupportTransform = false
  Suppressed = false
  UseAllEdges = false
FEATURE [PartDesign::Chamfer] Chamfer003  label="ChamferKnob"
  Angle = 45
  Base = -> Chamfer [Edge514]
  BaseFeature = -> Chamfer
  ChamferType = 0
  FlipDirection = false
  Refine = true
  Size = 1
  Size2 = 1
  SupportTransform = false
  Suppressed = false
  UseAllEdges = false
FEATURE [PartDesign::Boolean] Boolean020  label="BooleanFet"
  BaseFeature = -> Chamfer003
  Group = -> [Binder052]
  Refine = true
  Suppressed = false
  Type = 1
  UsePlacement = true
FEATURE [PartDesign::Body] Body014  label="Outer"
  AllowCompound = true
  BaseFeature = -> CompoundFilter
  Group = -> [BaseFeature001,Boolean009,Boolean012,Sketch079,Groove,Boolean017,Boolean018,Binder053,Pocket012,Boolean019,Sketch086,Groove001,Boolean008,Chamfer,Chamfer003,Boolean020]
  Origin = -> Origin014
  Tip = -> Boolean020
FEATURE [Sketcher::SketchObject] Sketch087
  ArcFitTolerance = 1e-06
  AttachmentSupport = -> [XY_Plane025]
  FullyConstrained = false
  MakeInternals = false
  MapMode = 5
  sketch-geometry (20):
    g0: LineSegment StartX=-22.5994 StartY=-35.3126 StartZ=0 EndX=-22.5994 EndY=-66.5973 EndZ=0
    g1: ArcOfCircle CenterX=-25.5994 CenterY=-66.5973 CenterZ=0 NormalX=0 NormalY=0 NormalZ=1 AngleXU=0 Radius=3 StartAngle=3.14159 EndAngle=6.28319
    g2: LineSegment StartX=-28.5994 StartY=-66.5973 StartZ=0 EndX=-28.5994 EndY=-35.3126 EndZ=0
    g3: LineSegment StartX=-28.5994 StartY=-35.3126 StartZ=0 EndX=-22.5994 EndY=-35.3126 EndZ=0
    g4: LineSegment StartX=83.7079 StartY=-28.7165 StartZ=0 EndX=65.1633 EndY=-21.5713 EndZ=0
    g5: ArcOfCircle CenterX=64.0847 CenterY=-24.3707 CenterZ=0 NormalX=0 NormalY=0 NormalZ=1 AngleXU=0 Radius=3 StartAngle=1.20303 EndAngle=4.34462
    g6: LineSegment StartX=63.0061 StartY=-27.1701 StartZ=0 EndX=81.5507 EndY=-34.3153 EndZ=0
    g7: LineSegment StartX=81.5507 StartY=-34.3153 StartZ=0 EndX=83.7079 EndY=-28.7165 EndZ=0
    g8: LineSegment StartX=-88.6952 StartY=3.43156 StartZ=0 EndX=-69.305 EndY=3.43156 EndZ=0
    g9: ArcOfCircle CenterX=-69.305 CenterY=0 CenterZ=0 NormalX=0 NormalY=0 NormalZ=1 AngleXU=0 Radius=3.43156 StartAngle=4.71239 EndAngle=7.85398
    g10: LineSegment StartX=-69.305 StartY=-3.43156 StartZ=0 EndX=-88.6952 EndY=-3.43156 EndZ=0
    g11: LineSegment StartX=-88.6952 StartY=-3.43156 StartZ=0 EndX=-88.6952 EndY=3.43156 EndZ=0
    g12: LineSegment StartX=22.5994 StartY=-35.3126 StartZ=0 EndX=22.5994 EndY=-66.5973 EndZ=0
    g13: ArcOfCircle CenterX=25.5994 CenterY=-66.5973 CenterZ=0 NormalX=0 NormalY=0 NormalZ=1 AngleXU=0 Radius=3 StartAngle=3.14159 EndAngle=6.28319
    g14: LineSegment StartX=28.5994 StartY=-66.5973 StartZ=0 EndX=28.5994 EndY=-35.3126 EndZ=0
    g15: LineSegment StartX=28.5994 StartY=-35.3126 StartZ=0 EndX=22.5994 EndY=-35.3126 EndZ=0
    g16: LineSegment StartX=83.7079 StartY=28.7165 StartZ=0 EndX=65.1633 EndY=21.5713 EndZ=0
    g17: ArcOfCircle CenterX=64.0847 CenterY=24.3707 CenterZ=0 NormalX=0 NormalY=0 NormalZ=1 AngleXU=0 Radius=3 StartAngle=1.93857 EndAngle=5.08016
    g18: LineSegment StartX=63.0061 StartY=27.1701 StartZ=0 EndX=81.5507 EndY=34.3153 EndZ=0
    g19: LineSegment StartX=81.5507 StartY=34.3153 StartZ=0 EndX=83.7079 EndY=28.7165 EndZ=0
  constraints (38):
    c: Vertical(g0)
    c: Tangent(g0,g1) = 1.5708
    c: Tangent(g1,g2) = 1.5708
    c: Coincident(g2,g3)
    c: Coincident(g3,g0)
    c: Horizontal(g3)
    c: Vertical(g2)
    c: Radius(g1) = 3
    c: Tangent(g4,g5) = -1.5708
    c: Tangent(g5,g6) = -1.5708
    c: Coincident(g6,g7)
    c: Coincident(g7,g4)
    c: Radius(g5) = 3
    c: Parallel(g4,g6)
    c: Perpendicular(g6,g7)
    c: Horizontal(g8)
    c: Tangent(g8,g9) = 1.5708
    c: Tangent(g9,g10) = 1.5708
    c: Coincident(g10,g11)
    c: Coincident(g11,g8)
    c: Vertical(g11)
    c: Parallel(g10,g8)
    c: PointOnObject(g9,g-1)
    c: Vertical(g12)
    c: Tangent(g12,g13) = -1.5708
    c: Tangent(g13,g14) = -1.5708
    c: Coincident(g14,g15)
    c: Coincident(g15,g12)
    c: Horizontal(g15)
    c: Vertical(g14)
    c: Radius(g13) = 3
    c: Tangent(g16,g17) = 1.5708
    c: Tangent(g17,g18) = 1.5708
    c: Coincident(g18,g19)
    c: Coincident(g19,g16)
    c: Radius(g17) = 3
    c: Parallel(g16,g18)
    c: Perpendicular(g18,g19)
FEATURE [PartDesign::Pad] Pad033
  Direction = (0,0,1)
  Length = 2
  Length2 = 10
  Profile = -> Sketch087
  ReferenceAxis = -> Sketch087 [N_Axis]
  Refine = true
  Suppressed = false
  Type = 0
FEATURE [PartDesign::Body] Body025  label="CableHolders"
  AllowCompound = true
  Group = -> [Sketch087,Pad033]
  Origin = -> Origin025
  Tip = -> Pad033
FEATURE [Part::MultiFuse] Fusion001  label="Upper"
  Refine = true
  Shapes = -> [Body014,Body012,Body025]
FEATURE [PartDesign::SubShapeBinder] Binder055
  BindCopyOnChange = 0
  BindMode = 0
  ClaimChildren = false
  Context = -> Body010 [Binder055.]
  Fuse = false
  MakeFace = true
  OffsetFill = false
  OffsetIntersection = false
  OffsetJoinType = 0
  OffsetOpenResult = false
  PartialLoad = false
  Placement = pos=(0,0,-0.6) rot=(0,1,0;3.14159rad)
  Refine = true
  Relative = true
  Support = -> [Body023]
  _Version = 2
FEATURE [PartDesign::SubShapeBinder] Binder056  label="BinderBoard"
  BindCopyOnChange = 0
  BindMode = 0
  ClaimChildren = false
  Context = -> Body010 [Binder056.]
  Fuse = false
  MakeFace = true
  OffsetFill = false
  OffsetIntersection = false
  OffsetJoinType = 1
  OffsetOpenResult = false
  PartialLoad = false
  Refine = true
  Relative = true
  Support = -> [Boolean010[Face305]]
  _Version = 2
FEATURE [Sketcher::SketchObject] Sketch088
  ArcFitTolerance = 1e-06
  AttachmentSupport = -> [YZ_Plane010]
  FullyConstrained = true
  MakeInternals = false
  MapMode = 5
  Placement = pos=(0,0,0) rot=(0.57735,0.57735,0.57735;2.0944rad)
  sketch-geometry (4):
    g0: LineSegment StartX=-92.1 StartY=3 StartZ=0 EndX=-92.1 EndY=-2 EndZ=0
    g1: LineSegment StartX=-92.1 StartY=-2 StartZ=0 EndX=-89.1 EndY=-2 EndZ=0
    g2: LineSegment StartX=-89.1 StartY=-2 StartZ=0 EndX=-89.1 EndY=3 EndZ=0
    g3: LineSegment StartX=-89.1 StartY=3 StartZ=0 EndX=-92.1 EndY=3 EndZ=0
  constraints (12):
    c: Coincident(g0,g1)
    c: Coincident(g1,g2)
    c: Coincident(g2,g3)
    c: Coincident(g3,g0)
    c: Vertical(g0)
    c: Vertical(g2)
    c: Horizontal(g1)
    c: Horizontal(g3)
    c: DistanceY(g1) = -2
    c: DistanceY(g2,g2) = 5
    c: DistanceX(g0) = -92.1
    c: DistanceX(g1,g1) = 3
FEATURE [PartDesign::Groove] Groove002
  Angle = 2
  Angle2 = 60
  Axis = (0,0,1)
  Base = (0,0,0)
  BaseFeature = -> Revolution001
  Midplane = true
  Placement = pos=(0,0,0) rot=(1,1,1;2.0944rad)
  Profile = -> Sketch088
  ReferenceAxis = -> Sketch088 [V_Axis]
  Refine = true
  Reversed = true
  Suppressed = false
  Type = 0
FEATURE [PartDesign::PolarPattern] PolarPattern016
  Angle = 360
  Axis = -> Z_Axis010
  BaseFeature = -> Groove002
  Mode = 0
  Occurrences = 36
  Offset = 120
  Originals = -> [Groove002]
  Placement = pos=(0,0,0) rot=(1,1,1;2.0944rad)
  Refine = true
  Suppressed = false
  TransformMode = 0
FEATURE [PartDesign::Pad] Pad030  label="PadUSB"
  BaseFeature = -> PolarPattern016
  Direction = (0,0.32,1)
  Length = 5
  Length2 = 10
  Placement = pos=(0,0,0) rot=(1,1,1;2.0944rad)
  Profile = -> Sketch073
  ReferenceAxis = -> Sketch073 [N_Axis]
  Refine = true
  Reversed = true
  Suppressed = false
  Type = 0
  UseCustomVector = true
FEATURE [PartDesign::Boolean] Boolean  label="BooleanUSB002"
  BaseFeature = -> Pad030
  Group = -> [Binder]
  Refine = true
  Suppressed = false
  Type = 1
  UsePlacement = true
FEATURE [PartDesign::Pocket] Pocket001  label="PocketUSB"
  BaseFeature = -> Boolean
  Direction = (0,0,-1)
  Length = 10
  Length2 = 5
  Profile = -> Sketch021
  ReferenceAxis = -> Sketch021 [N_Axis]
  Refine = true
  Suppressed = false
  Type = 4
FEATURE [PartDesign::Pocket] Pocket013  label="PocketUSB2"
  BaseFeature = -> Pocket001
  Direction = (0,0,-1)
  Length = 5
  Length2 = 5
  Profile = -> Sketch074
  ReferenceAxis = -> Sketch074 [N_Axis]
  Refine = true
  Reversed = true
  Suppressed = false
  Type = 0
FEATURE [PartDesign::Boolean] Boolean001  label="BooleanAkku001"
  BaseFeature = -> Pocket013
  Group = -> [Binder015]
  Refine = true
  Suppressed = false
  Type = 1
  UsePlacement = true
FEATURE [PartDesign::Pad] Pad031
  BaseFeature = -> Boolean001
  Direction = (0,0,1)
  Length = 5
  Length2 = 10
  Profile = -> Binder045
  Refine = true
  Reversed = true
  Suppressed = false
  Type = 0
FEATURE [PartDesign::Pocket] Pocket004  label="PocketInner"
  BaseFeature = -> Pad031
  Direction = (0,0,-1)
  Length = 9
  Length2 = 5
  Profile = -> Sketch037
  ReferenceAxis = -> Sketch037 [N_Axis]
  Refine = true
  Suppressed = false
  TaperAngle = 20
  Type = 0
FEATURE [PartDesign::AdditivePipe] AdditivePipe
  AuxilleryCurvelinear = true
  AuxillerySpineTangent = false
  BaseFeature = -> Pocket004
  Binormal = (0,0,0)
  Mode = 0
  Profile = -> Sketch040
  Refine = true
  Spine = -> Sketch037
  SpineTangent = false
  Suppressed = false
  Transformation = 0
  Transition = 0
FEATURE [PartDesign::Boolean] Boolean010  label="BooleanEsp"
  BaseFeature = -> AdditivePipe
  Group = -> [Binder029]
  Refine = true
  Suppressed = false
  Type = 1
  UsePlacement = true
FEATURE [PartDesign::Pocket] Pocket015  label="PocketESPBoard"
  BaseFeature = -> Boolean010
  Direction = (-1.68587e-07,-1.04308e-07,-1)
  Length = 14
  Length2 = 5
  Profile = -> Binder056
  Refine = true
  Reversed = true
  Suppressed = false
  TaperAngle = 20
  Type = 0
FEATURE [PartDesign::Pocket] Pocket014  label="PocketESPUSB"
  BaseFeature = -> Pocket015
  Direction = (1.68587e-07,1.04308e-07,1)
  Length = 7
  Length2 = 5
  Profile = -> Binder047
  Refine = true
  Suppressed = false
  TaperAngle = 19
  Type = 4
FEATURE [PartDesign::Pocket] Pocket005  label="PocketCables"
  BaseFeature = -> Pocket014
  Direction = (0,0,-1)
  Length = 4
  Length2 = 5
  Profile = -> Sketch038
  ReferenceAxis = -> Sketch038 [N_Axis]
  Refine = true
  Suppressed = false
  TaperAngle = -45
  Type = 0
FEATURE [PartDesign::Pad] Pad032
  BaseFeature = -> Pocket005
  Direction = (0,0,1)
  Length = 8.4
  Length2 = 10
  Profile = -> Binder046
  Refine = true
  Suppressed = false
  Type = 0
FEATURE [PartDesign::Hole] Hole
  BaseFeature = -> Pad032
  CustomThreadClearance = 0
  Depth = 25
  DepthType = 0
  Diameter = 4.5
  DrillForDepth = false
  DrillPoint = 1
  DrillPointAngle = 118
  HoleCutCountersinkAngle = 90
  HoleCutCustomValues = false
  HoleCutDepth = 4.4
  HoleCutDiameter = 8
  HoleCutType = 1
  ModelThread = false
  Profile = -> Sketch054
  Refine = true
  Suppressed = false
  Tapered = false
  TaperedAngle = 90
  ThreadClass = 0
  ThreadDepth = 25
  ThreadDepthType = 0
  ThreadDirection = 0
  ThreadFit = 0
  ThreadSize = 11
  ThreadType = 1
  Threaded = false
  UseCustomThreadClearance = false
FEATURE [PartDesign::Pocket] Pocket018
  BaseFeature = -> Hole
  Direction = (0,0,-1)
  Length = 3.5
  Length2 = 5
  Profile = -> Sketch081
  ReferenceAxis = -> Sketch081 [N_Axis]
  Refine = true
  Reversed = true
  Suppressed = true
  Type = 0
FEATURE [PartDesign::Boolean] Boolean021  label="BooleanFeet"
  BaseFeature = -> Pocket018
  Group = -> [Binder054]
  Refine = true
  Suppressed = false
  Type = 1
  UsePlacement = true
FEATURE [PartDesign::Boolean] Boolean022  label="BooleanPattern"
  BaseFeature = -> Boolean021
  Group = -> [Binder055]
  Refine = true
  Suppressed = false
  Type = 1
  UsePlacement = true
FEATURE [PartDesign::Body] Body010  label="Bottom"
  AllowCompound = true
  Group = -> [Sketch015,Revolution001,Sketch021,Sketch073,Sketch088,Groove002,PolarPattern016,Pad030,Boolean,Pocket001,Sketch074,Pocket013,Boolean001,Sketch037,Pad031,Pocket004,Binder045,AdditivePipe,Boolean010,Sketch038,Binder047,Binder056,Pocket015,Pocket014,Binder049,Pocket005,Sketch040,Sketch054,Binder046,Pad032,Hole,Sketch081,Pocket018,Boolean021,Boolean022]
  Origin = -> Origin010
  Tip = -> Boolean022
FEATURE [Mesh::Feature] Mesh012  label="Displaybrackets (Meshed)"
FEATURE [Mesh::Feature] Mesh013  label="Bottom (Meshed)"
FEATURE [Mesh::Feature] Mesh014  label="Bezels (Meshed)"
FEATURE [Sketcher::SketchObject] Sketch089
  ArcFitTolerance = 1e-06
  AttachmentSupport = -> [XZ_Plane017]
  FullyConstrained = true
  MakeInternals = false
  MapMode = 5
  Placement = pos=(0,0,0) rot=(1,0,0;1.5708rad)
  sketch-geometry (11):
    g0: LineSegment StartX=0 StartY=34 StartZ=0 EndX=36 EndY=34 EndZ=0
    g1: LineSegment StartX=36 StartY=34 StartZ=0 EndX=36 EndY=41.4 EndZ=0
    g2: LineSegment StartX=43.2 StartY=41.4 StartZ=0 EndX=43.2 EndY=34 EndZ=0
    g3: LineSegment StartX=43.2 StartY=34 StartZ=0 EndX=44.2 EndY=34 EndZ=0
    g4: LineSegment StartX=48 StartY=45 StartZ=0 EndX=44 EndY=45 EndZ=0
    g5: LineSegment StartX=44 StartY=45 StartZ=0 EndX=43.2 EndY=42 EndZ=0
    g6: LineSegment StartX=43.2 StartY=42 StartZ=0 EndX=0 EndY=42 EndZ=0
    g7: LineSegment StartX=0 StartY=42 StartZ=0 EndX=0 EndY=34 EndZ=0
    g8: LineSegment StartX=36 StartY=41.4 StartZ=0 EndX=43.2 EndY=41.4 EndZ=0
    g9: LineSegment StartX=44.2 StartY=34 StartZ=0 EndX=48 EndY=41.4 EndZ=0
    g10: LineSegment StartX=48 StartY=41.4 StartZ=0 EndX=48 EndY=45 EndZ=0
  constraints (33):
    c: Horizontal(g0)
    c: Coincident(g0,g1)
    c: Vertical(g1)
    c: Vertical(g2)
    c: Coincident(g2,g3)
    c: Horizontal(g3)
    c: Coincident(g4,g5)
    c: Coincident(g5,g6)
    c: PointOnObject(g6,g-2)
    c: Horizontal(g6)
    c: Coincident(g6,g7)
    c: Vertical(g7)
    c: DistanceX(g0) = 36
    c: DistanceX(g2) = 43.2
    c: DistanceY(g4) = 45
    c: Horizontal(g4)
    c: DistanceY(g5,g5) = 3
    c: Horizontal(g2,g0)
    c: Horizontal(g2,g1)
    c: Coincident(g8,g1)
    c: Coincident(g8,g2)
    c: DistanceX(g4,g4) = 4
    c: DistanceY(g2,g5) = 0.6
    c: Coincident(g0,g7)
    c: DistanceX(g4) = 48
    c: DistanceX(g3,g3) = 1
    c: Vertical(g5,g2)
    c: DistanceY(g2,g5) = 8
    c: Coincident(g3,g9)
    c: Coincident(g9,g10)
    c: Coincident(g10,g4)
    c: Vertical(g10)
    c: Horizontal(g9,g2)
FEATURE [PartDesign::Revolution] Revolution011
  Angle = 360
  Angle2 = 60
  Axis = (0,2e-16,1)
  Base = (0,0,0)
  Placement = pos=(0,0,0) rot=(1,0,0;1.5708rad)
  Profile = -> Sketch089
  ReferenceAxis = -> Sketch089 [V_Axis]
  Refine = true
  Reversed = true
  Suppressed = false
  Type = 0
FEATURE [Sketcher::SketchObject] Sketch055
  ArcFitTolerance = 1e-06
  AttachmentSupport = -> [Revolution011]
  FullyConstrained = true
  MakeInternals = false
  MapMode = 5
  Placement = pos=(0,1.85e-14,42) rot=(0,0,1;3.14159rad)
  sketch-geometry (2):
    g0: Circle CenterX=5 CenterY=0 CenterZ=0 NormalX=0 NormalY=0 NormalZ=1 AngleXU=0 Radius=2.25
    g1: Circle CenterX=-5 CenterY=0 CenterZ=0 NormalX=0 NormalY=0 NormalZ=1 AngleXU=0 Radius=2.25
  constraints (6):
    c: PointOnObject(g0,g-1)
    c: PointOnObject(g1,g-1)
    c: Equal(g1,g0)
    c: Diameter(g1) = 4.5
    c: DistanceX(g0) = 5
    c: DistanceX(g1) = -5
FEATURE [Sketcher::SketchObject] Sketch091
  ArcFitTolerance = 1e-06
  AttachmentOffset = pos=(0,0,42) rot=(0,0,1;0.1309rad)
  AttachmentSupport = -> [XY_Plane017]
  FullyConstrained = true
  MakeInternals = false
  MapMode = 5
  Placement = pos=(0,0,42) rot=(0,0,1;0.1309rad)
  sketch-geometry (4):
    g0: LineSegment StartX=0 StartY=0.8 StartZ=0 EndX=0 EndY=-0.8 EndZ=0
    g1: LineSegment StartX=0 StartY=-0.8 StartZ=0 EndX=44.5 EndY=-0.8 EndZ=0
    g2: LineSegment StartX=44.5 StartY=-0.8 StartZ=0 EndX=44.5 EndY=0.8 EndZ=0
    g3: LineSegment StartX=44.5 StartY=0.8 StartZ=0 EndX=0 EndY=0.8 EndZ=0
  constraints (11):
    c: Coincident(g0,g1)
    c: Coincident(g1,g2)
    c: Coincident(g2,g3)
    c: Coincident(g3,g0)
    c: Vertical(g0)
    c: Horizontal(g1)
    c: Horizontal(g3)
    c: PointOnObject(g0,g-2)
    c: DistanceX(g2) = 44.5
    c: DistanceY(g2,g2) = 1.6
    c: Symmetric(g1,g2,g-1)
FEATURE [PartDesign::Pad] Pad034
  BaseFeature = -> Revolution011
  Direction = (0,0,1)
  Length = 6
  Length2 = 10
  Placement = pos=(0,0,0) rot=(1,0,0;1.5708rad)
  Profile = -> Sketch091
  ReferenceAxis = -> Sketch091 [N_Axis]
  Refine = true
  Reversed = true
  Suppressed = false
  Type = 0
FEATURE [PartDesign::PolarPattern] PolarPattern017
  Angle = 360
  Axis = -> Sketch091 [N_Axis]
  BaseFeature = -> Pad034
  Mode = 0
  Occurrences = 24
  Offset = 120
  Originals = -> [Pad034]
  Placement = pos=(0,0,0) rot=(1,0,0;1.5708rad)
  Refine = true
  Suppressed = false
  TransformMode = 0
FEATURE [PartDesign::Hole] Hole001
  BaseFeature = -> PolarPattern017
  CustomThreadClearance = 0
  Depth = 25
  DepthType = 0
  Diameter = 4.5
  DrillForDepth = false
  DrillPoint = 1
  DrillPointAngle = 118
  HoleCutCountersinkAngle = 90
  HoleCutCustomValues = false
  HoleCutDepth = 4.4
  HoleCutDiameter = 7
  HoleCutType = 1
  ModelThread = false
  Placement = pos=(0,0,0) rot=(1,0,0;1.5708rad)
  Profile = -> Sketch055
  Refine = true
  Suppressed = false
  Tapered = false
  TaperedAngle = 90
  ThreadClass = 0
  ThreadDepth = 25
  ThreadDepthType = 0
  ThreadDirection = 0
  ThreadFit = 0
  ThreadSize = 11
  ThreadType = 1
  Threaded = false
  UseCustomThreadClearance = false
FEATURE [PartDesign::Body] Body017  label="Top"
  AllowCompound = false
  Group = -> [Revolution011,Sketch055,Sketch089,Sketch091,Pad034,PolarPattern017,Hole001]
  Origin = -> Origin017
  Tip = -> Hole001
FEATURE [Part::Compound] Compound  label="Scale_Compound"
  Links = -> [Body015,Body010,Body011,Body017,Body018,Cut004,Fusion001]
FEATURE [Mesh::Feature] Mesh018  label="Top (Meshed)"
FEATURE [Mesh::Feature] Mesh020  label="Button (Meshed)"
FEATURE [Part::Compound] Compound002  label="Parts_Compound"
  Links = -> [Link,Link004,Link005,Link006,Link002,Link003]
FEATURE [Part::Compound] Compound004  label="Base_Compound"
  Links = -> [Compound001,Sketch_On_Surface,Array003,Cut002,CompoundFilter,Slice_child6,Body013,Body019]
FEATURE [Mesh::Feature] Mesh  label="Distance (Meshed)"
FEATURE [Mesh::Feature] Mesh021  label="Upper (Meshed)"
FEATURE [Mesh::Feature] Mesh022  label="Upper-FET(Meshed)"
FEATURE [Part::Compound] Compound005  label="Compound_Meshed"
  Links = -> [Mesh022,Mesh013,Mesh020,Mesh018,Mesh012,Mesh014,Mesh,Mesh021]

RESOLVED EXTERNAL PARTS (link-assembly join: the EXTERNAL_REF files above that resolve inside this repo's crawl, each included once):
---- part feet2.FCStd = doc fcstd_0775f06ce156 ----
FCSTD DOCUMENT  (FreeCAD 1.0R38641 +1 (Git))
Label: feet2
License: All rights reserved
LicenseURL: https://en.wikipedia.org/wiki/All_rights_reserved
objects: Sketcher::SketchObject×13, PartDesign::Pad×8, PartDesign::Pocket×6, PartDesign::Body×5, Part::Mirroring×3, Part::MultiFuse×3, PartDesign::PolarPattern×2, Part::Cut×2, Part::Box×1, PartDesign::FeatureBase×1, PartDesign::SubShapeBinder×1, Part::Compound×1, Mesh::Feature×1
note: 90 computed .brp shape members not serialized (recipe doc carries the construction recipe); baked Part::Feature solids carry a one-line shape summary decoded from their .brp

FEATURE [Sketcher::SketchObject] Sketch003
  ArcFitTolerance = 1e-06
  AttachmentSupport = -> [XZ_Plane001]
  FullyConstrained = true
  MakeInternals = false
  MapMode = 5
  Placement = pos=(0,0,0) rot=(1,0,0;1.5708rad)
  sketch-geometry (13):
    g0: LineSegment StartX=-20 StartY=-1.5 StartZ=0 EndX=-18.2679 EndY=1.5 EndZ=0
    g1: LineSegment StartX=-18.2679 StartY=1.5 StartZ=0 EndX=0 EndY=1.5 EndZ=0
    g2: LineSegment StartX=-2e-16 StartY=-1.5 StartZ=0 EndX=-12 EndY=-1.5 EndZ=0
    g3: LineSegment StartX=-2e-16 StartY=-1.5 StartZ=0 EndX=0.75 EndY=-1.5 EndZ=0
    g4: LineSegment StartX=1.5 StartY=-0.75 StartZ=0 EndX=1.5 EndY=0 EndZ=0
    g5: ArcOfCircle CenterX=0 CenterY=0 CenterZ=0 NormalX=0 NormalY=0 NormalZ=1 AngleXU=0 Radius=1.5 StartAngle=0 EndAngle=1.5708
    g6: ArcOfCircle [constr] CenterX=0.75 CenterY=-0.75 CenterZ=0 NormalX=0 NormalY=0 NormalZ=1 AngleXU=0 Radius=0.75 StartAngle=4.71239 EndAngle=6.28319
    g7: GeomPoint [constr] X=1.5 Y=-1.5 Z=0
    g8: LineSegment StartX=0.75 StartY=-1.5 StartZ=0 EndX=1.5 EndY=-0.75 EndZ=0
    g9: LineSegment StartX=-16 StartY=-1.5 StartZ=0 EndX=-15 EndY=-0.5 EndZ=0
    g10: LineSegment StartX=-15 StartY=-0.5 StartZ=0 EndX=-13 EndY=-0.5 EndZ=0
    g11: LineSegment StartX=-13 StartY=-0.5 StartZ=0 EndX=-12 EndY=-1.5 EndZ=0
    g12: LineSegment StartX=-16 StartY=-1.5 StartZ=0 EndX=-20 EndY=-1.5 EndZ=0
  constraints (35):
    c: Coincident(g0,g1)
    c: Horizontal(g1)
    c: Coincident(g12,g0)
    c: Horizontal(g2)
    c: Symmetric(g2,g1,g-1)
    c: DistanceX(g12,g2) = 20
    c: DistanceY(g2,g1) = 3
    c: Angle(g2,g0) = 1.0472
    c: Coincident(g2,g3)
    c: Horizontal(g3)
    c: PointOnObject(g4,g-1)
    c: Vertical(g4)
    c: Coincident(g5,g-1)
    c: Coincident(g5,g4)
    c: Tangent(g5,g1) = 1.5708
    c: PointOnObject(g7,g3)
    c: PointOnObject(g7,g4)
    c: Tangent(g3,g6) = -1.5708
    c: Tangent(g4,g6) = -1.5708
    c: Coincident(g8,g3)
    c: Coincident(g8,g4)
    c: DistanceX(g3,g3) = 0.75
    c: PointOnObject(g9,g12)
    c: Coincident(g9,g10)
    c: Horizontal(g10)
    c: Coincident(g10,g11)
    c: DistanceY(g11,g10) = 1
    c: DistanceX(g10,g10) = 2
    c: Angle(g11,g2) = 0.785398
    c: Angle(g9,g2) = 2.35619
    c: DistanceX(g0,g9) = 4
    c: Coincident(g2,g11)
    c: PointOnObject(g12,g9)
    c: Horizontal(g12)
    c: Horizontal(g9,g2)
FEATURE [PartDesign::Pad] Pad001
  Direction = (0,-1,2e-16)
  Length = 5
  Length2 = 10
  Placement = pos=(0,0,0) rot=(1,0,0;1.5708rad)
  Profile = -> Sketch003
  ReferenceAxis = -> Sketch003 [N_Axis]
  Refine = true
  Suppressed = false
  Type = 0
FEATURE [Sketcher::SketchObject] Sketch004
  ArcFitTolerance = 1e-06
  AttachmentOffset = pos=(0,0,5) rot=(0,0,1;0rad)
  AttachmentSupport = -> [XZ_Plane001]
  FullyConstrained = true
  MakeInternals = false
  MapMode = 5
  Placement = pos=(0,-5,1.1e-15) rot=(1,0,0;1.5708rad)
  sketch-geometry (4):
    g0: ArcOfCircle CenterX=0 CenterY=0 CenterZ=0 NormalX=0 NormalY=0 NormalZ=1 AngleXU=0 Radius=1 StartAngle=4.71239 EndAngle=7.85398
    g1: ArcOfCircle CenterX=-5 CenterY=-2e-16 CenterZ=0 NormalX=0 NormalY=0 NormalZ=1 AngleXU=0 Radius=1 StartAngle=1.5708 EndAngle=4.71239
    g2: LineSegment StartX=-2e-16 StartY=-1 StartZ=0 EndX=-5 EndY=-1 EndZ=0
    g3: LineSegment StartX=3e-16 StartY=1 StartZ=0 EndX=-5 EndY=1 EndZ=0
  constraints (9):
    c: Tangent(g0,g2) = 1.5708
    c: Tangent(g0,g3) = -1.5708
    c: Tangent(g1,g2) = 1.5708
    c: Tangent(g1,g3) = -1.5708
    c: Equal(g0,g1)
    c: Horizontal(g3)
    c: Radius(g0) = 1
    c: Coincident(g0,g-1)
    c: DistanceX(g1,g0) = 5
FEATURE [PartDesign::Pocket] Pocket001
  BaseFeature = -> Pad001
  Direction = (0,1,-2e-16)
  Length = 1.5
  Length2 = 5
  Placement = pos=(0,0,0) rot=(1,0,0;1.5708rad)
  Profile = -> Sketch004
  ReferenceAxis = -> Sketch004 [N_Axis]
  Refine = true
  Suppressed = false
  TaperAngle = -30
  Type = 0
FEATURE [PartDesign::Body] Body001  label="A001"
  AllowCompound = false
  Group = -> [Sketch003,Pad001,Sketch004,Pocket001]
  Origin = -> Origin001
  Tip = -> Pocket001
FEATURE [Sketcher::SketchObject] Sketch005
  ArcFitTolerance = 1e-06
  AttachmentSupport = -> [XZ_Plane002]
  FullyConstrained = true
  MakeInternals = false
  MapMode = 5
  Placement = pos=(0,0,0) rot=(1,0,0;1.5708rad)
  sketch-geometry (14):
    g0: LineSegment StartX=-20.2 StartY=-1.5 StartZ=0 EndX=-18.3525 EndY=1.7 EndZ=0
    g1: LineSegment StartX=-18.3525 StartY=1.7 StartZ=0 EndX=-2.5815 EndY=1.7 EndZ=0
    g2: LineSegment StartX=-2.5815 StartY=1.7 StartZ=0 EndX=-3.85167 EndY=3.9 EndZ=0
    g3: LineSegment StartX=-3.85167 StartY=3.9 StartZ=0 EndX=-0.651666 EndY=3.9 EndZ=0
    g4: LineSegment StartX=-0.651666 StartY=3.9 StartZ=0 EndX=0.618505 EndY=1.7 EndZ=0
    g5: LineSegment StartX=0.618505 StartY=1.7 StartZ=0 EndX=5.5 EndY=1.7 EndZ=0
    g6: LineSegment StartX=5.5 StartY=1.7 StartZ=0 EndX=5.5 EndY=-1.5 EndZ=0
    g7: LineSegment StartX=5.5 StartY=-1.5 StartZ=0 EndX=8 EndY=-1.5 EndZ=0
    g8: LineSegment StartX=8 StartY=-1.5 StartZ=0 EndX=8 EndY=4.5 EndZ=0
    g9: LineSegment StartX=8 StartY=4.5 StartZ=0 EndX=-22 EndY=4.5 EndZ=0
    g10: LineSegment [constr] StartX=0 StartY=0 StartZ=0 EndX=-2.25167 EndY=3.9 EndZ=0
    g11: Circle [constr] CenterX=0 CenterY=0 CenterZ=0 NormalX=0 NormalY=0 NormalZ=1 AngleXU=0 Radius=1.80902
    g12: LineSegment StartX=-20.2 StartY=-1.5 StartZ=0 EndX=-22 EndY=-1.5 EndZ=0
    g13: LineSegment StartX=-22 StartY=-1.5 StartZ=0 EndX=-22 EndY=4.5 EndZ=0
  constraints (40):
    c: Coincident(g0,g1)
    c: Horizontal(g1)
    c: Coincident(g1,g2)
    c: Coincident(g2,g3)
    c: Horizontal(g3)
    c: Coincident(g3,g4)
    c: Coincident(g4,g5)
    c: Horizontal(g5)
    c: Coincident(g5,g6)
    c: Vertical(g6)
    c: Coincident(g6,g7)
    c: Horizontal(g7)
    c: Coincident(g7,g8)
    c: Vertical(g8)
    c: Coincident(g8,g9)
    c: Horizontal(g9)
    c: Parallel(g2,g4)
    c: Angle(g2,g1) = 1.0472
    c: DistanceX(g1,g4) = 3.2
    c: Horizontal(g4,g1)
    c: Horizontal(g6,g0)
    c: Angle(g0,g-1) = 2.0944
    c: DistanceY(g6) = -1.5
    c: DistanceY(g6,g6) = 3.2
    c: DistanceY(g8,g8) = 6
    c: Coincident(g10,g-1)
    c: Symmetric(g3,g3,g10)
    c: Parallel(g10,g4)
    c: DistanceX(g0) = -20.2
    c: Coincident(g11,g10)
    c: PointOnObject(g4,g11)
    c: DistanceY(g3,g8) = 0.6
    c: DistanceX(g5) = 5.5
    c: Coincident(g0,g12)
    c: Horizontal(g12)
    c: Coincident(g12,g13)
    c: Coincident(g13,g9)
    c: Vertical(g13)
    c: DistanceX(g9,g9) = 30
    c: DistanceX(g12) = -22
FEATURE [PartDesign::Pad] Pad002
  Direction = (0,-1,2e-16)
  Length = 5.2
  Length2 = 10
  Placement = pos=(0,0,0) rot=(1,0,0;1.5708rad)
  Profile = -> Sketch005
  ReferenceAxis = -> Sketch005 [N_Axis]
  Refine = true
  Suppressed = false
  Type = 0
FEATURE [Sketcher::SketchObject] Sketch006
  ArcFitTolerance = 1e-06
  AttachmentOffset = pos=(0,0,5.2) rot=(0,0,1;0rad)
  AttachmentSupport = -> [XZ_Plane002]
  FullyConstrained = true
  MakeInternals = false
  MapMode = 5
  Placement = pos=(0,-5.2,1.2e-15) rot=(1,0,0;1.5708rad)
  sketch-geometry (1):
    g0: Circle CenterX=0 CenterY=0 CenterZ=0 NormalX=0 NormalY=0 NormalZ=1 AngleXU=0 Radius=1.05
  constraints (2):
    c: Diameter(g0) = 2.1
    c: Coincident(g0,g-1)
FEATURE [PartDesign::Pad] Pad003
  BaseFeature = -> Pad002
  Direction = (0,-1,2e-16)
  Length = 1.6
  Length2 = 10
  Placement = pos=(0,0,0) rot=(1,0,0;1.5708rad)
  Profile = -> Sketch006
  ReferenceAxis = -> Sketch006 [N_Axis]
  Refine = true
  Reversed = true
  Suppressed = false
  TaperAngle = -30
  Type = 0
FEATURE [Sketcher::SketchObject] Sketch007
  ArcFitTolerance = 1e-06
  AttachmentOffset = pos=(0,0,5.2) rot=(0,0,1;0rad)
  AttachmentSupport = -> [XZ_Plane002]
  FullyConstrained = true
  MakeInternals = false
  MapMode = 5
  Placement = pos=(0,-5.2,1.2e-15) rot=(1,0,0;1.5708rad)
  sketch-geometry (4):
    g0: LineSegment StartX=-22 StartY=4.5 StartZ=0 EndX=-22 EndY=-1.5 EndZ=0
    g1: LineSegment StartX=-22 StartY=-1.5 StartZ=0 EndX=8 EndY=-1.5 EndZ=0
    g2: LineSegment StartX=8 StartY=-1.5 StartZ=0 EndX=8 EndY=4.5 EndZ=0
    g3: LineSegment StartX=8 StartY=4.5 StartZ=0 EndX=-22 EndY=4.5 EndZ=0
  constraints (12):
    c: Coincident(g0,g1)
    c: Coincident(g1,g2)
    c: Coincident(g2,g3)
    c: Coincident(g3,g0)
    c: Vertical(g0)
    c: Vertical(g2)
    c: Horizontal(g1)
    c: Horizontal(g3)
    c: DistanceX(g3,g3) = 30
    c: DistanceY(g0,g0) = 6
    c: DistanceX(g0) = -22
    c: DistanceY(g1) = -1.5
FEATURE [PartDesign::Pad] Pad004
  BaseFeature = -> Pad003
  Direction = (0,-1,2e-16)
  Length = 4.8
  Length2 = 10
  Placement = pos=(0,0,0) rot=(1,0,0;1.5708rad)
  Profile = -> Sketch007
  ReferenceAxis = -> Sketch007 [N_Axis]
  Refine = true
  Suppressed = false
  Type = 0
FEATURE [PartDesign::Body] Body002  label="A002"
  AllowCompound = true
  Group = -> [Sketch005,Pad002,Sketch006,Pad003,Sketch007,Pad004]
  Origin = -> Origin002
  Tip = -> Pad004
FEATURE [Sketcher::SketchObject] Sketch008
  ArcFitTolerance = 1e-06
  AttachmentSupport = -> [XZ_Plane003]
  FullyConstrained = true
  MakeInternals = false
  MapMode = 5
  Placement = pos=(0,0,0) rot=(1,0,0;1.5708rad)
  sketch-geometry (4):
    g0: LineSegment StartX=-20 StartY=-2.5 StartZ=0 EndX=-17.1132 EndY=2.5 EndZ=0
    g1: LineSegment StartX=-17.1132 StartY=2.5 StartZ=0 EndX=0 EndY=2.5 EndZ=0
    g2: LineSegment StartX=-5e-16 StartY=-2.5 StartZ=0 EndX=-20 EndY=-2.5 EndZ=0
    g3: ArcOfCircle CenterX=0 CenterY=0 CenterZ=0 NormalX=0 NormalY=0 NormalZ=1 AngleXU=0 Radius=2.5 StartAngle=4.71239 EndAngle=7.85398
  constraints (11):
    c: Coincident(g0,g1)
    c: Horizontal(g1)
    c: Horizontal(g2)
    c: DistanceX(g0,g2) = 20
    c: Angle(g2,g0) = 1.0472
    c: PointOnObject(g2,g-2)
    c: Coincident(g2,g0)
    c: Coincident(g3,g-1)
    c: Tangent(g3,g1) = 1.5708
    c: Coincident(g3,g2)
    c: Radius(g3) = 2.5
FEATURE [PartDesign::Pad] Pad005
  Direction = (0,-1,2e-16)
  Length = 5
  Length2 = 10
  Placement = pos=(0,0,0) rot=(1,0,0;1.5708rad)
  Profile = -> Sketch008
  ReferenceAxis = -> Sketch008 [N_Axis]
  Refine = true
  Suppressed = false
  Type = 0
FEATURE [Sketcher::SketchObject] Sketch009
  ArcFitTolerance = 1e-06
  AttachmentOffset = pos=(0,0,5) rot=(0,0,1;0rad)
  AttachmentSupport = -> [XZ_Plane003]
  FullyConstrained = true
  MakeInternals = false
  MapMode = 5
  Placement = pos=(0,-5,1.1e-15) rot=(1,0,0;1.5708rad)
  sketch-geometry (7):
    g0: LineSegment StartX=1.51554 StartY=-0.875 StartZ=0 EndX=1.51554 EndY=0.875 EndZ=0
    g1: LineSegment StartX=1.51554 StartY=0.875 StartZ=0 EndX=-2e-16 EndY=1.75 EndZ=0
    g2: LineSegment StartX=-2e-16 StartY=1.75 StartZ=0 EndX=-1.51554 EndY=0.875 EndZ=0
    g3: LineSegment StartX=-1.51554 StartY=0.875 StartZ=0 EndX=-1.51554 EndY=-0.875 EndZ=0
    g4: LineSegment StartX=-1.51554 StartY=-0.875 StartZ=0 EndX=0 EndY=-1.75 EndZ=0
    g5: LineSegment StartX=0 StartY=-1.75 StartZ=0 EndX=1.51554 EndY=-0.875 EndZ=0
    g6: Circle [constr] CenterX=0 CenterY=0 CenterZ=0 NormalX=0 NormalY=0 NormalZ=1 AngleXU=0 Radius=1.75
  constraints (17):
    c: Coincident(g0,g1)
    c: Coincident(g1,g2)
    c: Coincident(g2,g3)
    c: Coincident(g3,g4)
    c: Coincident(g4,g5)
    c: Coincident(g5,g0)
    c: Equal(g0, g1-g5) x5
    c: PointOnObject(g0,g6)
    c: PointOnObject(g1,g6)
    c: PointOnObject(g2,g6)
    c: PointOnObject(g3,g6)
    c: PointOnObject(g4,g6)
    c: PointOnObject(g5,g6)
    c: Coincident(g6,g-1)
    c: Diameter(g6) = 3.5
    c: Vertical(g3)
    c: DistanceX(g3,g0) = 3.03109
FEATURE [PartDesign::Pocket] Pocket002
  BaseFeature = -> Pad005
  Direction = (0,1,-2e-16)
  Length = 1.5
  Length2 = 5
  Placement = pos=(0,0,0) rot=(1,0,0;1.5708rad)
  Profile = -> Sketch009
  ReferenceAxis = -> Sketch009 [N_Axis]
  Refine = true
  Suppressed = false
  Type = 1
FEATURE [Sketcher::SketchObject] Sketch010
  ArcFitTolerance = 1e-06
  AttachmentSupport = -> [XZ_Plane004]
  FullyConstrained = true
  MakeInternals = false
  MapMode = 5
  Placement = pos=(0,0,0) rot=(1,0,0;1.5708rad)
  sketch-geometry (17):
    g0: LineSegment StartX=8 StartY=-2.5 StartZ=0 EndX=8 EndY=3.5 EndZ=0
    g1: LineSegment StartX=8 StartY=3.5 StartZ=0 EndX=-27 EndY=3.5 EndZ=0
    g2: LineSegment StartX=-27 StartY=3.5 StartZ=0 EndX=-27 EndY=-2.5 EndZ=0
    g3: LineSegment StartX=-27 StartY=-2.5 StartZ=0 EndX=-21.5588 EndY=-2.5 EndZ=0
    g4: LineSegment StartX=-21.5588 StartY=-2.5 StartZ=0 EndX=-20.1155 EndY=0 EndZ=0
    g5: LineSegment StartX=-20.1155 StartY=0 StartZ=0 EndX=-19.1155 EndY=0 EndZ=0
    g6: LineSegment StartX=-19.1155 StartY=0 StartZ=0 EndX=-17.4412 EndY=2.9 EndZ=0
    g7: LineSegment StartX=-17.4412 StartY=2.9 StartZ=0 EndX=1.55885 EndY=2.9 EndZ=0
    g8: LineSegment StartX=4.67654 StartY=-2.5 StartZ=0 EndX=8 EndY=-2.5 EndZ=0
    g9: LineSegment [constr] StartX=4.67654 StartY=-2.5 StartZ=0 EndX=0 EndY=-2.5 EndZ=0
    g10: LineSegment [constr] StartX=1.21244 StartY=2.9 StartZ=0 EndX=4.33013 EndY=-2.5 EndZ=0
    g11: LineSegment StartX=1.55885 StartY=2.9 StartZ=0 EndX=3.4641 EndY=-0.4 EndZ=0
    g12: LineSegment [constr] StartX=3.4641 StartY=-0.4 StartZ=0 EndX=4.67654 EndY=-2.5 EndZ=0
    g13: LineSegment StartX=3.4641 StartY=-0.4 StartZ=0 EndX=3.4641 EndY=-1 EndZ=0
    g14: LineSegment StartX=3.4641 StartY=-1 StartZ=0 EndX=4.33013 EndY=-2.5 EndZ=0
    g15: LineSegment StartX=4.33013 StartY=-2.5 StartZ=0 EndX=4.67654 EndY=-2.5 EndZ=0
    g16: Circle CenterX=0 CenterY=0 CenterZ=0 NormalX=0 NormalY=0 NormalZ=1 AngleXU=0 Radius=1.4
  constraints (50):
    c: Coincident(g0,g1)
    c: Coincident(g1,g2)
    c: Horizontal(g1)
    c: Vertical(g0)
    c: Vertical(g2)
    c: DistanceY(g0) = -2.5
    c: DistanceY(g0,g0) = 6
    c: Coincident(g2,g3)
    c: Horizontal(g3)
    c: Coincident(g3,g4)
    c: PointOnObject(g4,g-1)
    c: Coincident(g4,g5)
    c: PointOnObject(g5,g-1)
    c: Coincident(g5,g6)
    c: Coincident(g6,g7)
    c: Horizontal(g7)
    c: Coincident(g7,g11)
    c: DistanceY(g7) = 2.9
    c: Coincident(g8,g12)
    c: Coincident(g8,g0)
    c: Horizontal(g8)
    c: Angle(g6,g7) = 2.0944
    c: Horizontal(g3,g12)
    c: DistanceX(g7,g7) = 19
    c: DistanceX(g5,g5) = 1
    c: DistanceX(g1,g1) = 35
    c: DistanceX(g0) = 8
    c: DistanceY(g7,g0) = 0.6
    c: Coincident(g9,g12)
    c: Horizontal(g9)
    c: PointOnObject(g10,g7)
    c: PointOnObject(g10,g9)
    c: Coincident(g11,g12)
    c: Parallel(g10,g11)
    c: Parallel(g10,g12)
    c: Coincident(g13,g11)
    c: PointOnObject(g13,g10)
    c: Coincident(g14,g13)
    c: Coincident(g14,g10)
    c: Coincident(g15,g10)
    c: Coincident(g15,g8)
    c: Vertical(g13)
    c: Angle(g7,g11) = 2.0944
    c: DistanceY(g13) = -1
    c: Parallel(g4,g6)
    c: PointOnObject(g9,g-2)
    c: Distance(g-1,g10) = 2.5
    c: Distance(g-1,g11) = 2.8
    c: Coincident(g16,g-1)
    c: Diameter(g16) = 2.8
FEATURE [PartDesign::Pad] Pad006
  Direction = (0,-1,2e-16)
  Length = 5.2
  Length2 = 10
  Placement = pos=(0,0,0) rot=(1,0,0;1.5708rad)
  Profile = -> Sketch010
  ReferenceAxis = -> Sketch010 [N_Axis]
  Refine = true
  Suppressed = false
  Type = 0
FEATURE [Sketcher::SketchObject] Sketch012
  ArcFitTolerance = 1e-06
  AttachmentOffset = pos=(0,0,5.2) rot=(0,0,1;0rad)
  AttachmentSupport = -> [XZ_Plane004]
  FullyConstrained = true
  MakeInternals = false
  MapMode = 5
  Placement = pos=(0,-5.2,1.2e-15) rot=(1,0,0;1.5708rad)
  sketch-geometry (4):
    g0: LineSegment StartX=-27 StartY=3.5 StartZ=0 EndX=-27 EndY=-2.5 EndZ=0
    g1: LineSegment StartX=-27 StartY=-2.5 StartZ=0 EndX=8 EndY=-2.5 EndZ=0
    g2: LineSegment StartX=8 StartY=-2.5 StartZ=0 EndX=8 EndY=3.5 EndZ=0
    g3: LineSegment StartX=8 StartY=3.5 StartZ=0 EndX=-27 EndY=3.5 EndZ=0
  constraints (12):
    c: Coincident(g0,g1)
    c: Coincident(g1,g2)
    c: Coincident(g2,g3)
    c: Coincident(g3,g0)
    c: Vertical(g0)
    c: Vertical(g2)
    c: Horizontal(g1)
    c: Horizontal(g3)
    c: DistanceX(g3,g3) = 35
    c: DistanceY(g0,g0) = 6
    c: DistanceY(g1) = -2.5
    c: DistanceX(g2) = 8
FEATURE [Part::Box] Box  label="Cube"
  AttacherType = Attacher::AttachEngine3D
  Height = 6
  Length = 35
  Placement = pos=(-27,-10,-2.5) rot=(0,0,1;0rad)
  Width = 10
FEATURE [Sketcher::SketchObject] Sketch016
  ArcFitTolerance = 1e-06
  AttachmentSupport = -> [XY_Plane003]
  FullyConstrained = true
  MakeInternals = false
  MapMode = 5
  sketch-geometry (8):
    g0: ArcOfCircle CenterX=-14 CenterY=0 CenterZ=0 NormalX=0 NormalY=0 NormalZ=1 AngleXU=0 Radius=1.5 StartAngle=1.5708 EndAngle=4.71239
    g1: LineSegment StartX=4 StartY=1 StartZ=0 EndX=4 EndY=-1 EndZ=0
    g2: LineSegment StartX=-4 StartY=1 StartZ=0 EndX=4 EndY=1 EndZ=0
    g3: LineSegment StartX=-14 StartY=1.5 StartZ=0 EndX=-7 EndY=1.5 EndZ=0
    g4: LineSegment StartX=-7 StartY=1.5 StartZ=0 EndX=-4 EndY=1 EndZ=0
    g5: LineSegment StartX=-14 StartY=-1.5 StartZ=0 EndX=-7 EndY=-1.5 EndZ=0
    g6: LineSegment StartX=-7 StartY=-1.5 StartZ=0 EndX=-4 EndY=-1 EndZ=0
    g7: LineSegment StartX=-4 StartY=-1 StartZ=0 EndX=4 EndY=-1 EndZ=0
  constraints (25):
    c: DistanceY(g7) = -1
    c: DistanceX(g5) = -14
    c: Coincident(g5,g0) = -1.5708
    c: Coincident(g0,g3) = 1.5708
    c: Coincident(g2,g1)
    c: Coincident(g1,g7)
    c: Vertical(g1)
    c: PointOnObject(g0,g-1)
    c: DistanceX(g7) = 4
    c: Coincident(g4,g2)
    c: Horizontal(g2)
    c: Coincident(g3,g4)
    c: Horizontal(g3)
    c: Coincident(g5,g6)
    c: Horizontal(g5)
    c: Coincident(g6,g7)
    c: Horizontal(g7)
    c: Radius(g0) = 1.5
    c: Vertical(g5,g3)
    c: DistanceX(g6,g6) = 3
    c: Equal(g4,g6)
    c: Equal(g3,g5)
    c: Vertical(g0,g0)
    c: DistanceX(g2) = -4
    c: Vertical(g2,g6)
FEATURE [Sketcher::SketchObject] Sketch
  ArcFitTolerance = 1e-06
  AttachmentOffset = pos=(0,0,0) rot=(0,0,1;-1.5708rad)
  AttachmentSupport = -> [YZ_Plane003]
  FullyConstrained = false
  MakeInternals = false
  MapMode = 5
  Placement = pos=(0,0,0) rot=(0,-1,0;4.71239rad)
  sketch-geometry (18):
    g0-g3: Circle [constr] x4 (B-spline internal-alignment scaffolding for g4; pole/knot coordinates omitted)
    g4: BSplineCurve PolesCount=6 KnotsCount=3 Degree=3 IsPeriodic=0
    g5: GeomPoint [constr] X=1.75 Y=-5 Z=0
    g6: GeomPoint [constr] X=0 Y=-4 Z=0
    g7: GeomPoint [constr] X=-1.75 Y=-5 Z=0
    g8: Circle [constr] CenterX=0.442329 CenterY=-4 CenterZ=0 NormalX=0 NormalY=0 NormalZ=1 AngleXU=0 Radius=1
    g9: Circle [constr] CenterX=-0.442329 CenterY=-4 CenterZ=0 NormalX=0 NormalY=0 NormalZ=1 AngleXU=0 Radius=1
    g10: LineSegment [constr] StartX=-1.75 StartY=-5 StartZ=0 EndX=-1.30767 EndY=-5 EndZ=0
    g11: LineSegment [constr] StartX=1.30767 StartY=-5 StartZ=0 EndX=1.75 EndY=-5 EndZ=0
    g12: LineSegment [constr] StartX=0.442329 StartY=-4 StartZ=0 EndX=1.30767 EndY=-5 EndZ=0
    g13: LineSegment [constr] StartX=-0.442329 StartY=-4 StartZ=0 EndX=0 EndY=-4 EndZ=0
    g14: LineSegment [constr] StartX=0.442329 StartY=-4 StartZ=0 EndX=0 EndY=-4 EndZ=0
    g15: LineSegment StartX=-1.75 StartY=-5 StartZ=0 EndX=-1.75 EndY=-7.07699 EndZ=0
    g16: LineSegment StartX=-1.75 StartY=-7.07699 StartZ=0 EndX=1.75 EndY=-7.07699 EndZ=0
    g17: LineSegment StartX=1.75 StartY=-7.07699 StartZ=0 EndX=1.75 EndY=-5 EndZ=0
  constraints (40):
    c: Weight(g0) = 1
    c: Equal(g0,g1)
    c: Equal(g0,g2)
    c: Equal(g0,g3)
    c: InternalAlignment(g0-g3 -> g4) x4
    c: InternalAlignment(g5,g4)
    c: InternalAlignment(g6,g4)
    c: InternalAlignment(g7,g4)
    c: Horizontal(g2,g4)
    c: Horizontal(g4,g1)
    c: Horizontal(g1,g4)
    c: PointOnObject(g6,g-2)
    c: DistanceY(g4) = -5
    c: InternalAlignment(g8,g4)
    c: Equal(g8,g0)
    c: InternalAlignment(g9,g4)
    c: Equal(g9,g0)
    c: Horizontal(g8,g9)
    c: Coincident(g10,g4)
    c: Coincident(g10,g2)
    c: Coincident(g11,g1)
    c: Coincident(g11,g4)
    c: Coincident(g12,g8)
    c: Coincident(g12,g1)
    c: Coincident(g13,g9)
    c: Coincident(g13,g6)
    c: Coincident(g14,g8)
    c: Coincident(g14,g6)
    c: Equal(g14,g11)
    c: Equal(g13,g10)
    c: DistanceX(g4) = 1.75
    c: DistanceX(g4) = -1.75
    c: DistanceY(g6) = -4
    c: Coincident(g15,g4)
    c: Vertical(g15)
    c: Coincident(g15,g16)
    c: Horizontal(g16)
    c: Coincident(g16,g17)
    c: Coincident(g17,g4)
    c: Vertical(g17)
FEATURE [PartDesign::Pocket] Pocket004
  BaseFeature = -> Pocket002
  Direction = (-1,0,0)
  Length = 5
  Length2 = 5
  Placement = pos=(0,0,0) rot=(1,0,0;1.5708rad)
  Profile = -> Sketch
  ReferenceAxis = -> Sketch [N_Axis]
  Refine = true
  Reversed = true
  Suppressed = false
  Type = 0
FEATURE [PartDesign::PolarPattern] PolarPattern001
  Angle = 360
  Axis = -> Y_Axis003
  BaseFeature = -> Pocket002
  Mode = 1
  Occurrences = 4
  Offset = 120
  Originals = -> [Pocket004]
  Placement = pos=(0,0,0) rot=(1,0,0;1.5708rad)
  Refine = true
  Suppressed = false
  TransformMode = 0
FEATURE [PartDesign::Pocket] Pocket005
  BaseFeature = -> PolarPattern001
  Direction = (0,0,-1)
  Length = 5
  Length2 = 5
  Midplane = true
  Placement = pos=(0,0,0) rot=(1,0,0;1.5708rad)
  Profile = -> Sketch016
  ReferenceAxis = -> Sketch016 [N_Axis]
  Refine = true
  Suppressed = false
  Type = 1
FEATURE [PartDesign::Body] Body003  label="B001"
  AllowCompound = false
  Group = -> [Sketch008,Pad005,Sketch009,Pocket002,Pocket004,Sketch016,PolarPattern001,Sketch,Pocket005]
  Origin = -> Origin003
  Tip = -> Pocket005
FEATURE [PartDesign::FeatureBase] Clone
  BaseFeature = -> Body003
  Suppressed = false
FEATURE [PartDesign::Body] Body005
  AllowCompound = false
  Group = -> [Clone]
  Origin = -> Origin005
  Placement = pos=(0,0,0) rot=(0,1,0;4.18879rad)
  Tip = -> Clone
FEATURE [Part::Cut] Cut
  Base = -> Box
  Refine = true
  Tool = -> Body003
FEATURE [Part::Mirroring] Part__Mirroring001  label="B001 (Mirror #2)"
  Base = (0,0,0)
  Normal = (0,1,0)
  Source = -> Body003
FEATURE [Part::MultiFuse] Fusion001
  Refine = true
  Shapes = -> [Body003,Part__Mirroring001]
FEATURE [PartDesign::SubShapeBinder] Binder
  BindCopyOnChange = 0
  BindMode = 0
  ClaimChildren = false
  Context = -> Body004 [Binder.]
  Fuse = false
  MakeFace = true
  OffsetFill = false
  OffsetIntersection = false
  OffsetJoinType = 0
  OffsetOpenResult = false
  PartialLoad = false
  Placement = pos=(0,-0.2,0) rot=(0,0,1;0rad)
  Refine = true
  Relative = true
  Support = -> [Body003[Sketch.]]
  _Version = 2
FEATURE [PartDesign::Pad] Pad
  BaseFeature = -> Pad006
  Direction = (1,0,0)
  Length = 6
  Length2 = 10
  Placement = pos=(0,0,0) rot=(1,0,0;1.5708rad)
  Profile = -> Binder
  Refine = true
  Suppressed = false
  Type = 0
FEATURE [PartDesign::PolarPattern] PolarPattern002
  Angle = 360
  Axis = -> Y_Axis004
  BaseFeature = -> Pad
  Mode = 0
  Occurrences = 3
  Offset = 120
  Originals = -> [Pad]
  Placement = pos=(0,0,0) rot=(1,0,0;1.5708rad)
  Refine = true
  Suppressed = false
  TransformMode = 0
FEATURE [PartDesign::Pad] Pad008
  BaseFeature = -> PolarPattern002
  Direction = (0,-1,2e-16)
  Length = 4.8
  Length2 = 10
  Placement = pos=(0,0,0) rot=(1,0,0;1.5708rad)
  Profile = -> Sketch012
  ReferenceAxis = -> Sketch012 [N_Axis]
  Refine = true
  Suppressed = false
  Type = 0
FEATURE [Sketcher::SketchObject] Sketch017
  ArcFitTolerance = 1e-06
  AttachmentSupport = -> [XZ_Plane004]
  FullyConstrained = false
  MakeInternals = false
  MapMode = 5
  Placement = pos=(0,0,0) rot=(1,0,0;1.5708rad)
  sketch-geometry (8):
    g0: LineSegment StartX=-27 StartY=3.5 StartZ=0 EndX=-27 EndY=-2.5 EndZ=0
    g1: LineSegment StartX=-27 StartY=-2.5 StartZ=0 EndX=8 EndY=-2.5 EndZ=0
    g2: LineSegment StartX=8 StartY=-2.5 StartZ=0 EndX=8 EndY=3.5 EndZ=0
    g3: LineSegment StartX=8 StartY=3.5 StartZ=0 EndX=-27 EndY=3.5 EndZ=0
    g4: LineSegment StartX=-82.4426 StartY=43.1102 StartZ=0 EndX=-82.4426 EndY=-32.4768 EndZ=0
    g5: LineSegment StartX=-82.4426 StartY=-32.4768 StartZ=0 EndX=65.6399 EndY=-32.4768 EndZ=0
    g6: LineSegment StartX=65.6399 StartY=-32.4768 StartZ=0 EndX=65.6399 EndY=43.1102 EndZ=0
    g7: LineSegment StartX=65.6399 StartY=43.1102 StartZ=0 EndX=-82.4426 EndY=43.1102 EndZ=0
  constraints (20):
    c: Coincident(g0,g1)
    c: Coincident(g1,g2)
    c: Coincident(g2,g3)
    c: Coincident(g3,g0)
    c: Vertical(g2)
    c: Horizontal(g1)
    c: Horizontal(g3)
    c: Distance(g0,g2) = 35
    c: Distance(g1,g3) = 6
    c: DistanceY(g0) = -2.5
    c: DistanceX(g2) = 8
    c: Vertical(g0)
    c: Coincident(g4,g5)
    c: Coincident(g5,g6)
    c: Coincident(g6,g7)
    c: Coincident(g7,g4)
    c: Vertical(g4)
    c: Vertical(g6)
    c: Horizontal(g5)
    c: Horizontal(g7)
FEATURE [PartDesign::Pocket] Pocket
  BaseFeature = -> Pad008
  Direction = (0,1,-2e-16)
  Length = 5
  Length2 = 5
  Midplane = true
  Placement = pos=(0,0,0) rot=(1,0,0;1.5708rad)
  Profile = -> Sketch017
  ReferenceAxis = -> Sketch017 [N_Axis]
  Refine = true
  Suppressed = false
  Type = 1
FEATURE [Sketcher::SketchObject] Sketch018
  ArcFitTolerance = 1e-06
  AttachmentSupport = -> [Pocket]
  FullyConstrained = true
  MakeInternals = false
  MapMode = 5
  Placement = pos=(0,-1.1e-15,-2.5) rot=(1,0,0;3.14159rad)
  sketch-geometry (5):
    g0: LineSegment StartX=-26 StartY=-5 StartZ=0 EndX=-26 EndY=5.2 EndZ=0
    g1: LineSegment StartX=-26 StartY=5.2 StartZ=0 EndX=-19.4182 EndY=9 EndZ=0
    g2: LineSegment StartX=-19.4182 StartY=9 StartZ=0 EndX=-17.2243 EndY=5.2 EndZ=0
    g3: LineSegment StartX=-17.2243 StartY=5.2 StartZ=0 EndX=-17.2243 EndY=-5 EndZ=0
    g4: LineSegment StartX=-17.2243 StartY=-5 StartZ=0 EndX=-26 EndY=-5 EndZ=0
  constraints (15):
    c: Coincident(g1,g2)
    c: Coincident(g2,g3)
    c: Vertical(g3)
    c: Coincident(g3,g4)
    c: Horizontal(g4)
    c: Angle(g0,g1) = 2.0944
    c: Perpendicular(g1,g2)
    c: DistanceY(g1) = 9
    c: Equal(g3,g0)
    c: Coincident(g1,g0)
    c: Vertical(g0)
    c: Coincident(g0,g4)
    c: DistanceX(g0) = -26
    c: DistanceY(g0) = 5.2
    c: DistanceY(g0) = -5
FEATURE [PartDesign::Pocket] Pocket006
  BaseFeature = -> Pocket
  Direction = (0,0,1)
  Length = 2.5
  Length2 = 5
  Placement = pos=(0,0,0) rot=(1,0,0;1.5708rad)
  Profile = -> Sketch018
  ReferenceAxis = -> Sketch018 [N_Axis]
  Refine = true
  Suppressed = false
  TaperAngle = -30
  Type = 0
FEATURE [PartDesign::Body] Body004  label="B002"
  AllowCompound = true
  Group = -> [Sketch010,Pad006,Sketch012,Binder,Pad,PolarPattern002,Sketch017,Pad008,Pocket,Sketch018,Pocket006]
  Origin = -> Origin004
  Tip = -> Pocket006
FEATURE [Part::Cut] Cut001
  Base = -> Cut
  Refine = true
  Tool = -> Body004
FEATURE [Part::Mirroring] Part__Mirroring  label="Cut001 (Mirror #1)"
  Base = (-26,-2e-16,-2.5)
  MirrorPlane = -> Cut001 [Face1]
  Normal = (0,1,0)
  Source = -> Cut001
FEATURE [Part::MultiFuse] Fusion
  Refine = true
  Shapes = -> [Cut001,Part__Mirroring]
FEATURE [Part::Mirroring] Part__Mirroring002  label="B002 (Mirror #3)"
  Base = (0,0,0)
  Normal = (0,1,0)
  Source = -> Body004
FEATURE [Part::MultiFuse] Fusion002
  Refine = true
  Shapes = -> [Body004,Part__Mirroring002]
FEATURE [Part::Compound] Compound
  Links = -> [Fusion001,Fusion002]
FEATURE [Mesh::Feature] Mesh  label="Compound (Meshed)"
---- part parts_v3.FCStd = doc fcstd_760042610ce4 (53926 chars; too large to inline — full recipe in that document) ----
